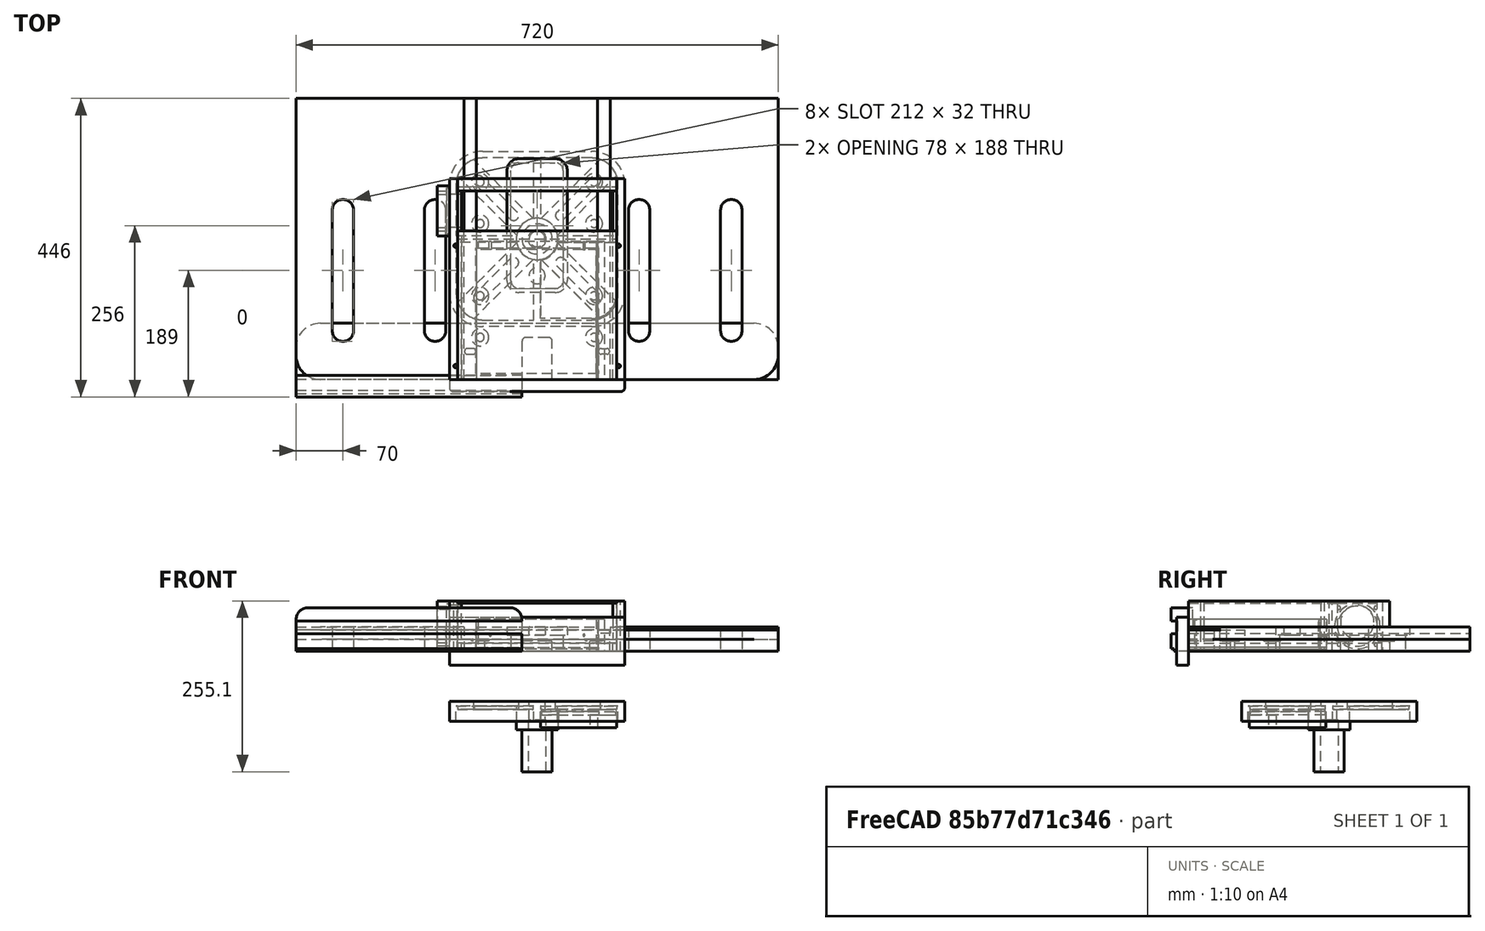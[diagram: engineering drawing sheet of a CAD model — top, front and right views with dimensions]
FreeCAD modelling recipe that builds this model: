
FCSTD DOCUMENT  (FreeCAD 0.22R36874 (Git))
Label: drill_press_table
License: All rights reserved
LicenseURL: http://en.wikipedia.org/wiki/All_rights_reserved
objects: TechDraw::DrawViewDimension×76, Sketcher::SketchObject×58, PartDesign::Pocket×35, PartDesign::Pad×21, PartDesign::Body×21, TechDraw::DrawProjGroupItem×16, TechDraw::DrawSVGTemplate×7, TechDraw::DrawProjGroup×7, TechDraw::DrawPage×7, PartDesign::Mirrored×4, App::Part×4, PartDesign::FeatureBase×3, PartDesign::PolarPattern×3, TechDraw::DrawViewImage×3, TechDraw::DrawComplexSection×2, Spreadsheet::Sheet×1, PartDesign::Fillet×1, TechDraw::DrawViewAnnotation×1, App::DocumentObjectGroup×1
note: 314 computed .brp shape members not serialized (recipe doc carries the construction recipe); baked Part::Feature solids carry a one-line shape summary decoded from their .brp

FEATURE [Spreadsheet::Sheet] Spreadsheet
  cells = A1='table_length; B1(table_length)==720 mm; D1='plywood_18; E1(ply_18)==18 mm; F1='iron_cast_table; G1(iron_cast_table)==262 mm; I1='tee nuts DIN1624; L1='via holes diameters; A2='table_depth; B2(table_depth)==420 mm; D2='plywood_12; E2(ply_12)==12 mm; F2='mounting_screws_distance; G2(mounting_screws_distance)==170 mm; I2='M8_D; J2(DIN1624_M8_D)==22.2 mm; L2='M8_D; M2(otw_przel_M8)==8.4 mm; D3='plywood_3; E3(ply_3)==3 mm; I3='M8_d1; J3(DIN1624_M8_d1)==9.1 mm; A4='table_radius; B4(table_radius)==6 mm; I4='M8_a; J4(DIN1624_M8_a)==1.2 mm; I5='M8_L1; J5(DIN1624_M8_L1)==11 mm; A6='t_track_slim_width; B6(t_track_width)==19 mm; C6='https://allegro.pl/oferta/t-track-slim-1220mm-profil-aluminiowy-t-zielony-10608302634?fromVariant=12640372726; A7='t_track_slim_depth; B7(t_track_depth)==9.5 mm; D7='fence_base_d; E7(fence_base_d)==32 mm; I7='M10_D; J7(DIN1624_M10_D)==25.5 mm; D8='fence_face_d; E8(fence_face_d)==32 mm; I8='M10_d1; J8(DIN1624_M10_d1)==12 mm; A9='clamp_slot_width; B9(clamp_slot_width)==32 mm; I9='M10_a; J9(DIN1624_M10_a)==1.2 mm; I10='M10_L1; J10(DIN1624_M10_L1)==13 mm; A11='insert_width; B11(insert_width)==90 mm; D11='base_width; E11(base_width)==G1; A12='insert_depth; B12(insert_depth)==200 mm; D12='base_depth; E12(base_depth)==E1 + 60 mm + E2 + E15 + 10 mm; I12='M12_D; J12(DIN1624_M12_D)==27 mm; D13='base_height; E13(base_height)==75 mm; I13='M12_d1; J13(DIN1624_M12_d1)==13.7 mm; I14='M12_a; J14(DIN1624_M12_a)==1.6 mm; D15='drawer_depth; E15(drawer_depth)==200 mm; I15='M12_L1; J15(DIN1624_M12_L1)==14.5 mm; D16='drawer_slide_width; E16==12.7 mm; D17='drawer_total_depth; E17(drawer_total_depth)==E15 + 6 mm; D18='drawer_total_width; E18(drawer_total_width)==E11 - 2 * E1 - 2 * E16; D19='drawer_total_height; E19(drawer_total_height)==E13 - E1 - 9 mm
FEATURE [Sketcher::SketchObject] Sketch
  FullyConstrained = true
  MapMode = 5
  expr: .Constraints.table_radius_big = 6 * Spreadsheet.table_radius
  expr: Constraints[11] = .Constraints.table_radius_big
  expr: Constraints[12] = Spreadsheet.table_depth
  expr: Constraints[13] = Spreadsheet.table_length
  sketch-geometry (6):
    g0: LineSegment StartX=-360 StartY=420 StartZ=0 EndX=360 EndY=420 EndZ=0
    g1: LineSegment StartX=360 StartY=420 StartZ=0 EndX=360 EndY=36 EndZ=0
    g2: LineSegment StartX=324 StartY=3.695e-13 StartZ=0 EndX=-324 EndY=3.695e-13 EndZ=0
    g3: LineSegment StartX=-360 StartY=36 StartZ=0 EndX=-360 EndY=420 EndZ=0
    g4: ArcOfCircle CenterX=-324 CenterY=36 CenterZ=0 NormalX=0 NormalY=0 NormalZ=1 AngleXU=0 Radius=36 StartAngle=3.14159 EndAngle=4.71239
    g5: ArcOfCircle CenterX=324 CenterY=36 CenterZ=0 NormalX=0 NormalY=0 NormalZ=1 AngleXU=0 Radius=36 StartAngle=4.71239 EndAngle=6.28319
  constraints (15):
    c: Coincident(g0,g1)
    c: Coincident(g3,g0)
    c: Horizontal(g0)
    c: Horizontal(g2)
    c: Vertical(g1)
    c: Vertical(g3)
    c: Tangent(g3,g4) = 1.5708
    c: Tangent(g2,g4) = 1.5708
    c: Tangent(g2,g5) = 1.5708
    c: Tangent(g1,g5) = 1.5708
    c: Radius(g4) = 36  'table_radius_big'
    c: Radius(g5) = 36
    c: DistanceY(g2,g0) = 420
    c: DistanceX(g3,g1) = 720
    c: Symmetric(g2,g2,g-1)
FEATURE [PartDesign::Pad] Pad
  Direction = (0,0,1)
  Length = 18
  Length2 = 10
  Profile = -> Sketch
  ReferenceAxis = -> Sketch [N_Axis]
  Suppressed = false
  Type = 0
FEATURE [Sketcher::SketchObject] Sketch001
  FullyConstrained = true
  MapMode = 5
  Placement = pos=(0,0,18) rot=(0,0,1;0rad)
  expr: Constraints[12] = Spreadsheet.clamp_slot_width
  expr: Constraints[13] = Spreadsheet.clamp_slot_width
  expr: Constraints[14] = Spreadsheet.table_length / 2 - 70 mm
  expr: Constraints[15] = Spreadsheet.iron_cast_table / 2 + 2 / 3 * Spreadsheet.clamp_slot_width
  expr: Constraints[32] = Spreadsheet.clamp_slot_width
  expr: Constraints[33] = Spreadsheet.clamp_slot_width
  expr: Constraints[34] = Spreadsheet.iron_cast_table / 2 + 2 / 3 * Spreadsheet.clamp_slot_width
  expr: Constraints[35] = Spreadsheet.table_length / 2 - 70 mm
  expr: Constraints[52] = 2 * Spreadsheet.table_radius
  expr: Constraints[53] = 2 * Spreadsheet.table_radius
  expr: Constraints[54] = 2 * Spreadsheet.table_radius
  expr: Constraints[55] = 2 * Spreadsheet.table_radius
  expr: Constraints[56] = Spreadsheet.insert_depth - 2 * Spreadsheet.table_radius
  expr: Constraints[57] = Spreadsheet.insert_width - 2 * Spreadsheet.table_radius
  expr: Constraints[58] = (Spreadsheet.insert_width - 2 * Spreadsheet.table_radius) / 2
  expr: Constraints[59] = 130 mm + Spreadsheet.table_radius
  expr: Constraints[60] = Spreadsheet.DIN1624_M10_d1
  expr: Constraints[61] = Spreadsheet.mounting_screws_distance
  expr: Constraints[62] = Spreadsheet.mounting_screws_distance
  expr: Constraints[63] = Spreadsheet.mounting_screws_distance
  expr: Constraints[64] = Spreadsheet.mounting_screws_distance
  expr: Constraints[67] = Spreadsheet.mounting_screws_distance / 2
  expr: Constraints[68] = Spreadsheet.mounting_screws_distance / 2
  sketch-geometry (28):
    g0: ArcOfCircle CenterX=-290 CenterY=253 CenterZ=0 NormalX=0 NormalY=0 NormalZ=1 AngleXU=0 Radius=16 StartAngle=4e-16 EndAngle=3.14159
    g1: ArcOfCircle CenterX=-290 CenterY=73 CenterZ=0 NormalX=0 NormalY=0 NormalZ=1 AngleXU=0 Radius=16 StartAngle=3.14159 EndAngle=6.28319
    g2: LineSegment StartX=-306 StartY=253 StartZ=0 EndX=-306 EndY=73 EndZ=0
    g3: LineSegment StartX=-274 StartY=73 StartZ=0 EndX=-274 EndY=253 EndZ=0
    g4: ArcOfCircle CenterX=-152.333 CenterY=253 CenterZ=0 NormalX=0 NormalY=0 NormalZ=1 AngleXU=0 Radius=16 StartAngle=1e-16 EndAngle=3.14159
    g5: ArcOfCircle CenterX=-152.333 CenterY=73 CenterZ=0 NormalX=0 NormalY=0 NormalZ=1 AngleXU=0 Radius=16 StartAngle=3.14159 EndAngle=6.28319
    g6: LineSegment StartX=-168.333 StartY=253 StartZ=0 EndX=-168.333 EndY=73 EndZ=0
    g7: LineSegment StartX=-136.333 StartY=73 StartZ=0 EndX=-136.333 EndY=253 EndZ=0
    g8: ArcOfCircle CenterX=290 CenterY=253 CenterZ=0 NormalX=0 NormalY=0 NormalZ=1 AngleXU=0 Radius=16 StartAngle=5e-16 EndAngle=3.14159
    g9: ArcOfCircle CenterX=290 CenterY=73 CenterZ=0 NormalX=0 NormalY=0 NormalZ=1 AngleXU=0 Radius=16 StartAngle=3.14159 EndAngle=6.28319
    g10: LineSegment StartX=306 StartY=253 StartZ=0 EndX=306 EndY=73 EndZ=0
    g11: LineSegment StartX=274 StartY=73 StartZ=0 EndX=274 EndY=253 EndZ=0
    g12: ArcOfCircle CenterX=152.333 CenterY=253 CenterZ=0 NormalX=0 NormalY=0 NormalZ=1 AngleXU=0 Radius=16 StartAngle=5e-16 EndAngle=3.14159
    g13: ArcOfCircle CenterX=152.333 CenterY=73 CenterZ=0 NormalX=0 NormalY=0 NormalZ=1 AngleXU=0 Radius=16 StartAngle=3.14159 EndAngle=6.28319
    g14: LineSegment StartX=168.333 StartY=253 StartZ=0 EndX=168.333 EndY=73 EndZ=0
    g15: LineSegment StartX=136.333 StartY=73 StartZ=0 EndX=136.333 EndY=253 EndZ=0
    g16: LineSegment StartX=-27 StartY=324 StartZ=0 EndX=27 EndY=324 EndZ=0
    g17: LineSegment StartX=39 StartY=312 StartZ=0 EndX=39 EndY=148 EndZ=0
    g18: LineSegment StartX=27 StartY=136 StartZ=0 EndX=-27 EndY=136 EndZ=0
    g19: LineSegment StartX=-39 StartY=148 StartZ=0 EndX=-39 EndY=312 EndZ=0
    g20: ArcOfCircle CenterX=-27 CenterY=312 CenterZ=0 NormalX=0 NormalY=0 NormalZ=1 AngleXU=0 Radius=12 StartAngle=1.5708 EndAngle=3.14159
    g21: ArcOfCircle CenterX=27 CenterY=312 CenterZ=0 NormalX=0 NormalY=0 NormalZ=1 AngleXU=0 Radius=12 StartAngle=3.37e-14 EndAngle=1.5708
    g22: ArcOfCircle CenterX=-27 CenterY=148 CenterZ=0 NormalX=0 NormalY=0 NormalZ=1 AngleXU=0 Radius=12 StartAngle=3.14159 EndAngle=4.71239
    g23: ArcOfCircle CenterX=27 CenterY=148 CenterZ=0 NormalX=0 NormalY=0 NormalZ=1 AngleXU=0 Radius=12 StartAngle=4.71239 EndAngle=6.28319
    g24: Circle CenterX=-85 CenterY=125 CenterZ=0 NormalX=0 NormalY=0 NormalZ=1 AngleXU=0 Radius=6
    g25: Circle CenterX=-85 CenterY=295 CenterZ=0 NormalX=0 NormalY=0 NormalZ=1 AngleXU=0 Radius=6
    g26: Circle CenterX=85 CenterY=295 CenterZ=0 NormalX=0 NormalY=0 NormalZ=1 AngleXU=0 Radius=6
    g27: Circle CenterX=85 CenterY=125 CenterZ=0 NormalX=0 NormalY=0 NormalZ=1 AngleXU=0 Radius=6
  constraints (72):
    c: Tangent(g0,g2) = -1.5708
    c: Tangent(g2,g1) = -1.5708
    c: Tangent(g1,g3) = -1.5708
    c: Tangent(g3,g0) = -1.5708
    c: Equal(g0,g1)
    c: Vertical(g2)
    c: Tangent(g4,g6) = -1.5708
    c: Tangent(g6,g5) = -1.5708
    c: Tangent(g5,g7) = -1.5708
    c: Tangent(g7,g4) = -1.5708
    c: Equal(g4,g5)
    c: Vertical(g6)
    c: Diameter(g0) = 32
    c: Diameter(g4) = 32
    c: DistanceX(g1,g-1) = 290
    c: DistanceX(g5,g-1) = 152.333
    c: DistanceY(g-1,g1) = 73
    c: DistanceY(g-1,g5) = 73
    c: DistanceY(g1,g0) = 180
    c: DistanceY(g5,g4) = 180
    c: Tangent(g8,g10) = 1.5708
    c: Tangent(g10,g9) = 1.5708
    c: Tangent(g9,g11) = 1.5708
    c: Tangent(g11,g8) = 1.5708
    c: Equal(g8,g9)
    c: Vertical(g10)
    c: Tangent(g12,g14) = 1.5708
    c: Tangent(g14,g13) = 1.5708
    c: Tangent(g13,g15) = 1.5708
    c: Tangent(g15,g12) = 1.5708
    c: Equal(g12,g13)
    c: Vertical(g14)
    c: Diameter(g8) = 32
    c: Diameter(g12) = 32
    c: DistanceX(g-1,g13) = 152.333
    c: DistanceX(g-1,g9) = 290
    c: DistanceY(g-1,g13) = 73
    c: DistanceY(g-1,g9) = 73
    c: DistanceY(g13,g12) = 180
    c: DistanceY(g9,g8) = 180
    c: Horizontal(g16)
    c: Horizontal(g18)
    c: Vertical(g17)
    c: Vertical(g19)
    c: Tangent(g19,g20) = 1.5708
    c: Tangent(g16,g20) = 1.5708
    c: Tangent(g16,g21) = 1.5708
    c: Tangent(g17,g21) = 1.5708
    c: Tangent(g19,g22) = 1.5708
    c: Tangent(g18,g22) = 1.5708
    c: Tangent(g18,g23) = 1.5708
    c: Tangent(g17,g23) = 1.5708
    c: Radius(g20) = 12
    c: Radius(g21) = 12
    c: Radius(g23) = 12
    c: Radius(g22) = 12
    c: DistanceY(g18,g16) = 188
    c: DistanceX(g19,g17) = 78
    c: DistanceX(g19,g-1) = 39
    c: DistanceY(g-1,g18) = 136
    c: Diameter(g25) = 12
    c: DistanceX(g24,g27) = 170
    c: DistanceX(g25,g26) = 170
    c: DistanceY(g24,g25) = 170
    c: DistanceY(g27,g26) = 170
    c: DistanceY(g-1,g27) = 125
    c: DistanceY(g-1,g24) = 125
    c: DistanceX(g24,g-1) = 85
    c: DistanceX(g25,g-1) = 85
    c: Equal(g25,g26)
    c: Equal(g26,g27)
    c: Equal(g27,g24)
FEATURE [PartDesign::Pocket] Pocket
  BaseFeature = -> Pad
  Direction = (0,0,-1)
  Length = 18
  Length2 = 5
  Profile = -> Sketch001
  ReferenceAxis = -> Sketch001 [N_Axis]
  Suppressed = false
  Type = 0
FEATURE [Sketcher::SketchObject] Sketch002
  FullyConstrained = true
  MapMode = 5
  expr: Constraints[10] = 6 * Spreadsheet.table_radius
  expr: Constraints[11] = 6 * Spreadsheet.table_radius
  expr: Constraints[12] = Spreadsheet.table_length
  expr: Constraints[13] = Spreadsheet.table_depth
  sketch-geometry (6):
    g0: LineSegment StartX=-360 StartY=420 StartZ=0 EndX=360 EndY=420 EndZ=0
    g1: LineSegment StartX=360 StartY=420 StartZ=0 EndX=360 EndY=36 EndZ=0
    g2: LineSegment StartX=324 StartY=3.695e-13 StartZ=0 EndX=-324 EndY=3.695e-13 EndZ=0
    g3: LineSegment StartX=-360 StartY=36 StartZ=0 EndX=-360 EndY=420 EndZ=0
    g4: ArcOfCircle CenterX=-324 CenterY=36 CenterZ=0 NormalX=0 NormalY=0 NormalZ=1 AngleXU=0 Radius=36 StartAngle=3.14159 EndAngle=4.71239
    g5: ArcOfCircle CenterX=324 CenterY=36 CenterZ=0 NormalX=0 NormalY=0 NormalZ=1 AngleXU=0 Radius=36 StartAngle=4.71239 EndAngle=6.28319
  constraints (15):
    c: Coincident(g0,g1)
    c: Coincident(g3,g0)
    c: Horizontal(g0)
    c: Horizontal(g2)
    c: Vertical(g1)
    c: Vertical(g3)
    c: Tangent(g3,g4) = 1.5708
    c: Tangent(g2,g4) = 1.5708
    c: Tangent(g2,g5) = 1.5708
    c: Tangent(g1,g5) = 1.5708
    c: Radius(g4) = 36
    c: Radius(g5) = 36
    c: DistanceX(g3,g1) = 720
    c: DistanceY(g2,g0) = 420
    c: Symmetric(g2,g2,g-1)
FEATURE [PartDesign::Pad] Pad001
  Direction = (0,0,1)
  Length = 18
  Length2 = 10
  Profile = -> Sketch002
  ReferenceAxis = -> Sketch002 [N_Axis]
  Suppressed = false
  Type = 0
  expr: Length = Spreadsheet.ply_18
FEATURE [Sketcher::SketchObject] Sketch003  label="slots"
  FullyConstrained = true
  MapMode = 5
  Placement = pos=(0,0,18) rot=(0,0,1;0rad)
  sketch-geometry (24):
    g0: ArcOfCircle CenterX=-290 CenterY=253 CenterZ=0 NormalX=0 NormalY=0 NormalZ=1 AngleXU=0 Radius=16 StartAngle=2e-16 EndAngle=3.14159
    g1: ArcOfCircle CenterX=-290 CenterY=73 CenterZ=0 NormalX=0 NormalY=0 NormalZ=1 AngleXU=0 Radius=16 StartAngle=3.14159 EndAngle=6.28319
    g2: LineSegment StartX=-306 StartY=253 StartZ=0 EndX=-306 EndY=73 EndZ=0
    g3: LineSegment StartX=-274 StartY=73 StartZ=0 EndX=-274 EndY=253 EndZ=0
    g4: ArcOfCircle CenterX=-152.333 CenterY=253 CenterZ=0 NormalX=0 NormalY=0 NormalZ=1 AngleXU=0 Radius=16 StartAngle=1.1e-15 EndAngle=3.14159
    g5: ArcOfCircle CenterX=-152.333 CenterY=73 CenterZ=0 NormalX=0 NormalY=0 NormalZ=1 AngleXU=0 Radius=16 StartAngle=3.14159 EndAngle=6.28319
    g6: LineSegment StartX=-168.333 StartY=253 StartZ=0 EndX=-168.333 EndY=73 EndZ=0
    g7: LineSegment StartX=-136.333 StartY=73 StartZ=0 EndX=-136.333 EndY=253 EndZ=0
    g8: ArcOfCircle CenterX=290 CenterY=253 CenterZ=0 NormalX=0 NormalY=0 NormalZ=1 AngleXU=0 Radius=16 StartAngle=-9e-16 EndAngle=3.14159
    g9: ArcOfCircle CenterX=290 CenterY=73 CenterZ=0 NormalX=0 NormalY=0 NormalZ=1 AngleXU=0 Radius=16 StartAngle=3.14159 EndAngle=6.28319
    g10: LineSegment StartX=306 StartY=253 StartZ=0 EndX=306 EndY=73 EndZ=0
    g11: LineSegment StartX=274 StartY=73 StartZ=0 EndX=274 EndY=253 EndZ=0
    g12: ArcOfCircle CenterX=152.333 CenterY=253 CenterZ=0 NormalX=0 NormalY=0 NormalZ=1 AngleXU=0 Radius=16 StartAngle=5e-16 EndAngle=3.14159
    g13: ArcOfCircle CenterX=152.333 CenterY=73 CenterZ=0 NormalX=0 NormalY=0 NormalZ=1 AngleXU=0 Radius=16 StartAngle=3.14159 EndAngle=6.28319
    g14: LineSegment StartX=168.333 StartY=253 StartZ=0 EndX=168.333 EndY=73 EndZ=0
    g15: LineSegment StartX=136.333 StartY=73 StartZ=0 EndX=136.333 EndY=253 EndZ=0
    g16: LineSegment StartX=-27 StartY=324 StartZ=0 EndX=27 EndY=324 EndZ=0
    g17: LineSegment StartX=39 StartY=312 StartZ=0 EndX=39 EndY=148 EndZ=0
    g18: LineSegment StartX=27 StartY=136 StartZ=0 EndX=-27 EndY=136 EndZ=0
    g19: LineSegment StartX=-39 StartY=148 StartZ=0 EndX=-39 EndY=312 EndZ=0
    g20: ArcOfCircle CenterX=-27 CenterY=312 CenterZ=0 NormalX=0 NormalY=0 NormalZ=1 AngleXU=0 Radius=12 StartAngle=1.5708 EndAngle=3.14159
    g21: ArcOfCircle CenterX=27 CenterY=312 CenterZ=0 NormalX=0 NormalY=0 NormalZ=1 AngleXU=0 Radius=12 StartAngle=3.58e-14 EndAngle=1.5708
    g22: ArcOfCircle CenterX=27 CenterY=148 CenterZ=0 NormalX=0 NormalY=0 NormalZ=1 AngleXU=0 Radius=12 StartAngle=4.71239 EndAngle=6.28319
    g23: ArcOfCircle CenterX=-27 CenterY=148 CenterZ=0 NormalX=0 NormalY=0 NormalZ=1 AngleXU=0 Radius=12 StartAngle=3.14159 EndAngle=4.71239
  constraints (60):
    c: Tangent(g0,g2) = -1.5708
    c: Tangent(g2,g1) = -1.5708
    c: Tangent(g1,g3) = -1.5708
    c: Tangent(g3,g0) = -1.5708
    c: Equal(g0,g1)
    c: Vertical(g2)
    c: Tangent(g4,g6) = -1.5708
    c: Tangent(g6,g5) = -1.5708
    c: Tangent(g5,g7) = -1.5708
    c: Tangent(g7,g4) = -1.5708
    c: Equal(g4,g5)
    c: Vertical(g6)
    c: Diameter(g0) = 32
    c: Diameter(g4) = 32
    c: DistanceX(g1,g-1) = 290  '1st_slot'
    c: DistanceX(g5,g-1) = 152.333  '2nd_slot'
    c: DistanceY(g-1,g1) = 73
    c: DistanceY(g-1,g5) = 73
    c: DistanceY(g1,g0) = 180
    c: DistanceY(g5,g4) = 180
    c: Tangent(g8,g10) = 1.5708
    c: Tangent(g10,g9) = 1.5708
    c: Tangent(g9,g11) = 1.5708
    c: Tangent(g11,g8) = 1.5708
    c: Equal(g8,g9)
    c: Vertical(g10)
    c: Tangent(g12,g14) = 1.5708
    c: Tangent(g14,g13) = 1.5708
    c: Tangent(g13,g15) = 1.5708
    c: Tangent(g15,g12) = 1.5708
    c: Equal(g12,g13)
    c: Vertical(g14)
    c: Diameter(g8) = 32
    c: Diameter(g12) = 32
    c: DistanceX(g-1,g13) = 152.333
    c: DistanceX(g-1,g9) = 290
    c: DistanceY(g-1,g13) = 73
    c: DistanceY(g-1,g9) = 73
    c: DistanceY(g13,g12) = 180
    c: DistanceY(g9,g8) = 180
    c: Horizontal(g16)
    c: Horizontal(g18)
    c: Vertical(g17)
    c: Vertical(g19)
    c: Tangent(g16,g20) = 1.5708
    c: Tangent(g19,g20) = 1.5708
    c: Tangent(g16,g21) = 1.5708
    c: Tangent(g17,g21) = 1.5708
    c: Tangent(g17,g22) = 1.5708
    c: Tangent(g18,g22) = 1.5708
    c: Tangent(g18,g23) = 1.5708
    c: Tangent(g19,g23) = 1.5708
    c: Radius(g20) = 12
    c: Radius(g21) = 12
    c: Radius(g22) = 12
    c: Radius(g23) = 12
    c: DistanceX(g19,g17) = 78
    c: DistanceY(g-1,g18) = 136
    c: DistanceY(g18,g16) = 188
    c: DistanceX(g19,g-1) = 39
FEATURE [PartDesign::Pocket] Pocket001
  BaseFeature = -> Pad001
  Direction = (0,0,-1)
  Length = 18
  Length2 = 5
  Profile = -> Sketch003
  ReferenceAxis = -> Sketch003 [N_Axis]
  Suppressed = false
  Type = 0
  expr: Length = Spreadsheet.ply_18
FEATURE [Sketcher::SketchObject] Sketch004  label="t_tracks_sk"
  FullyConstrained = true
  MapMode = 5
  Placement = pos=(0,0,18) rot=(0,0,1;0rad)
  expr: .Constraints.t_track_distance = 100 mm - Spreadsheet.t_track_width / 2
  expr: Constraints[17] = Spreadsheet.t_track_width
  expr: Constraints[19] = Spreadsheet.table_depth
  sketch-geometry (8):
    g0: LineSegment StartX=-109.5 StartY=420 StartZ=0 EndX=-90.5 EndY=420 EndZ=0
    g1: LineSegment StartX=-90.5 StartY=420 StartZ=0 EndX=-90.5 EndY=0 EndZ=0
    g2: LineSegment StartX=-90.5 StartY=0 StartZ=0 EndX=-109.5 EndY=0 EndZ=0
    g3: LineSegment StartX=-109.5 StartY=0 StartZ=0 EndX=-109.5 EndY=420 EndZ=0
    g4: LineSegment StartX=109.5 StartY=420 StartZ=0 EndX=90.5 EndY=420 EndZ=0
    g5: LineSegment StartX=90.5 StartY=420 StartZ=0 EndX=90.5 EndY=0 EndZ=0
    g6: LineSegment StartX=90.5 StartY=0 StartZ=0 EndX=109.5 EndY=0 EndZ=0
    g7: LineSegment StartX=109.5 StartY=0 StartZ=0 EndX=109.5 EndY=420 EndZ=0
  constraints (23):
    c: Coincident(g0,g1)
    c: Coincident(g1,g2)
    c: Coincident(g2,g3)
    c: Coincident(g3,g0)
    c: Horizontal(g0)
    c: Horizontal(g2)
    c: Vertical(g1)
    c: Vertical(g3)
    c: Coincident(g4,g5)
    c: Coincident(g5,g6)
    c: Coincident(g6,g7)
    c: Coincident(g7,g4)
    c: Horizontal(g4)
    c: Horizontal(g6)
    c: Vertical(g5)
    c: Vertical(g7)
    c: Equal(g1,g7)
    c: DistanceX(g0,g0) = 19
    c: Equal(g0,g4)
    c: DistanceY(g3,g3) = 420
    c: DistanceX(g1,g-1) = 90.5  't_track_distance'
    c: DistanceY(g1,g-1) = 0
    c: Symmetric(g1,g5,g-1)
FEATURE [PartDesign::Pocket] Pocket002
  BaseFeature = -> Pocket001
  Direction = (0,0,-1)
  Length = 9.5
  Length2 = 5
  Profile = -> Sketch004
  ReferenceAxis = -> Sketch004 [N_Axis]
  Suppressed = false
  Type = 0
  expr: Length = Spreadsheet.t_track_depth
FEATURE [Sketcher::SketchObject] Sketch005
  FullyConstrained = true
  MapMode = 5
  expr: Constraints[26] = Spreadsheet.iron_cast_table
  expr: Constraints[5] = Spreadsheet.iron_cast_table
  sketch-geometry (12):
    g0: LineSegment StartX=-81 StartY=131 StartZ=0 EndX=81 EndY=131 EndZ=0
    g1: LineSegment StartX=131 StartY=81 StartZ=0 EndX=131 EndY=-81 EndZ=0
    g2: LineSegment StartX=81 StartY=-131 StartZ=0 EndX=-81 EndY=-131 EndZ=0
    g3: LineSegment StartX=-131 StartY=-81 StartZ=0 EndX=-131 EndY=81 EndZ=0
    g4: ArcOfCircle CenterX=-81 CenterY=81 CenterZ=0 NormalX=0 NormalY=0 NormalZ=1 AngleXU=0 Radius=50 StartAngle=1.5708 EndAngle=3.14159
    g5: GeomPoint X=-131 Y=131 Z=0
    g6: ArcOfCircle CenterX=81 CenterY=81 CenterZ=0 NormalX=0 NormalY=0 NormalZ=1 AngleXU=0 Radius=50 StartAngle=0 EndAngle=1.5708
    g7: GeomPoint X=131 Y=131 Z=0
    g8: ArcOfCircle CenterX=81 CenterY=-81 CenterZ=0 NormalX=0 NormalY=0 NormalZ=1 AngleXU=0 Radius=50 StartAngle=4.71239 EndAngle=6.28319
    g9: GeomPoint X=131 Y=-131 Z=0
    g10: ArcOfCircle CenterX=-81 CenterY=-81 CenterZ=0 NormalX=0 NormalY=0 NormalZ=1 AngleXU=0 Radius=50 StartAngle=3.14159 EndAngle=4.71239
    g11: GeomPoint X=-131 Y=-131 Z=0
  constraints (27):
    c: Horizontal(g0)
    c: Horizontal(g2)
    c: Vertical(g1)
    c: Vertical(g3)
    c: Symmetric(g5,g9,g-1)
    c: DistanceX(g11,g9) = 262
    c: PointOnObject(g5,g3)
    c: PointOnObject(g5,g0)
    c: Tangent(g3,g4) = 1.5708
    c: Tangent(g0,g4) = 1.5708
    c: PointOnObject(g7,g0)
    c: PointOnObject(g7,g1)
    c: Tangent(g0,g6) = 1.5708
    c: Tangent(g1,g6) = 1.5708
    c: PointOnObject(g9,g1)
    c: PointOnObject(g9,g2)
    c: Tangent(g1,g8) = 1.5708
    c: Tangent(g2,g8) = 1.5708
    c: PointOnObject(g11,g2)
    c: PointOnObject(g11,g3)
    c: Tangent(g2,g10) = 1.5708
    c: Tangent(g3,g10) = 1.5708
    c: Radius(g4) = 50
    c: Equal(g4,g6)
    c: Equal(g6,g8)
    c: Equal(g8,g10)
    c: DistanceY(g2,g0) = 262
FEATURE [PartDesign::Pad] Pad002
  Direction = (0,0,1)
  Length = 30
  Length2 = 10
  Profile = -> Sketch005
  ReferenceAxis = -> Sketch005 [N_Axis]
  Suppressed = false
  Type = 0
FEATURE [Sketcher::SketchObject] Sketch006
  ExternalGeometry = -> [Pocket]
  FullyConstrained = true
  MapMode = 5
  Placement = pos=(0,0,18) rot=(0,0,1;0rad)
  expr: Constraints[5] = Spreadsheet.DIN1624_M10_D
  sketch-geometry (4):
    g0: Circle CenterX=-85 CenterY=295 CenterZ=0 NormalX=0 NormalY=0 NormalZ=1 AngleXU=0 Radius=12.75
    g1: Circle CenterX=85 CenterY=295 CenterZ=0 NormalX=0 NormalY=0 NormalZ=1 AngleXU=0 Radius=12.75
    g2: Circle CenterX=-85 CenterY=125 CenterZ=0 NormalX=0 NormalY=0 NormalZ=1 AngleXU=0 Radius=12.75
    g3: Circle CenterX=85 CenterY=125 CenterZ=0 NormalX=0 NormalY=0 NormalZ=1 AngleXU=0 Radius=12.75
  constraints (8):
    c: Coincident(g0,g-4)
    c: Coincident(g1,g-5)
    c: Equal(g2,g0)
    c: Equal(g0,g1)
    c: Equal(g1,g3)
    c: Diameter(g2) = 25.5
    c: Coincident(g2,g-6)
    c: Coincident(g3,g-3)
FEATURE [PartDesign::Pocket] Pocket003
  BaseFeature = -> Pocket
  Direction = (0,0,-1)
  Length = 2.4
  Length2 = 5
  Profile = -> Sketch006
  ReferenceAxis = -> Sketch006 [N_Axis]
  Suppressed = false
  Type = 0
  expr: Length = 2 * Spreadsheet.DIN1624_M10_a
FEATURE [Sketcher::SketchObject] Sketch007
  ExternalGeometry = -> [Pocket002]
  FullyConstrained = true
  MapMode = 5
  Placement = pos=(0,0,18) rot=(0,0,1;0rad)
  expr: Constraints[12] = Spreadsheet.insert_width
  sketch-geometry (8):
    g0: LineSegment StartX=-27 StartY=330 StartZ=0 EndX=27 EndY=330 EndZ=0
    g1: LineSegment StartX=45 StartY=312 StartZ=0 EndX=45 EndY=148 EndZ=0
    g2: LineSegment StartX=27 StartY=130 StartZ=0 EndX=-27 EndY=130 EndZ=0
    g3: LineSegment StartX=-45 StartY=148 StartZ=0 EndX=-45 EndY=312 EndZ=0
    g4: ArcOfCircle CenterX=-27 CenterY=312 CenterZ=0 NormalX=0 NormalY=0 NormalZ=1 AngleXU=0 Radius=18 StartAngle=1.5708 EndAngle=3.14159
    g5: ArcOfCircle CenterX=27 CenterY=312 CenterZ=0 NormalX=0 NormalY=0 NormalZ=1 AngleXU=0 Radius=18 StartAngle=9e-16 EndAngle=1.5708
    g6: ArcOfCircle CenterX=27 CenterY=148 CenterZ=0 NormalX=0 NormalY=0 NormalZ=1 AngleXU=0 Radius=18 StartAngle=4.71239 EndAngle=6.28319
    g7: ArcOfCircle CenterX=-27 CenterY=148 CenterZ=0 NormalX=0 NormalY=0 NormalZ=1 AngleXU=0 Radius=18 StartAngle=3.14159 EndAngle=4.71239
  constraints (18):
    c: Horizontal(g0)
    c: Horizontal(g2)
    c: Vertical(g1)
    c: Vertical(g3)
    c: Tangent(g0,g4) = 1.5708
    c: Tangent(g3,g4) = 1.5708
    c: Tangent(g0,g5) = 1.5708
    c: Tangent(g1,g5) = 1.5708
    c: Tangent(g1,g6) = 1.5708
    c: Tangent(g2,g6) = 1.5708
    c: Tangent(g2,g7) = 1.5708
    c: Tangent(g3,g7) = 1.5708
    c: DistanceX(g3,g1) = 90
    c: Equal(g7,g6)
    c: Equal(g6,g4)
    c: Equal(g4,g5)
    c: Coincident(g7,g-5)
    c: Coincident(g5,g-3)
FEATURE [PartDesign::Pocket] Pocket004
  BaseFeature = -> Pocket002
  Direction = (0,0,-1)
  Length = 12
  Length2 = 5
  Profile = -> Sketch007
  ReferenceAxis = -> Sketch007 [N_Axis]
  Suppressed = false
  Type = 0
  expr: Length = Spreadsheet.ply_12
FEATURE [Sketcher::SketchObject] Sketch008
  FullyConstrained = true
  MapMode = 5
  expr: Constraints[12] = 3 * Spreadsheet.table_radius
  expr: Constraints[16] = Spreadsheet.insert_depth
  expr: Constraints[17] = Spreadsheet.insert_width
  sketch-geometry (8):
    g0: LineSegment StartX=-27 StartY=100 StartZ=0 EndX=27 EndY=100 EndZ=0
    g1: LineSegment StartX=45 StartY=82 StartZ=0 EndX=45 EndY=-82 EndZ=0
    g2: LineSegment StartX=27 StartY=-100 StartZ=0 EndX=-27 EndY=-100 EndZ=0
    g3: LineSegment StartX=-45 StartY=-82 StartZ=0 EndX=-45 EndY=82 EndZ=0
    g4: ArcOfCircle CenterX=-27 CenterY=-82 CenterZ=0 NormalX=0 NormalY=0 NormalZ=1 AngleXU=0 Radius=18 StartAngle=3.14159 EndAngle=4.71239
    g5: ArcOfCircle CenterX=27 CenterY=-82 CenterZ=0 NormalX=0 NormalY=0 NormalZ=1 AngleXU=0 Radius=18 StartAngle=4.71239 EndAngle=6.28319
    g6: ArcOfCircle CenterX=27 CenterY=82 CenterZ=0 NormalX=0 NormalY=0 NormalZ=1 AngleXU=0 Radius=18 StartAngle=0 EndAngle=1.5708
    g7: ArcOfCircle CenterX=-27 CenterY=82 CenterZ=0 NormalX=0 NormalY=0 NormalZ=1 AngleXU=0 Radius=18 StartAngle=1.5708 EndAngle=3.14159
  constraints (19):
    c: Horizontal(g0)
    c: Horizontal(g2)
    c: Vertical(g1)
    c: Vertical(g3)
    c: Tangent(g3,g4) = 1.5708
    c: Tangent(g2,g4) = 1.5708
    c: Tangent(g2,g5) = 1.5708
    c: Tangent(g1,g5) = 1.5708
    c: Tangent(g1,g6) = 1.5708
    c: Tangent(g0,g6) = 1.5708
    c: Tangent(g0,g7) = 1.5708
    c: Tangent(g3,g7) = 1.5708
    c: Radius(g7) = 18
    c: Equal(g7,g6)
    c: Equal(g6,g5)
    c: Equal(g5,g4)
    c: DistanceY(g2,g0) = 200
    c: DistanceX(g3,g1) = 90
    c: Symmetric(g3,g1,g-1)
FEATURE [PartDesign::Pad] Pad003
  Direction = (0,0,1)
  Length = 12
  Length2 = 10
  Profile = -> Sketch008
  ReferenceAxis = -> Sketch008 [N_Axis]
  Suppressed = false
  Type = 0
  expr: Length = Spreadsheet.ply_12
FEATURE [Sketcher::SketchObject] Sketch009  label="base_pad"
  FullyConstrained = true
  MapMode = 5
  expr: .Constraints.fence_base_depth = 14 * Spreadsheet.table_radius
  expr: Constraints[10] = 6 * Spreadsheet.table_radius
  expr: Constraints[12] = Spreadsheet.table_length
  sketch-geometry (6):
    g0: LineSegment StartX=-324 StartY=84 StartZ=0 EndX=324 EndY=84 EndZ=0
    g1: LineSegment StartX=360 StartY=48 StartZ=0 EndX=360 EndY=0 EndZ=0
    g2: LineSegment StartX=360 StartY=0 StartZ=0 EndX=-360 EndY=0 EndZ=0
    g3: LineSegment StartX=-360 StartY=0 StartZ=0 EndX=-360 EndY=48 EndZ=0
    g4: ArcOfCircle CenterX=-324 CenterY=48 CenterZ=0 NormalX=0 NormalY=0 NormalZ=1 AngleXU=0 Radius=36 StartAngle=1.5708 EndAngle=3.14159
    g5: ArcOfCircle CenterX=324 CenterY=48 CenterZ=0 NormalX=0 NormalY=0 NormalZ=1 AngleXU=0 Radius=36 StartAngle=0 EndAngle=1.5708
  constraints (15):
    c: Coincident(g1,g2)
    c: Coincident(g2,g3)
    c: Horizontal(g0)
    c: Horizontal(g2)
    c: Vertical(g1)
    c: Vertical(g3)
    c: Tangent(g3,g4) = 1.5708
    c: Tangent(g0,g4) = 1.5708
    c: Tangent(g0,g5) = 1.5708
    c: Tangent(g1,g5) = 1.5708
    c: Radius(g4) = 36
    c: Equal(g4,g5)
    c: DistanceX(g2,g1) = 720
    c: DistanceY(g2,g0) = 84  'fence_base_depth'
    c: Symmetric(g2,g1,g-1)
FEATURE [PartDesign::Pad] Pad004
  Direction = (0,0,1)
  Length = 32
  Length2 = 10
  Profile = -> Sketch009
  ReferenceAxis = -> Sketch009 [N_Axis]
  Suppressed = false
  Type = 0
  expr: Length = Spreadsheet.fence_base_d
FEATURE [Sketcher::SketchObject] Sketch010
  FullyConstrained = true
  MapMode = 5
  Placement = pos=(0,0,32) rot=(0,0,1;0rad)
  expr: .Constraints.slot_length = Spreadsheet.otw_przel_M8
  expr: Constraints[6] = Spreadsheet.otw_przel_M8
  expr: Constraints[7] = 1 / 2 * <<base_pad>>.Constraints.fence_base_depth
  expr: Constraints[9] = Sketch004.Constraints.t_track_distance - .Constraints.slot_length / 2 + 9.5 mm
  sketch-geometry (4):
    g0: ArcOfCircle CenterX=-104.2 CenterY=42 CenterZ=0 NormalX=0 NormalY=0 NormalZ=1 AngleXU=0 Radius=4.2 StartAngle=1.5708 EndAngle=4.71239
    g1: ArcOfCircle CenterX=-95.8 CenterY=42 CenterZ=0 NormalX=0 NormalY=0 NormalZ=1 AngleXU=0 Radius=4.2 StartAngle=4.71239 EndAngle=7.85398
    g2: LineSegment StartX=-104.2 StartY=37.8 StartZ=0 EndX=-95.8 EndY=37.8 EndZ=0
    g3: LineSegment StartX=-95.8 StartY=46.2 StartZ=0 EndX=-104.2 EndY=46.2 EndZ=0
  constraints (10):
    c: Tangent(g0,g2) = -1.5708
    c: Tangent(g2,g1) = -1.5708
    c: Tangent(g1,g3) = -1.5708
    c: Tangent(g3,g0) = -1.5708
    c: Equal(g0,g1)
    c: Horizontal(g2)
    c: Diameter(g1) = 8.4
    c: DistanceY(g-1,g1) = 42
    c: DistanceX(g0,g1) = 8.4  'slot_length'
    c: DistanceX(g1,g-1) = 95.8
FEATURE [PartDesign::Pocket] Pocket005
  BaseFeature = -> Pad004
  Direction = (0,0,-1)
  Length = 32
  Length2 = 5
  Profile = -> Sketch010
  ReferenceAxis = -> Sketch010 [N_Axis]
  Suppressed = false
  Type = 0
  expr: Length = Spreadsheet.fence_base_d
FEATURE [PartDesign::Mirrored] Mirrored
  BaseFeature = -> Pocket005
  MirrorPlane = -> Sketch010 [V_Axis]
  Originals = -> [Pocket005]
  Suppressed = false
FEATURE [Sketcher::SketchObject] Sketch011
  FullyConstrained = true
  MapMode = 5
  Placement = pos=(0,0,0) rot=(1,0,0;3.14159rad)
  expr: Constraints[12] = Spreadsheet.table_radius
  expr: Constraints[13] = Spreadsheet.table_radius
  expr: Constraints[14] = 3 / 4 * <<base_pad>>.Constraints.fence_base_depth
  sketch-geometry (6):
    g0: LineSegment StartX=-22.5 StartY=0 StartZ=0 EndX=22.5 EndY=0 EndZ=0
    g1: LineSegment StartX=22.5 StartY=0 StartZ=0 EndX=22.5 EndY=-57 EndZ=0
    g2: LineSegment StartX=16.5 StartY=-63 StartZ=0 EndX=-16.5 EndY=-63 EndZ=0
    g3: LineSegment StartX=-22.5 StartY=-57 StartZ=0 EndX=-22.5 EndY=0 EndZ=0
    g4: ArcOfCircle CenterX=16.5 CenterY=-57 CenterZ=0 NormalX=0 NormalY=0 NormalZ=1 AngleXU=0 Radius=6 StartAngle=4.71239 EndAngle=6.28319
    g5: ArcOfCircle CenterX=-16.5 CenterY=-57 CenterZ=0 NormalX=0 NormalY=0 NormalZ=1 AngleXU=0 Radius=6 StartAngle=3.14159 EndAngle=4.71239
  constraints (15):
    c: Coincident(g0,g1)
    c: Coincident(g3,g0)
    c: Horizontal(g0)
    c: Horizontal(g2)
    c: Vertical(g1)
    c: Vertical(g3)
    c: DistanceX(g0,g0) = 45  'fence_opening'
    c: Symmetric(g0,g0,g-1)
    c: Tangent(g2,g4) = 1.5708
    c: Tangent(g1,g4) = 1.5708
    c: Tangent(g2,g5) = 1.5708
    c: Tangent(g3,g5) = 1.5708
    c: Radius(g5) = 6
    c: Radius(g4) = 6
    c: DistanceY(g2,g0) = 63
FEATURE [PartDesign::Pocket] Pocket006
  BaseFeature = -> Mirrored
  Direction = (0,0,1)
  Length = 16
  Length2 = 5
  Profile = -> Sketch011
  ReferenceAxis = -> Sketch011 [N_Axis]
  Suppressed = false
  Type = 0
  expr: Length = Spreadsheet.fence_base_d / 2
FEATURE [PartDesign::Body] Body005  label="fence_base"
  Group = -> [Sketch009,Pad004,Sketch010,Pocket005,Mirrored,Sketch011,Pocket006]
  Origin = -> Origin007
  Tip = -> Pocket006
FEATURE [Sketcher::SketchObject] Sketch012  label="fence_face"
  FullyConstrained = true
  MapMode = 5
  expr: .Constraints.fence_length = Spreadsheet.table_length / 2 - 45 mm / 2
  expr: Constraints[11] = 3 * Spreadsheet.table_radius
  sketch-geometry (6):
    g0: LineSegment StartX=18 StartY=65 StartZ=0 EndX=319.5 EndY=65 EndZ=0
    g1: LineSegment StartX=337.5 StartY=47 StartZ=0 EndX=337.5 EndY=0 EndZ=0
    g2: LineSegment StartX=337.5 StartY=0 StartZ=0 EndX=0 EndY=0 EndZ=0
    g3: LineSegment StartX=0 StartY=0 StartZ=0 EndX=0 EndY=47 EndZ=0
    g4: ArcOfCircle CenterX=18 CenterY=47 CenterZ=0 NormalX=0 NormalY=0 NormalZ=1 AngleXU=0 Radius=18 StartAngle=1.5708 EndAngle=3.14159
    g5: ArcOfCircle CenterX=319.5 CenterY=47 CenterZ=0 NormalX=0 NormalY=0 NormalZ=1 AngleXU=0 Radius=18 StartAngle=0 EndAngle=1.5708
  constraints (15):
    c: Coincident(g1,g2)
    c: Coincident(g2,g3)
    c: Horizontal(g0)
    c: Horizontal(g2)
    c: Vertical(g1)
    c: Vertical(g3)
    c: Tangent(g3,g4) = 1.5708
    c: Tangent(g0,g4) = 1.5708
    c: Tangent(g0,g5) = 1.5708
    c: Tangent(g1,g5) = 1.5708
    c: Equal(g4,g5)
    c: Radius(g4) = 18
    c: DistanceX(g2,g2) = 337.5  'fence_length'
    c: Coincident(g2,g-1)
    c: DistanceY(g1,g0) = 65  'fence_height'
FEATURE [PartDesign::Pad] Pad005
  Direction = (0,0,1)
  Length = 32
  Length2 = 10
  Profile = -> Sketch012
  ReferenceAxis = -> Sketch012 [N_Axis]
  Suppressed = false
  Type = 0
  expr: Length = Spreadsheet.fence_face_d
FEATURE [Sketcher::SketchObject] Sketch013
  FullyConstrained = true
  MapMode = 5
  Placement = pos=(0,0,32) rot=(0,0,1;0rad)
  expr: Constraints[11] = Sketch012.Constraints.fence_height / 2 - 9.5 mm + 3 mm
  expr: Constraints[8] = Spreadsheet.t_track_width
  expr: Constraints[9] = Sketch012.Constraints.fence_length
  sketch-geometry (4):
    g0: LineSegment StartX=0 StartY=45 StartZ=0 EndX=337.5 EndY=45 EndZ=0
    g1: LineSegment StartX=337.5 StartY=45 StartZ=0 EndX=337.5 EndY=26 EndZ=0
    g2: LineSegment StartX=337.5 StartY=26 StartZ=0 EndX=0 EndY=26 EndZ=0
    g3: LineSegment StartX=0 StartY=26 StartZ=0 EndX=0 EndY=45 EndZ=0
  constraints (12):
    c: Coincident(g0,g1)
    c: Coincident(g1,g2)
    c: Coincident(g2,g3)
    c: Coincident(g3,g0)
    c: Horizontal(g0)
    c: Horizontal(g2)
    c: Vertical(g1)
    c: Vertical(g3)
    c: DistanceY(g3,g3) = 19
    c: DistanceX(g2,g2) = 337.5
    c: DistanceX(g2,g-1) = 0
    c: DistanceY(g-1,g2) = 26
FEATURE [PartDesign::Pocket] Pocket007
  BaseFeature = -> Pad005
  Direction = (0,0,-1)
  Length = 9.5
  Length2 = 5
  Profile = -> Sketch013
  ReferenceAxis = -> Sketch013 [N_Axis]
  Suppressed = false
  Type = 0
  expr: Length = Spreadsheet.t_track_depth
FEATURE [Sketcher::SketchObject] Sketch014
  FullyConstrained = true
  MapMode = 5
  Placement = pos=(0,0,32) rot=(0,0,1;0rad)
  expr: Constraints[10] = Sketch012.Constraints.fence_length
  sketch-geometry (4):
    g0: LineSegment StartX=0 StartY=4 StartZ=0 EndX=337.5 EndY=4 EndZ=0
    g1: LineSegment StartX=337.5 StartY=4 StartZ=0 EndX=337.5 EndY=0 EndZ=0
    g2: LineSegment StartX=337.5 StartY=0 StartZ=0 EndX=0 EndY=0 EndZ=0
    g3: LineSegment StartX=0 StartY=0 StartZ=0 EndX=0 EndY=4 EndZ=0
  constraints (11):
    c: Coincident(g0,g1)
    c: Coincident(g1,g2)
    c: Coincident(g2,g3)
    c: Coincident(g3,g0)
    c: Horizontal(g0)
    c: Horizontal(g2)
    c: Vertical(g1)
    c: Vertical(g3)
    c: DistanceY(g1,g1) = 4
    c: Coincident(g2,g-1)
    c: DistanceX(g2,g2) = 337.5
FEATURE [PartDesign::Pocket] Pocket008
  BaseFeature = -> Pocket007
  Direction = (0,0,-1)
  Length = 4
  Length2 = 5
  Profile = -> Sketch014
  ReferenceAxis = -> Sketch014 [N_Axis]
  Suppressed = false
  Type = 0
FEATURE [Sketcher::SketchObject] Sketch015
  FullyConstrained = true
  MapMode = 5
  Placement = pos=(0,0,0) rot=(1,0,0;3.14159rad)
  expr: Constraints[8] = Spreadsheet.fence_base_d
  expr: Constraints[9] = Sketch012.Constraints.fence_length
  sketch-geometry (4):
    g0: LineSegment StartX=0 StartY=0 StartZ=0 EndX=337.5 EndY=0 EndZ=0
    g1: LineSegment StartX=337.5 StartY=0 StartZ=0 EndX=337.5 EndY=-32 EndZ=0
    g2: LineSegment StartX=337.5 StartY=-32 StartZ=0 EndX=0 EndY=-32 EndZ=0
    g3: LineSegment StartX=0 StartY=-32 StartZ=0 EndX=0 EndY=0 EndZ=0
  constraints (11):
    c: Coincident(g0,g1)
    c: Coincident(g1,g2)
    c: Coincident(g2,g3)
    c: Coincident(g3,g0)
    c: Horizontal(g0)
    c: Horizontal(g2)
    c: Vertical(g1)
    c: Vertical(g3)
    c: DistanceY(g1,g1) = 32
    c: DistanceX(g0,g0) = 337.5
    c: Coincident(g-1,g0)
FEATURE [PartDesign::Pocket] Pocket009
  BaseFeature = -> Pocket008
  Direction = (0,0,1)
  Length = 6
  Length2 = 5
  Profile = -> Sketch015
  ReferenceAxis = -> Sketch015 [N_Axis]
  Suppressed = false
  Type = 0
FEATURE [PartDesign::Body] Body004  label="fence_face_r"
  Group = -> [Sketch012,Pad005,Sketch013,Pocket007,Sketch014,Pocket008,Sketch015,Pocket009]
  Origin = -> Origin004
  Placement = pos=(22.5,6,0) rot=(1,0,0;1.5708rad)
  Tip = -> Pocket009
FEATURE [PartDesign::FeatureBase] Clone
  BaseFeature = -> Body004
  Placement = pos=(22.5,6,0) rot=(1,0,0;1.5708rad)
  Suppressed = false
FEATURE [PartDesign::Body] Body006  label="fence_face_l"
  Group = -> [Clone]
  Origin = -> Origin008
  Placement = pos=(-382.5,0,0) rot=(0,0,1;0rad)
  Tip = -> Clone
  expr: .Placement.Base.x = -Spreadsheet.table_length / 2 - 45 mm / 2
FEATURE [App::Part] Part001  label="fence"
  Group = -> [Body004,Body005,Body006]
  Origin = -> Origin006
  Placement = pos=(0,300,36) rot=(0,0,1;0rad)
FEATURE [Sketcher::SketchObject] Sketch016  label="base_main_sk"
  FullyConstrained = true
  MapMode = 5
  expr: .Constraints.base_depth = Spreadsheet.base_depth - Spreadsheet.ply_18 + Spreadsheet.table_radius
  expr: .Constraints.base_width = Spreadsheet.iron_cast_table - 2 * Spreadsheet.ply_18 + 2 * Spreadsheet.table_radius
  sketch-geometry (4):
    g0: LineSegment StartX=-119 StartY=288 StartZ=0 EndX=119 EndY=288 EndZ=0
    g1: LineSegment StartX=119 StartY=288 StartZ=0 EndX=119 EndY=0 EndZ=0
    g2: LineSegment StartX=119 StartY=0 StartZ=0 EndX=-119 EndY=0 EndZ=0
    g3: LineSegment StartX=-119 StartY=0 StartZ=0 EndX=-119 EndY=288 EndZ=0
  constraints (11):
    c: Coincident(g0,g1)
    c: Coincident(g1,g2)
    c: Coincident(g2,g3)
    c: Coincident(g3,g0)
    c: Horizontal(g0)
    c: Horizontal(g2)
    c: Vertical(g1)
    c: Vertical(g3)
    c: Symmetric(g2,g1,g-1)
    c: DistanceX(g2,g2) = 238  'base_width'
    c: DistanceY(g3,g3) = 288  'base_depth'
FEATURE [PartDesign::Pad] Pad006
  Direction = (0,0,1)
  Length = 18
  Length2 = 10
  Profile = -> Sketch016
  ReferenceAxis = -> Sketch016 [N_Axis]
  Suppressed = false
  Type = 0
  expr: Length = Spreadsheet.ply_18
FEATURE [Sketcher::SketchObject] Sketch018
  FullyConstrained = true
  MapMode = 5
  Placement = pos=(-119,0,0) rot=(0.57735,-0.57735,-0.57735;2.0944rad)
  expr: Constraints[11] = <<base_main_sk>>.Constraints.base_depth
  expr: Constraints[8] = Spreadsheet.table_radius
  expr: Constraints[9] = Spreadsheet.ply_18 - Spreadsheet.table_radius
  sketch-geometry (4):
    g0: LineSegment StartX=-288 StartY=12 StartZ=0 EndX=-282 EndY=12 EndZ=0
    g1: LineSegment StartX=-282 StartY=12 StartZ=0 EndX=-282 EndY=0 EndZ=0
    g2: LineSegment StartX=-282 StartY=0 StartZ=0 EndX=-288 EndY=0 EndZ=0
    g3: LineSegment StartX=-288 StartY=0 StartZ=0 EndX=-288 EndY=12 EndZ=0
  constraints (12):
    c: Coincident(g0,g1)
    c: Coincident(g1,g2)
    c: Coincident(g2,g3)
    c: Coincident(g3,g0)
    c: Horizontal(g0)
    c: Horizontal(g2)
    c: Vertical(g1)
    c: Vertical(g3)
    c: DistanceX(g0,g0) = 6
    c: DistanceY(g3,g3) = 12
    c: DistanceY(g1,g-1) = 0
    c: DistanceX(g2,g-1) = 288
FEATURE [PartDesign::Pocket] Pocket010
  BaseFeature = -> Pad006
  Direction = (1,0,0)
  Length = 238
  Length2 = 5
  Profile = -> Sketch018
  ReferenceAxis = -> Sketch018 [N_Axis]
  Suppressed = false
  Type = 0
  expr: Length = <<base_main_sk>>.Constraints.base_width
FEATURE [Sketcher::SketchObject] Sketch017
  FullyConstrained = true
  MapMode = 5
  Placement = pos=(0,0,0) rot=(1,0,0;1.5708rad)
  expr: Constraints[10] = Spreadsheet.ply_18 - Spreadsheet.table_radius
  expr: Constraints[11] = <<base_main_sk>>.Constraints.base_width / 2
  expr: Constraints[8] = Spreadsheet.table_radius
  sketch-geometry (4):
    g0: LineSegment StartX=-119 StartY=12 StartZ=0 EndX=-113 EndY=12 EndZ=0
    g1: LineSegment StartX=-113 StartY=12 StartZ=0 EndX=-113 EndY=0 EndZ=0
    g2: LineSegment StartX=-113 StartY=0 StartZ=0 EndX=-119 EndY=0 EndZ=0
    g3: LineSegment StartX=-119 StartY=0 StartZ=0 EndX=-119 EndY=12 EndZ=0
  constraints (12):
    c: Coincident(g0,g1)
    c: Coincident(g1,g2)
    c: Coincident(g2,g3)
    c: Coincident(g3,g0)
    c: Horizontal(g0)
    c: Horizontal(g2)
    c: Vertical(g1)
    c: Vertical(g3)
    c: DistanceX(g0,g0) = 6
    c: DistanceY(g-1,g1) = 0
    c: DistanceY(g3,g3) = 12
    c: DistanceX(g2,g-1) = 119
FEATURE [PartDesign::Pocket] Pocket011
  BaseFeature = -> Pocket010
  Direction = (0,1,-2e-16)
  Length = 288
  Length2 = 5
  Profile = -> Sketch017
  ReferenceAxis = -> Sketch017 [N_Axis]
  Suppressed = false
  Type = 0
  expr: Length = <<base_main_sk>>.Constraints.base_depth
FEATURE [PartDesign::Mirrored] Mirrored001
  BaseFeature = -> Pocket011
  MirrorPlane = -> Sketch017 [V_Axis]
  Originals = -> [Pocket011]
  Suppressed = false
FEATURE [Sketcher::SketchObject] Sketch019
  FullyConstrained = true
  MapMode = 5
  Placement = pos=(0,0,18) rot=(0,0,1;0rad)
  expr: Constraints[0] = Spreadsheet.mounting_screws_distance / 2
  expr: Constraints[10] = Spreadsheet.mounting_screws_distance
  expr: Constraints[11] = Spreadsheet.mounting_screws_distance
  expr: Constraints[1] = Spreadsheet.DIN1624_M10_d1
  expr: Constraints[5] = Spreadsheet.mounting_screws_distance
  expr: Constraints[6] = Spreadsheet.mounting_screws_distance
  expr: Constraints[7] = (Spreadsheet.table_depth - Spreadsheet.mounting_screws_distance) / 2 - 62 mm
  sketch-geometry (4):
    g0: Circle CenterX=-85 CenterY=63 CenterZ=0 NormalX=0 NormalY=0 NormalZ=1 AngleXU=0 Radius=6
    g1: Circle CenterX=-85 CenterY=233 CenterZ=0 NormalX=0 NormalY=0 NormalZ=1 AngleXU=0 Radius=6
    g2: Circle CenterX=85 CenterY=233 CenterZ=0 NormalX=0 NormalY=0 NormalZ=1 AngleXU=0 Radius=6
    g3: Circle CenterX=85 CenterY=63 CenterZ=0 NormalX=0 NormalY=0 NormalZ=1 AngleXU=0 Radius=6
  constraints (12):
    c: DistanceX(g0,g-1) = 85
    c: Diameter(g0) = 12
    c: Equal(g0,g1)
    c: Equal(g1,g2)
    c: Equal(g2,g3)
    c: DistanceY(g0,g1) = 170
    c: DistanceX(g0,g3) = 170
    c: DistanceY(g-1,g0) = 63
    c: DistanceY(g3,g0) = 0
    c: DistanceX(g0,g1) = 0
    c: DistanceX(g0,g2) = 170
    c: DistanceY(g0,g2) = 170
FEATURE [PartDesign::Pocket] Pocket012
  BaseFeature = -> Mirrored001
  Direction = (0,0,-1)
  Length = 18
  Length2 = 5
  Profile = -> Sketch019
  ReferenceAxis = -> Sketch019 [N_Axis]
  Suppressed = false
  Type = 0
  expr: Length = Spreadsheet.ply_18
FEATURE [Sketcher::SketchObject] Sketch020
  ExternalGeometry = -> [Pocket012]
  FullyConstrained = true
  MapMode = 5
  Placement = pos=(0,0,18) rot=(0,0,1;0rad)
  expr: Constraints[3] = Spreadsheet.DIN1624_M10_D
  sketch-geometry (4):
    g0: Circle CenterX=-85 CenterY=63 CenterZ=0 NormalX=0 NormalY=0 NormalZ=1 AngleXU=0 Radius=12.75
    g1: Circle CenterX=85 CenterY=63 CenterZ=0 NormalX=0 NormalY=0 NormalZ=1 AngleXU=0 Radius=12.75
    g2: Circle CenterX=85 CenterY=233 CenterZ=0 NormalX=0 NormalY=0 NormalZ=1 AngleXU=0 Radius=12.75
    g3: Circle CenterX=-85 CenterY=233 CenterZ=0 NormalX=0 NormalY=0 NormalZ=1 AngleXU=0 Radius=12.75
  constraints (8):
    c: Equal(g0,g3)
    c: Equal(g3,g2)
    c: Equal(g2,g1)
    c: Diameter(g0) = 25.5
    c: Coincident(g3,g-5)
    c: Coincident(g2,g-6)
    c: Coincident(g0,g-3)
    c: Coincident(g1,g-4)
FEATURE [PartDesign::Pocket] Pocket013
  BaseFeature = -> Pocket012
  Direction = (0,0,-1)
  Length = 2.4
  Length2 = 5
  Profile = -> Sketch020
  ReferenceAxis = -> Sketch020 [N_Axis]
  Suppressed = false
  Type = 0
  expr: Length = 2 * Spreadsheet.DIN1624_M10_a
FEATURE [PartDesign::Body] Body007  label="base_bottom"
  Group = -> [Sketch016,Pad006,Sketch017,Sketch018,Pocket010,Pocket011,Mirrored001,Sketch019,Pocket012,Sketch020,Pocket013]
  Origin = -> Origin010
  Tip = -> Pocket013
FEATURE [Sketcher::SketchObject] Sketch021  label="side_left_main_sk"
  FullyConstrained = true
  MapMode = 5
  expr: .Constraints.side_height = Spreadsheet.base_height
  expr: .Constraints.side_length = Spreadsheet.base_depth
  sketch-geometry (4):
    g0: LineSegment StartX=-75 StartY=300 StartZ=0 EndX=0 EndY=300 EndZ=0
    g1: LineSegment StartX=0 StartY=300 StartZ=0 EndX=0 EndY=0 EndZ=0
    g2: LineSegment StartX=0 StartY=0 StartZ=0 EndX=-75 EndY=0 EndZ=0
    g3: LineSegment StartX=-75 StartY=0 StartZ=0 EndX=-75 EndY=300 EndZ=0
  constraints (11):
    c: Coincident(g0,g1)
    c: Coincident(g1,g2)
    c: Coincident(g2,g3)
    c: Coincident(g3,g0)
    c: Horizontal(g0)
    c: Horizontal(g2)
    c: Vertical(g1)
    c: Vertical(g3)
    c: DistanceX(g2,g2) = 75  'side_height'
    c: Coincident(g1,g-1)
    c: DistanceY(g1,g1) = 300  'side_length'
FEATURE [PartDesign::Pad] Pad007
  Direction = (0,0,1)
  Length = 18
  Length2 = 10
  Profile = -> Sketch021
  ReferenceAxis = -> Sketch021 [N_Axis]
  Suppressed = false
  Type = 0
  expr: Length = Spreadsheet.ply_18
FEATURE [Sketcher::SketchObject] Sketch022
  FullyConstrained = true
  MapMode = 5
  Placement = pos=(0,0,0) rot=(1,0,0;1.5708rad)
  expr: Constraints[10] = Spreadsheet.ply_18
  expr: Constraints[11] = Spreadsheet.ply_18
  expr: Constraints[20] = Spreadsheet.table_radius
  expr: Constraints[21] = Spreadsheet.ply_3
  expr: Constraints[22] = Spreadsheet.ply_18
  expr: Constraints[23] = Spreadsheet.base_height
  expr: Constraints[8] = Spreadsheet.table_radius
  expr: Constraints[9] = Spreadsheet.table_radius
  sketch-geometry (8):
    g0: LineSegment StartX=-18 StartY=18 StartZ=0 EndX=-12 EndY=18 EndZ=0
    g1: LineSegment StartX=-12 StartY=18 StartZ=0 EndX=-12 EndY=12 EndZ=0
    g2: LineSegment StartX=-12 StartY=12 StartZ=0 EndX=-18 EndY=12 EndZ=0
    g3: LineSegment StartX=-18 StartY=12 StartZ=0 EndX=-18 EndY=18 EndZ=0
    g4: LineSegment StartX=-75 StartY=18 StartZ=0 EndX=-72 EndY=18 EndZ=0
    g5: LineSegment StartX=-72 StartY=18 StartZ=0 EndX=-72 EndY=12 EndZ=0
    g6: LineSegment StartX=-72 StartY=12 StartZ=0 EndX=-75 EndY=12 EndZ=0
    g7: LineSegment StartX=-75 StartY=12 StartZ=0 EndX=-75 EndY=18 EndZ=0
  constraints (24):
    c: Coincident(g0,g1)
    c: Coincident(g1,g2)
    c: Coincident(g2,g3)
    c: Coincident(g3,g0)
    c: Horizontal(g0)
    c: Horizontal(g2)
    c: Vertical(g1)
    c: Vertical(g3)
    c: DistanceX(g0,g0) = 6
    c: DistanceY(g1,g1) = 6
    c: DistanceX(g0,g-1) = 18
    c: DistanceY(g-1,g0) = 18
    c: Coincident(g4,g5)
    c: Coincident(g5,g6)
    c: Coincident(g6,g7)
    c: Coincident(g7,g4)
    c: Horizontal(g4)
    c: Horizontal(g6)
    c: Vertical(g5)
    c: Vertical(g7)
    c: DistanceY(g7,g7) = 6
    c: DistanceX(g4,g4) = 3
    c: DistanceY(g-1,g4) = 18
    c: DistanceX(g4,g-1) = 75
FEATURE [Sketcher::SketchObject] Sketch023
  FullyConstrained = true
  MapMode = 5
  Placement = pos=(0,0,18) rot=(0,0,1;0rad)
  expr: Constraints[10] = Spreadsheet.ply_18
  expr: Constraints[11] = <<side_left_main_sk>>.Constraints.side_length
  expr: Constraints[20] = Spreadsheet.drawer_depth + 10 mm
  expr: Constraints[21] = Spreadsheet.ply_12
  expr: Constraints[22] = Spreadsheet.ply_18
  expr: Constraints[23] = Spreadsheet.base_height
  expr: Constraints[8] = <<side_left_main_sk>>.Constraints.side_height
  sketch-geometry (8):
    g0: LineSegment StartX=-75 StartY=300 StartZ=0 EndX=0 EndY=300 EndZ=0
    g1: LineSegment StartX=0 StartY=300 StartZ=0 EndX=0 EndY=282 EndZ=0
    g2: LineSegment StartX=0 StartY=282 StartZ=0 EndX=-75 EndY=282 EndZ=0
    g3: LineSegment StartX=-75 StartY=282 StartZ=0 EndX=-75 EndY=300 EndZ=0
    g4: LineSegment StartX=-75 StartY=222 StartZ=0 EndX=-18 EndY=222 EndZ=0
    g5: LineSegment StartX=-18 StartY=222 StartZ=0 EndX=-18 EndY=210 EndZ=0
    g6: LineSegment StartX=-18 StartY=210 StartZ=0 EndX=-75 EndY=210 EndZ=0
    g7: LineSegment StartX=-75 StartY=210 StartZ=0 EndX=-75 EndY=222 EndZ=0
  constraints (24):
    c: Coincident(g0,g1)
    c: Coincident(g1,g2)
    c: Coincident(g2,g3)
    c: Coincident(g3,g0)
    c: Horizontal(g0)
    c: Horizontal(g2)
    c: Vertical(g1)
    c: Vertical(g3)
    c: DistanceX(g0,g0) = 75
    c: DistanceX(g-1,g1) = 0
    c: DistanceY(g3,g3) = 18
    c: DistanceY(g-1,g0) = 300
    c: Coincident(g4,g5)
    c: Coincident(g5,g6)
    c: Coincident(g6,g7)
    c: Coincident(g7,g4)
    c: Horizontal(g4)
    c: Horizontal(g6)
    c: Vertical(g5)
    c: Vertical(g7)
    c: DistanceY(g-1,g5) = 210
    c: Distance(g5) = 12
    c: DistanceX(g5,g-1) = 18
    c: DistanceX(g6,g-1) = 75
FEATURE [PartDesign::Pocket] Pocket014
  BaseFeature = -> Pad007
  Direction = (0,0,-1)
  Length = 6
  Length2 = 5
  Profile = -> Sketch023
  ReferenceAxis = -> Sketch023 [N_Axis]
  Suppressed = false
  Type = 0
  expr: Length = Spreadsheet.table_radius
FEATURE [PartDesign::Pocket] Pocket015
  BaseFeature = -> Pocket014
  Direction = (0,1,-2e-16)
  Length = 300
  Length2 = 5
  Profile = -> Sketch022
  ReferenceAxis = -> Sketch022 [N_Axis]
  Suppressed = false
  Type = 0
  expr: Length = <<side_left_main_sk>>.Constraints.side_length
FEATURE [Sketcher::SketchObject] Sketch024
  FullyConstrained = true
  MapMode = 5
  Placement = pos=(0,0,0) rot=(1,0,0;3.14159rad)
  expr: Constraints[1] = (Spreadsheet.base_height - Spreadsheet.table_radius - Spreadsheet.ply_18) / 2 + Spreadsheet.ply_18
  expr: Constraints[2] = Spreadsheet.base_depth - Spreadsheet.ply_18 - 30 mm
  sketch-geometry (1):
    g0: Circle CenterX=-43.5 CenterY=-252 CenterZ=0 NormalX=0 NormalY=0 NormalZ=1 AngleXU=0 Radius=25
  constraints (3):
    c: Diameter(g0) = 50
    c: DistanceX(g0,g-1) = 43.5
    c: DistanceY(g0,g-1) = 252
FEATURE [PartDesign::Pocket] Pocket016
  BaseFeature = -> Pocket015
  Direction = (0,0,1)
  Length = 18
  Length2 = 5
  Profile = -> Sketch024
  ReferenceAxis = -> Sketch024 [N_Axis]
  Suppressed = false
  Type = 0
  expr: Length = Spreadsheet.ply_18
FEATURE [Sketcher::SketchObject] Sketch025
  FullyConstrained = true
  MapMode = 5
  expr: Constraints[10] = Spreadsheet.base_depth
  expr: Constraints[8] = Spreadsheet.base_height
  sketch-geometry (4):
    g0: LineSegment StartX=0 StartY=300 StartZ=0 EndX=75 EndY=300 EndZ=0
    g1: LineSegment StartX=75 StartY=300 StartZ=0 EndX=75 EndY=0 EndZ=0
    g2: LineSegment StartX=75 StartY=0 StartZ=0 EndX=0 EndY=0 EndZ=0
    g3: LineSegment StartX=0 StartY=0 StartZ=0 EndX=0 EndY=300 EndZ=0
  constraints (11):
    c: Coincident(g0,g1)
    c: Coincident(g1,g2)
    c: Coincident(g2,g3)
    c: Coincident(g3,g0)
    c: Horizontal(g0)
    c: Horizontal(g2)
    c: Vertical(g1)
    c: Vertical(g3)
    c: DistanceX(g2,g2) = 75
    c: Coincident(g2,g-1)
    c: DistanceY(g1,g1) = 300
FEATURE [PartDesign::Pad] Pad008
  Direction = (0,0,1)
  Length = 18
  Length2 = 10
  Profile = -> Sketch025
  ReferenceAxis = -> Sketch025 [N_Axis]
  Suppressed = false
  Type = 0
  expr: Length = Spreadsheet.ply_18
FEATURE [Sketcher::SketchObject] Sketch026
  FullyConstrained = true
  MapMode = 5
  Placement = pos=(0,0,18) rot=(0,0,1;0rad)
  expr: Constraints[16] = Spreadsheet.base_depth
  expr: Constraints[17] = Spreadsheet.ply_18
  expr: Constraints[19] = Spreadsheet.base_height
  expr: Constraints[20] = Spreadsheet.drawer_depth + 10 mm
  expr: Constraints[21] = Spreadsheet.ply_12
  expr: Constraints[22] = Spreadsheet.ply_18
  expr: Constraints[23] = Spreadsheet.base_height
  sketch-geometry (8):
    g0: LineSegment StartX=0 StartY=300 StartZ=0 EndX=75 EndY=300 EndZ=0
    g1: LineSegment StartX=75 StartY=300 StartZ=0 EndX=75 EndY=282 EndZ=0
    g2: LineSegment StartX=75 StartY=282 StartZ=0 EndX=0 EndY=282 EndZ=0
    g3: LineSegment StartX=0 StartY=282 StartZ=0 EndX=0 EndY=300 EndZ=0
    g4: LineSegment StartX=18 StartY=222 StartZ=0 EndX=75 EndY=222 EndZ=0
    g5: LineSegment StartX=75 StartY=222 StartZ=0 EndX=75 EndY=210 EndZ=0
    g6: LineSegment StartX=75 StartY=210 StartZ=0 EndX=18 EndY=210 EndZ=0
    g7: LineSegment StartX=18 StartY=210 StartZ=0 EndX=18 EndY=222 EndZ=0
  constraints (24):
    c: Coincident(g0,g1)
    c: Coincident(g1,g2)
    c: Coincident(g2,g3)
    c: Coincident(g3,g0)
    c: Horizontal(g0)
    c: Horizontal(g2)
    c: Vertical(g1)
    c: Vertical(g3)
    c: Coincident(g4,g5)
    c: Coincident(g5,g6)
    c: Coincident(g6,g7)
    c: Coincident(g7,g4)
    c: Horizontal(g4)
    c: Horizontal(g6)
    c: Vertical(g5)
    c: Vertical(g7)
    c: DistanceY(g-1,g0) = 300
    c: DistanceY(g1,g1) = 18
    c: DistanceX(g2,g-1) = 0
    c: DistanceX(g0,g0) = 75
    c: DistanceY(g-1,g6) = 210
    c: DistanceY(g5,g5) = 12
    c: DistanceX(g-1,g6) = 18
    c: DistanceX(g-1,g5) = 75
FEATURE [PartDesign::Pocket] Pocket017
  BaseFeature = -> Pad008
  Direction = (0,0,-1)
  Length = 6
  Length2 = 5
  Profile = -> Sketch026
  ReferenceAxis = -> Sketch026 [N_Axis]
  Suppressed = false
  Type = 0
  expr: Length = Spreadsheet.table_radius
FEATURE [Sketcher::SketchObject] Sketch027
  FullyConstrained = true
  MapMode = 5
  Placement = pos=(0,0,0) rot=(1,0,0;1.5708rad)
  expr: Constraints[17] = Spreadsheet.table_radius
  expr: Constraints[18] = Spreadsheet.table_radius
  expr: Constraints[19] = Spreadsheet.ply_3
  expr: Constraints[20] = Spreadsheet.ply_18
  expr: Constraints[21] = Spreadsheet.base_height
  expr: Constraints[22] = Spreadsheet.ply_18
  expr: Constraints[23] = Spreadsheet.ply_18
  sketch-geometry (8):
    g0: LineSegment StartX=12 StartY=18 StartZ=0 EndX=18 EndY=18 EndZ=0
    g1: LineSegment StartX=18 StartY=18 StartZ=0 EndX=18 EndY=12 EndZ=0
    g2: LineSegment StartX=18 StartY=12 StartZ=0 EndX=12 EndY=12 EndZ=0
    g3: LineSegment StartX=12 StartY=12 StartZ=0 EndX=12 EndY=18 EndZ=0
    g4: LineSegment StartX=72 StartY=18 StartZ=0 EndX=75 EndY=18 EndZ=0
    g5: LineSegment StartX=75 StartY=18 StartZ=0 EndX=75 EndY=12 EndZ=0
    g6: LineSegment StartX=75 StartY=12 StartZ=0 EndX=72 EndY=12 EndZ=0
    g7: LineSegment StartX=72 StartY=12 StartZ=0 EndX=72 EndY=18 EndZ=0
  constraints (24):
    c: Coincident(g0,g1)
    c: Coincident(g1,g2)
    c: Coincident(g2,g3)
    c: Coincident(g3,g0)
    c: Horizontal(g0)
    c: Horizontal(g2)
    c: Vertical(g1)
    c: Vertical(g3)
    c: Coincident(g4,g5)
    c: Coincident(g5,g6)
    c: Coincident(g6,g7)
    c: Coincident(g7,g4)
    c: Horizontal(g4)
    c: Horizontal(g6)
    c: Vertical(g5)
    c: Vertical(g7)
    c: Equal(g1,g7)
    c: DistanceY(g3,g3) = 6
    c: DistanceX(g0,g0) = 6
    c: DistanceX(g4,g4) = 3
    c: DistanceX(g-1,g0) = 18
    c: DistanceX(g-1,g4) = 75
    c: DistanceY(g-1,g0) = 18
    c: DistanceY(g-1,g4) = 18
FEATURE [PartDesign::Pocket] Pocket018
  BaseFeature = -> Pocket017
  Direction = (0,1,-2e-16)
  Length = 300
  Length2 = 5
  Profile = -> Sketch027
  ReferenceAxis = -> Sketch027 [N_Axis]
  Suppressed = false
  Type = 0
  expr: Length = Spreadsheet.base_depth
FEATURE [Sketcher::SketchObject] Sketch028
  FullyConstrained = true
  MapMode = 5
  expr: Constraints[10] = Spreadsheet.base_width - 2 * (Spreadsheet.ply_18 - Spreadsheet.table_radius)
  expr: Constraints[9] = Spreadsheet.base_height - Spreadsheet.ply_18 - 3 mm
  sketch-geometry (4):
    g0: LineSegment StartX=-119 StartY=54 StartZ=0 EndX=119 EndY=54 EndZ=0
    g1: LineSegment StartX=119 StartY=54 StartZ=0 EndX=119 EndY=0 EndZ=0
    g2: LineSegment StartX=119 StartY=0 StartZ=0 EndX=-119 EndY=0 EndZ=0
    g3: LineSegment StartX=-119 StartY=0 StartZ=0 EndX=-119 EndY=54 EndZ=0
  constraints (11):
    c: Coincident(g0,g1)
    c: Coincident(g1,g2)
    c: Coincident(g2,g3)
    c: Coincident(g3,g0)
    c: Horizontal(g0)
    c: Horizontal(g2)
    c: Vertical(g1)
    c: Vertical(g3)
    c: Symmetric(g2,g1,g-1)
    c: DistanceY(g3,g3) = 54
    c: DistanceX(g2,g2) = 238
FEATURE [PartDesign::Pad] Pad009
  Direction = (0,0,1)
  Length = 12
  Length2 = 10
  Profile = -> Sketch028
  ReferenceAxis = -> Sketch028 [N_Axis]
  Suppressed = false
  Type = 0
  expr: Length = Spreadsheet.ply_12
FEATURE [PartDesign::Body] Body010  label="base_divider"
  Group = -> [Sketch028,Pad009]
  Origin = -> Origin014
  Placement = pos=(0,222,18) rot=(1,0,0;1.5708rad)
  Tip = -> Pad009
  expr: .Placement.Base.y = Spreadsheet.drawer_depth + 10 mm + Spreadsheet.ply_12
  expr: .Placement.Base.z = Spreadsheet.ply_18
FEATURE [Sketcher::SketchObject] Sketch029
  FullyConstrained = true
  MapMode = 5
  expr: Constraints[10] = Spreadsheet.base_width - 2 * (Spreadsheet.ply_18 - Spreadsheet.table_radius)
  expr: Constraints[9] = Spreadsheet.base_height
  sketch-geometry (4):
    g0: LineSegment StartX=-119 StartY=75 StartZ=0 EndX=119 EndY=75 EndZ=0
    g1: LineSegment StartX=119 StartY=75 StartZ=0 EndX=119 EndY=0 EndZ=0
    g2: LineSegment StartX=119 StartY=0 StartZ=0 EndX=-119 EndY=0 EndZ=0
    g3: LineSegment StartX=-119 StartY=0 StartZ=0 EndX=-119 EndY=75 EndZ=0
  constraints (11):
    c: Coincident(g0,g1)
    c: Coincident(g1,g2)
    c: Coincident(g2,g3)
    c: Coincident(g3,g0)
    c: Horizontal(g0)
    c: Horizontal(g2)
    c: Vertical(g1)
    c: Vertical(g3)
    c: Symmetric(g2,g1,g-1)
    c: DistanceY(g3,g3) = 75
    c: DistanceX(g0,g0) = 238
FEATURE [PartDesign::Pad] Pad010
  Direction = (0,0,1)
  Length = 18
  Length2 = 10
  Profile = -> Sketch029
  ReferenceAxis = -> Sketch029 [N_Axis]
  Suppressed = false
  Type = 0
  expr: Length = Spreadsheet.ply_18
FEATURE [Sketcher::SketchObject] Sketch030
  FullyConstrained = true
  MapMode = 5
  Placement = pos=(0,0,18) rot=(0,0,1;0rad)
  expr: Constraints[10] = Spreadsheet.base_width - 2 * (Spreadsheet.ply_18 - Spreadsheet.table_radius)
  expr: Constraints[11] = (Spreadsheet.base_width - 2 * (Spreadsheet.ply_18 - Spreadsheet.table_radius)) / 2
  expr: Constraints[8] = Spreadsheet.table_radius
  expr: Constraints[9] = Spreadsheet.ply_18
  sketch-geometry (4):
    g0: LineSegment StartX=-119 StartY=18 StartZ=0 EndX=119 EndY=18 EndZ=0
    g1: LineSegment StartX=119 StartY=18 StartZ=0 EndX=119 EndY=12 EndZ=0
    g2: LineSegment StartX=119 StartY=12 StartZ=0 EndX=-119 EndY=12 EndZ=0
    g3: LineSegment StartX=-119 StartY=12 StartZ=0 EndX=-119 EndY=18 EndZ=0
  constraints (12):
    c: Coincident(g0,g1)
    c: Coincident(g1,g2)
    c: Coincident(g2,g3)
    c: Coincident(g3,g0)
    c: Horizontal(g0)
    c: Horizontal(g2)
    c: Vertical(g1)
    c: Vertical(g3)
    c: DistanceY(g1,g1) = 6
    c: DistanceY(g-1,g0) = 18
    c: DistanceX(g2,g2) = 238
    c: DistanceX(g2,g-1) = 119
FEATURE [PartDesign::Pocket] Pocket019
  BaseFeature = -> Pad010
  Direction = (0,0,-1)
  Length = 6
  Length2 = 5
  Profile = -> Sketch030
  ReferenceAxis = -> Sketch030 [N_Axis]
  Suppressed = false
  Type = 0
  expr: Length = Spreadsheet.table_radius
FEATURE [PartDesign::Body] Body011  label="base_back"
  Group = -> [Sketch029,Pad010,Sketch030,Pocket019]
  Origin = -> Origin015
  Placement = pos=(0,300,0) rot=(1,0,0;1.5708rad)
  Tip = -> Pocket019
  expr: .Placement.Base.x = 0
  expr: .Placement.Base.y = Spreadsheet.base_depth
FEATURE [Sketcher::SketchObject] Sketch031
  FullyConstrained = true
  MapMode = 5
  Placement = pos=(-75,0,0) rot=(0.57735,-0.57735,-0.57735;2.0944rad)
  expr: Constraints[2] = Spreadsheet.ply_18 / 2
  expr: Constraints[3] = Spreadsheet.ply_18 / 2
  sketch-geometry (2):
    g0: Circle CenterX=-20 CenterY=9 CenterZ=0 NormalX=0 NormalY=0 NormalZ=1 AngleXU=0 Radius=2.5
    g1: Circle CenterX=-200 CenterY=9 CenterZ=0 NormalX=0 NormalY=0 NormalZ=1 AngleXU=0 Radius=2.5
  constraints (6):
    c: Equal(g1,g0)
    c: Diameter(g0) = 5
    c: DistanceY(g-1,g0) = 9
    c: DistanceY(g-1,g1) = 9
    c: DistanceX(g0,g-1) = 20
    c: DistanceX(g1,g-1) = 200
FEATURE [PartDesign::Pocket] Pocket020
  BaseFeature = -> Pocket016
  Direction = (1,0,0)
  Length = 75
  Length2 = 5
  Profile = -> Sketch031
  ReferenceAxis = -> Sketch031 [N_Axis]
  Suppressed = false
  Type = 0
  expr: Length = Spreadsheet.base_height
FEATURE [PartDesign::Body] Body008  label="base_side_left"
  Group = -> [Sketch021,Pad007,Sketch022,Sketch023,Pocket014,Pocket015,Sketch024,Pocket016,Sketch031,Pocket020]
  Origin = -> Origin011
  Placement = pos=(-131,0,0) rot=(0,1,0;1.5708rad)
  Tip = -> Pocket020
  expr: .Placement.Base.x = -(<<base_main_sk>>.Constraints.base_width / 2 + 2 / 3 * Spreadsheet.ply_18)
FEATURE [Sketcher::SketchObject] Sketch032
  FullyConstrained = true
  MapMode = 5
  Placement = pos=(75,0,0) rot=(0.57735,0.57735,0.57735;2.0944rad)
  expr: Constraints[4] = Spreadsheet.ply_18 / 2
  expr: Constraints[5] = Spreadsheet.ply_18 / 2
  sketch-geometry (2):
    g0: Circle CenterX=20 CenterY=9 CenterZ=0 NormalX=0 NormalY=0 NormalZ=1 AngleXU=0 Radius=2.5
    g1: Circle CenterX=200 CenterY=9 CenterZ=0 NormalX=0 NormalY=0 NormalZ=1 AngleXU=0 Radius=2.5
  constraints (6):
    c: Equal(g0,g1)
    c: Diameter(g0) = 5
    c: DistanceX(g-1,g0) = 20
    c: DistanceX(g-1,g1) = 200
    c: DistanceY(g-1,g0) = 9
    c: DistanceY(g-1,g1) = 9
FEATURE [PartDesign::Pocket] Pocket021
  BaseFeature = -> Pocket018
  Direction = (-1,0,0)
  Length = 75
  Length2 = 5
  Profile = -> Sketch032
  ReferenceAxis = -> Sketch032 [N_Axis]
  Suppressed = false
  Type = 0
  expr: Length = Spreadsheet.base_height
FEATURE [PartDesign::Body] Body009  label="base_side_right"
  Group = -> [Sketch025,Pad008,Sketch026,Pocket017,Sketch027,Pocket018,Sketch032,Pocket021]
  Origin = -> Origin013
  Placement = pos=(131,0,0) rot=(0,-1,0;1.5708rad)
  Tip = -> Pocket021
  expr: .Placement.Base.x = Spreadsheet.base_width / 2
FEATURE [Sketcher::SketchObject] Sketch033
  FullyConstrained = true
  MapMode = 5
  expr: Constraints[10] = Spreadsheet.base_height
  sketch-geometry (4):
    g0: LineSegment StartX=-37.5 StartY=37.5 StartZ=0 EndX=37.5 EndY=37.5 EndZ=0
    g1: LineSegment StartX=37.5 StartY=37.5 StartZ=0 EndX=37.5 EndY=-37.5 EndZ=0
    g2: LineSegment StartX=37.5 StartY=-37.5 StartZ=0 EndX=-37.5 EndY=-37.5 EndZ=0
    g3: LineSegment StartX=-37.5 StartY=-37.5 StartZ=0 EndX=-37.5 EndY=37.5 EndZ=0
  constraints (11):
    c: Coincident(g0,g1)
    c: Coincident(g1,g2)
    c: Coincident(g2,g3)
    c: Coincident(g3,g0)
    c: Horizontal(g0)
    c: Horizontal(g2)
    c: Vertical(g1)
    c: Vertical(g3)
    c: Symmetric(g0,g1,g-1)
    c: Equal(g3,g2)
    c: DistanceX(g2,g2) = 75
FEATURE [PartDesign::Pad] Pad011
  Direction = (0,0,1)
  Length = 18
  Length2 = 10
  Profile = -> Sketch033
  ReferenceAxis = -> Sketch033 [N_Axis]
  Suppressed = false
  Type = 0
  expr: Length = Spreadsheet.ply_18
FEATURE [Sketcher::SketchObject] Sketch034
  FullyConstrained = true
  MapMode = 5
  Placement = pos=(0,0,18) rot=(0,0,1;0rad)
  expr: Constraints[10] = Spreadsheet.base_height / 2 - 10 mm
  expr: Constraints[6] = Spreadsheet.base_height / 2 - 10 mm
  expr: Constraints[7] = Spreadsheet.base_height / 2 - 10 mm
  expr: Constraints[9] = Spreadsheet.base_height / 2 - 10 mm
  sketch-geometry (5):
    g0: Circle CenterX=0 CenterY=0 CenterZ=0 NormalX=0 NormalY=0 NormalZ=1 AngleXU=0 Radius=30
    g1: Circle CenterX=-27.5 CenterY=27.5 CenterZ=0 NormalX=0 NormalY=0 NormalZ=1 AngleXU=0 Radius=2.5
    g2: Circle CenterX=27.5 CenterY=27.5 CenterZ=0 NormalX=0 NormalY=0 NormalZ=1 AngleXU=0 Radius=2.5
    g3: Circle CenterX=27.5 CenterY=-27.5 CenterZ=0 NormalX=0 NormalY=0 NormalZ=1 AngleXU=0 Radius=2.5
    g4: Circle CenterX=-27.5 CenterY=-27.5 CenterZ=0 NormalX=0 NormalY=0 NormalZ=1 AngleXU=0 Radius=2.5
  constraints (12):
    c: Diameter(g0) = 60
    c: Coincident(g0,g-1)
    c: Equal(g1,g2)
    c: Equal(g2,g3)
    c: Equal(g3,g4)
    c: Diameter(g1) = 5
    c: DistanceY(g0,g1) = 27.5
    c: DistanceX(g1,g0) = 27.5
    c: Symmetric(g1,g3,g0)
    c: DistanceX(g4,g0) = 27.5
    c: DistanceY(g4,g0) = 27.5
    c: Symmetric(g4,g2,g0)
FEATURE [PartDesign::Pocket] Pocket022
  BaseFeature = -> Pad011
  Direction = (0,0,-1)
  Length = 18
  Length2 = 5
  Profile = -> Sketch034
  ReferenceAxis = -> Sketch034 [N_Axis]
  Suppressed = false
  Type = 0
  expr: Length = Spreadsheet.ply_18
FEATURE [Sketcher::SketchObject] Sketch035
  ExternalGeometry = -> [Pocket022]
  FullyConstrained = true
  MapMode = 5
  Placement = pos=(0,0,18) rot=(0,0,1;0rad)
  sketch-geometry (1):
    g0: Circle CenterX=0 CenterY=0 CenterZ=0 NormalX=0 NormalY=0 NormalZ=1 AngleXU=0 Radius=34
  constraints (2):
    c: Coincident(g0,g-3)
    c: Diameter(g0) = 68
FEATURE [PartDesign::Pocket] Pocket023
  BaseFeature = -> Pocket022
  Direction = (0,0,-1)
  Length = 4
  Length2 = 5
  Profile = -> Sketch035
  ReferenceAxis = -> Sketch035 [N_Axis]
  Suppressed = false
  Type = 0
FEATURE [PartDesign::Body] Body012  label="vacuum_port"
  Group = -> [Sketch033,Pad011,Sketch034,Pocket022,Sketch035,Pocket023]
  Origin = -> Origin016
  Placement = pos=(-149,252,37.5) rot=(0,1,0;1.5708rad)
  Tip = -> Pocket023
  expr: .Placement.Base.x = -(Spreadsheet.base_width / 2 + Spreadsheet.ply_18)
  expr: .Placement.Base.y = Spreadsheet.base_depth - Spreadsheet.ply_18 - 30 mm
  expr: .Placement.Base.z = Spreadsheet.base_height / 2
FEATURE [Sketcher::SketchObject] Sketch036
  FullyConstrained = true
  MapMode = 5
  expr: Constraints[10] = Spreadsheet.drawer_depth + 10 mm + Spreadsheet.ply_12
  expr: Constraints[9] = Spreadsheet.base_width - 2 * (Spreadsheet.ply_18 - Spreadsheet.table_radius)
  sketch-geometry (4):
    g0: LineSegment StartX=-119 StartY=0 StartZ=0 EndX=119 EndY=0 EndZ=0
    g1: LineSegment StartX=119 StartY=0 StartZ=0 EndX=119 EndY=222 EndZ=0
    g2: LineSegment StartX=119 StartY=222 StartZ=0 EndX=-119 EndY=222 EndZ=0
    g3: LineSegment StartX=-119 StartY=222 StartZ=0 EndX=-119 EndY=0 EndZ=0
  constraints (11):
    c: Coincident(g0,g1)
    c: Coincident(g1,g2)
    c: Coincident(g2,g3)
    c: Coincident(g3,g0)
    c: Horizontal(g0)
    c: Horizontal(g2)
    c: Vertical(g1)
    c: Vertical(g3)
    c: Symmetric(g0,g0,g-1)
    c: DistanceX(g0,g0) = 238
    c: DistanceY(g3,g3) = 222
FEATURE [PartDesign::Pad] Pad012
  Direction = (0,0,1)
  Length = 3
  Length2 = 10
  Profile = -> Sketch036
  ReferenceAxis = -> Sketch036 [N_Axis]
  Suppressed = false
  Type = 0
  expr: Length = Spreadsheet.ply_3
FEATURE [PartDesign::Body] Body013  label="base_top"
  Group = -> [Sketch036,Pad012]
  Origin = -> Origin017
  Placement = pos=(0,0,72) rot=(0,0,1;0rad)
  Tip = -> Pad012
  expr: .Placement.Base.z = Spreadsheet.base_height - Spreadsheet.ply_3
FEATURE [App::Part] Part002  label="base"
  Group = -> [Body007,Body008,Body009,Body010,Body011,Body012,Body013]
  Origin = -> Origin009
  Placement = pos=(0,62,-75) rot=(0,0,1;0rad)
  expr: .Placement.Base.y = Spreadsheet.ply_12 + 50 mm
  expr: .Placement.Base.z = -Spreadsheet.base_height
FEATURE [Sketcher::SketchObject] Sketch037  label="iron_table_bottom"
  FullyConstrained = true
  MapMode = 5
  Placement = pos=(0,0,0) rot=(1,0,0;3.14159rad)
  expr: .Constraints.iron_table_inner_length = (Spreadsheet.iron_cast_table - 30 mm) / 2
  expr: .Constraints.iron_table_inner_radius = 50 - 10
  expr: Constraints[7] = (Spreadsheet.iron_cast_table - 30 mm) / 2
  sketch-geometry (6):
    g0: LineSegment StartX=-81 StartY=121 StartZ=0 EndX=-5 EndY=121 EndZ=0
    g1: LineSegment StartX=-5 StartY=121 StartZ=0 EndX=-5 EndY=5 EndZ=0
    g2: LineSegment StartX=-5 StartY=5 StartZ=0 EndX=-121 EndY=5 EndZ=0
    g3: LineSegment StartX=-121 StartY=5 StartZ=0 EndX=-121 EndY=81 EndZ=0
    g4: ArcOfCircle CenterX=-81 CenterY=81 CenterZ=0 NormalX=0 NormalY=0 NormalZ=1 AngleXU=0 Radius=40 StartAngle=1.5708 EndAngle=3.14159
    g5: GeomPoint X=-121 Y=121 Z=0
  constraints (16):
    c: Coincident(g0,g1)
    c: Coincident(g1,g2)
    c: Coincident(g2,g3)
    c: Horizontal(g0)
    c: Horizontal(g2)
    c: Vertical(g1)
    c: Vertical(g3)
    c: DistanceX(g2,g2) = 116
    c: DistanceY(g1,g1) = 116  'iron_table_inner_length'
    c: PointOnObject(g5,g0)
    c: PointOnObject(g5,g3)
    c: Tangent(g0,g4) = 1.5708
    c: Tangent(g3,g4) = 1.5708
    c: Radius(g4) = 40  'iron_table_inner_radius'
    c: DistanceX(g1,g-1) = 5
    c: DistanceY(g-1,g1) = 5
FEATURE [PartDesign::Pocket] Pocket024
  BaseFeature = -> Pad002
  Direction = (0,0,1)
  Length = 23
  Length2 = 5
  Profile = -> Sketch037
  ReferenceAxis = -> Sketch037 [N_Axis]
  Suppressed = false
  Type = 0
  expr: Length = 30 - 7
FEATURE [PartDesign::PolarPattern] PolarPattern
  Angle = 360
  Axis = -> Sketch037 [N_Axis]
  BaseFeature = -> Pocket024
  Mode = 0
  Occurrences = 4
  Offset = 120
  Originals = -> [Pocket024]
  Suppressed = false
FEATURE [Sketcher::SketchObject] Sketch038
  AttachmentOffset = pos=(0,0,-0.1) rot=(0,0,1;0rad)
  FullyConstrained = false
  MapMode = 5
  Placement = pos=(0,0,29.9) rot=(0,0,1;0rad)
  sketch-geometry (7):
    g0: LineSegment StartX=-12.3919 StartY=12.3919 StartZ=0 EndX=99.5363 EndY=124.333 EndZ=0
    g1: LineSegment StartX=12.3373 StartY=-12.3374 StartZ=0 EndX=124.952 EndY=101.341 EndZ=0
    g2: LineSegment StartX=-12.3919 StartY=12.3919 StartZ=0 EndX=12.3373 EndY=-12.3374 EndZ=0
    g3: LineSegment StartX=99.5363 StartY=124.333 StartZ=0 EndX=105.391 EndY=122.551 EndZ=0
    g4: LineSegment StartX=110 StartY=120 StartZ=0 EndX=120 EndY=110 EndZ=0
    g5: LineSegment StartX=120 StartY=110 StartZ=0 EndX=124.952 EndY=101.341 EndZ=0
    g6: LineSegment StartX=105.391 StartY=122.551 StartZ=0 EndX=110 EndY=120 EndZ=0
  constraints (7):
    c: Coincident(g2,g0)
    c: Coincident(g2,g1)
    c: Coincident(g5,g4)
    c: Coincident(g6,g3)
    c: Coincident(g6,g4)
    c: Coincident(g3,g0)
    c: Coincident(g5,g1)
FEATURE [PartDesign::Pad] Pad013
  BaseFeature = -> PolarPattern
  Direction = (0,0,1)
  Length = 12
  Length2 = 10
  Profile = -> Sketch038
  ReferenceAxis = -> Sketch038 [N_Axis]
  Reversed = true
  Suppressed = false
  Type = 0
FEATURE [PartDesign::PolarPattern] PolarPattern001
  Angle = 360
  Axis = -> Sketch038 [N_Axis]
  BaseFeature = -> Pad013
  Mode = 0
  Occurrences = 4
  Offset = 120
  Originals = -> [Pad013]
  Suppressed = false
FEATURE [Sketcher::SketchObject] Sketch039
  AttachmentOffset = pos=(0,0,-0.1) rot=(0,0,1;0rad)
  FullyConstrained = true
  MapMode = 5
  Placement = pos=(0,0,29.9) rot=(0,0,1;0rad)
  sketch-geometry (1):
    g0: Circle CenterX=0 CenterY=0 CenterZ=0 NormalX=0 NormalY=0 NormalZ=1 AngleXU=0 Radius=31
  constraints (2):
    c: Coincident(g0,g-1)
    c: Diameter(g0) = 62
FEATURE [PartDesign::Pad] Pad014
  BaseFeature = -> PolarPattern001
  Direction = (0,0,1)
  Length = 42
  Length2 = 10
  Profile = -> Sketch039
  ReferenceAxis = -> Sketch039 [N_Axis]
  Reversed = true
  Suppressed = false
  Type = 0
FEATURE [Sketcher::SketchObject] Sketch040
  AttachmentOffset = pos=(0,0,-0.1) rot=(0,0,1;0rad)
  FullyConstrained = true
  MapMode = 5
  Placement = pos=(0,0,29.9) rot=(0,0,1;0rad)
  sketch-geometry (1):
    g0: Circle CenterX=0 CenterY=0 CenterZ=0 NormalX=0 NormalY=0 NormalZ=1 AngleXU=0 Radius=22.5
  constraints (2):
    c: Coincident(g0,g-1)
    c: Diameter(g0) = 45
FEATURE [PartDesign::Pad] Pad015
  BaseFeature = -> Pad014
  Direction = (0,0,1)
  Length = 105
  Length2 = 10
  Profile = -> Sketch040
  ReferenceAxis = -> Sketch040 [N_Axis]
  Reversed = true
  Suppressed = false
  Type = 0
FEATURE [Sketcher::SketchObject] Sketch041
  FullyConstrained = true
  MapMode = 5
  Placement = pos=(0,0,-75.1) rot=(1,0,0;3.14159rad)
  sketch-geometry (1):
    g0: Circle CenterX=0 CenterY=0 CenterZ=0 NormalX=0 NormalY=0 NormalZ=1 AngleXU=0 Radius=13.5
  constraints (2):
    c: Coincident(g0,g-1)
    c: Diameter(g0) = 27
FEATURE [PartDesign::Pocket] Pocket025
  BaseFeature = -> Pad015
  Direction = (0,0,1)
  Length = 77
  Length2 = 5
  Profile = -> Sketch041
  ReferenceAxis = -> Sketch041 [N_Axis]
  Suppressed = false
  Type = 0
FEATURE [Sketcher::SketchObject] Sketch042
  FullyConstrained = true
  MapMode = 5
  Placement = pos=(0,0,30) rot=(0,0,1;0rad)
  sketch-geometry (1):
    g0: Circle CenterX=0 CenterY=0 CenterZ=0 NormalX=0 NormalY=0 NormalZ=1 AngleXU=0 Radius=11.75
  constraints (2):
    c: Coincident(g0,g-1)
    c: Diameter(g0) = 23.5
FEATURE [PartDesign::Pocket] Pocket026
  BaseFeature = -> Pocket025
  Direction = (0,0,-1)
  Length = 50
  Length2 = 5
  Profile = -> Sketch042
  ReferenceAxis = -> Sketch042 [N_Axis]
  Suppressed = false
  Type = 0
FEATURE [Sketcher::SketchObject] Sketch043
  FullyConstrained = false
  MapMode = 5
  Placement = pos=(0,0,30) rot=(0,0,1;0rad)
  sketch-geometry (4):
    g0: ArcOfCircle CenterX=35 CenterY=35 CenterZ=0 NormalX=0 NormalY=0 NormalZ=1 AngleXU=0 Radius=7.5 StartAngle=2.35619 EndAngle=5.49779
    g1: ArcOfCircle CenterX=87.3259 CenterY=87.3259 CenterZ=0 NormalX=0 NormalY=0 NormalZ=1 AngleXU=0 Radius=7.5 StartAngle=5.49779 EndAngle=8.63938
    g2: LineSegment StartX=40.3033 StartY=29.6967 StartZ=0 EndX=92.6292 EndY=82.0226 EndZ=0
    g3: LineSegment StartX=82.0226 StartY=92.6292 StartZ=0 EndX=29.6967 EndY=40.3033 EndZ=0
  constraints (9):
    c: Tangent(g0,g2) = -1.5708
    c: Tangent(g2,g1) = -1.5708
    c: Tangent(g1,g3) = -1.5708
    c: Tangent(g3,g0) = -1.5708
    c: Equal(g0,g1)
    c: Diameter(g0) = 15
    c: Distance(g0,g1) = 74
    c: DistanceX(g-1,g0) = 35
    c: DistanceY(g-1,g0) = 35
FEATURE [PartDesign::Pocket] Pocket027
  BaseFeature = -> Pocket026
  Direction = (0,0,-1)
  Length = 15
  Length2 = 5
  Profile = -> Sketch043
  ReferenceAxis = -> Sketch043 [N_Axis]
  Suppressed = false
  Type = 0
FEATURE [PartDesign::PolarPattern] PolarPattern002
  Angle = 360
  Axis = -> Sketch043 [N_Axis]
  BaseFeature = -> Pocket027
  Mode = 0
  Occurrences = 4
  Offset = 120
  Originals = -> [Pocket027]
  Suppressed = false
FEATURE [PartDesign::Body] Body002  label="iron_table"
  Group = -> [Sketch005,Pad002,Sketch037,Pocket024,PolarPattern,Sketch038,Pad013,PolarPattern001,Sketch039,Pad014,Sketch040,Pad015,Sketch041,Pocket025,Sketch042,Pocket026,Sketch043,Pocket027,PolarPattern002]
  Origin = -> Origin002
  Placement = pos=(0,210,-105) rot=(0,0,1;0rad)
  Tip = -> PolarPattern002
  expr: .Placement.Base.z = -(Spreadsheet.base_height + 30 mm)
FEATURE [Sketcher::SketchObject] Sketch044
  FullyConstrained = true
  MapMode = 5
  expr: Constraints[16] = Spreadsheet.iron_cast_table / 2
  expr: Constraints[17] = Spreadsheet.iron_cast_table / 2
  expr: Constraints[7] = Spreadsheet.iron_cast_table / 2 - 15 mm - 2 mm
  expr: Constraints[8] = Spreadsheet.iron_cast_table / 2 - 15 mm - 2 mm
  sketch-geometry (7):
    g0: GeomPoint X=131 Y=131 Z=0
    g1: LineSegment StartX=5 StartY=5 StartZ=0 EndX=119 EndY=5 EndZ=0
    g2: LineSegment StartX=119 StartY=5 StartZ=0 EndX=119 EndY=81 EndZ=0
    g3: LineSegment StartX=81 StartY=119 StartZ=0 EndX=5 EndY=119 EndZ=0
    g4: LineSegment StartX=5 StartY=119 StartZ=0 EndX=5 EndY=5 EndZ=0
    g5: ArcOfCircle CenterX=81 CenterY=81 CenterZ=0 NormalX=0 NormalY=0 NormalZ=1 AngleXU=0 Radius=38 StartAngle=8e-16 EndAngle=1.5708
    g6: GeomPoint X=119 Y=119 Z=0
  constraints (18):
    c: Coincident(g1,g2)
    c: Coincident(g3,g4)
    c: Coincident(g4,g1)
    c: Horizontal(g1)
    c: Horizontal(g3)
    c: Vertical(g2)
    c: Vertical(g4)
    c: DistanceY(g4,g4) = 114
    c: DistanceX(g1,g1) = 114
    c: PointOnObject(g6,g3)
    c: PointOnObject(g6,g2)
    c: Tangent(g3,g5) = -1.5708
    c: Tangent(g2,g5) = -1.5708
    c: Radius(g5) = 38
    c: DistanceX(g-1,g1) = 5
    c: DistanceY(g-1,g1) = 5
    c: DistanceY(g0) = 131
    c: DistanceX(g0) = 131
FEATURE [PartDesign::Pad] Pad016
  Direction = (0,0,1)
  Length = 24
  Length2 = 10
  Profile = -> Sketch044
  ReferenceAxis = -> Sketch044 [N_Axis]
  Suppressed = false
  Type = 0
  expr: Length = 2 * Spreadsheet.ply_12
FEATURE [Sketcher::SketchObject] Sketch045
  FullyConstrained = false
  MapMode = 5
  Placement = pos=(0,0,0) rot=(1,0,0;3.14159rad)
  sketch-geometry (5):
    g0: LineSegment StartX=12.3744 StartY=12.3744 StartZ=0 EndX=123.206 EndY=-98.4574 EndZ=0
    g1: LineSegment StartX=-12.3744 StartY=-12.3744 StartZ=0 EndX=98.4574 EndY=-123.206 EndZ=0
    g2: LineSegment StartX=0 StartY=0 StartZ=0 EndX=12.3744 EndY=12.3744 EndZ=0
    g3: LineSegment StartX=0 StartY=0 StartZ=0 EndX=-12.3744 EndY=-12.3744 EndZ=0
    g4: LineSegment StartX=98.4574 StartY=-123.206 StartZ=0 EndX=123.206 EndY=-98.4574 EndZ=0
  constraints (6):
    c: Perpendicular(g2,g0) = 4.71239
    c: Perpendicular(g3,g1) = 1.5708
    c: Coincident(g0,g4)
    c: Coincident(g4,g1)
    c: Distance(g-1,g0) = 17.5
    c: Distance(g1,g-1) = 17.5
FEATURE [PartDesign::Pocket] Pocket028
  BaseFeature = -> Pad016
  Direction = (0,0,1)
  Length = 5
  Length2 = 5
  Profile = -> Sketch045
  ReferenceAxis = -> Sketch045 [N_Axis]
  Suppressed = false
  Type = 0
FEATURE [Sketcher::SketchObject] Sketch046
  FullyConstrained = true
  MapMode = 5
  Placement = pos=(0,0,24) rot=(0,0,1;0rad)
  expr: Constraints[2] = 12 mm
  expr: Constraints[3] = Spreadsheet.mounting_screws_distance / 2
  expr: Constraints[4] = Spreadsheet.mounting_screws_distance / 2
  sketch-geometry (2):
    g0: Circle CenterX=0 CenterY=0 CenterZ=0 NormalX=0 NormalY=0 NormalZ=1 AngleXU=0 Radius=32
    g1: Circle CenterX=85 CenterY=85 CenterZ=0 NormalX=0 NormalY=0 NormalZ=1 AngleXU=0 Radius=6
  constraints (5):
    c: Coincident(g0,g-1)
    c: Diameter(g0) = 64
    c: Diameter(g1) = 12
    c: DistanceX(g0,g1) = 85
    c: DistanceY(g0,g1) = 85
FEATURE [PartDesign::Pocket] Pocket029
  BaseFeature = -> Pocket028
  Direction = (0,0,-1)
  Length = 24
  Length2 = 5
  Profile = -> Sketch046
  ReferenceAxis = -> Sketch046 [N_Axis]
  Suppressed = false
  Type = 0
FEATURE [PartDesign::Body] Body014  label="iron_table_insert"
  Group = -> [Sketch044,Pad016,Sketch045,Pocket028,Sketch046,Pocket029]
  Origin = -> Origin018
  Placement = pos=(0,210,-90) rot=(1,0,0;3.14159rad)
  Tip = -> Pocket029
FEATURE [Sketcher::SketchObject] Sketch047
  FullyConstrained = true
  MapMode = 5
  expr: Constraints[10] = Spreadsheet.drawer_total_height
  expr: Constraints[9] = Spreadsheet.drawer_total_width - 2 * (Spreadsheet.ply_12 - Spreadsheet.ply_3)
  sketch-geometry (4):
    g0: LineSegment StartX=-91.3 StartY=48 StartZ=0 EndX=91.3 EndY=48 EndZ=0
    g1: LineSegment StartX=91.3 StartY=48 StartZ=0 EndX=91.3 EndY=0 EndZ=0
    g2: LineSegment StartX=91.3 StartY=0 StartZ=0 EndX=-91.3 EndY=0 EndZ=0
    g3: LineSegment StartX=-91.3 StartY=0 StartZ=0 EndX=-91.3 EndY=48 EndZ=0
  constraints (11):
    c: Coincident(g0,g1)
    c: Coincident(g1,g2)
    c: Coincident(g2,g3)
    c: Coincident(g3,g0)
    c: Horizontal(g0)
    c: Horizontal(g2)
    c: Vertical(g1)
    c: Vertical(g3)
    c: Symmetric(g2,g1,g-1)
    c: DistanceX(g0,g0) = 182.6
    c: DistanceY(g3,g3) = 48
FEATURE [PartDesign::Pad] Pad017
  Direction = (0,0,1)
  Length = 12
  Length2 = 10
  Profile = -> Sketch047
  ReferenceAxis = -> Sketch047 [N_Axis]
  Suppressed = false
  Type = 0
  expr: Length = Spreadsheet.ply_12
FEATURE [Sketcher::SketchObject] Sketch048
  FullyConstrained = true
  MapMode = 5
  Placement = pos=(0,0,12) rot=(0,0,1;0rad)
  expr: Constraints[10] = (Spreadsheet.drawer_total_width - 2 * (Spreadsheet.ply_12 - Spreadsheet.ply_3)) / 2
  expr: Constraints[11] = Spreadsheet.ply_3
  expr: Constraints[9] = Spreadsheet.drawer_total_height
  sketch-geometry (4):
    g0: LineSegment StartX=-91.3 StartY=48 StartZ=0 EndX=-88.3 EndY=48 EndZ=0
    g1: LineSegment StartX=-88.3 StartY=48 StartZ=0 EndX=-88.3 EndY=0 EndZ=0
    g2: LineSegment StartX=-88.3 StartY=0 StartZ=0 EndX=-91.3 EndY=0 EndZ=0
    g3: LineSegment StartX=-91.3 StartY=0 StartZ=0 EndX=-91.3 EndY=48 EndZ=0
  constraints (12):
    c: Coincident(g0,g1)
    c: Coincident(g1,g2)
    c: Coincident(g2,g3)
    c: Coincident(g3,g0)
    c: Horizontal(g0)
    c: Horizontal(g2)
    c: Vertical(g1)
    c: Vertical(g3)
    c: PointOnObject(g1,g-1)
    c: DistanceY(g3,g3) = 48
    c: DistanceX(g2,g-1) = 91.3
    c: DistanceX(g0,g0) = 3
FEATURE [PartDesign::Pocket] Pocket030
  BaseFeature = -> Pad017
  Direction = (0,0,-1)
  Length = 9
  Length2 = 5
  Profile = -> Sketch048
  ReferenceAxis = -> Sketch048 [N_Axis]
  Suppressed = false
  Type = 0
  expr: Length = Spreadsheet.ply_12 - Spreadsheet.ply_3
FEATURE [PartDesign::Mirrored] Mirrored002
  BaseFeature = -> Pocket030
  MirrorPlane = -> Sketch048 [V_Axis]
  Originals = -> [Pocket030]
  Suppressed = false
FEATURE [Sketcher::SketchObject] Sketch049
  FullyConstrained = true
  MapMode = 5
  Placement = pos=(0,0,0) rot=(1,0,0;3.14159rad)
  expr: Constraints[10] = <<Spreadsheet>>.ply_3
  expr: Constraints[11] = (Spreadsheet.drawer_total_width - 2 * (Spreadsheet.ply_12 - Spreadsheet.ply_3)) / 2
  expr: Constraints[8] = Spreadsheet.ply_3
  expr: Constraints[9] = (Spreadsheet.drawer_total_width - 2 * (Spreadsheet.ply_12 - Spreadsheet.ply_3)) / 2
  sketch-geometry (4):
    g0: LineSegment StartX=-91.3 StartY=-3 StartZ=0 EndX=91.3 EndY=-3 EndZ=0
    g1: LineSegment StartX=91.3 StartY=-3 StartZ=0 EndX=91.3 EndY=-6 EndZ=0
    g2: LineSegment StartX=91.3 StartY=-6 StartZ=0 EndX=-91.3 EndY=-6 EndZ=0
    g3: LineSegment StartX=-91.3 StartY=-6 StartZ=0 EndX=-91.3 EndY=-3 EndZ=0
  constraints (12):
    c: Coincident(g0,g1)
    c: Coincident(g1,g2)
    c: Coincident(g2,g3)
    c: Coincident(g3,g0)
    c: Horizontal(g0)
    c: Horizontal(g2)
    c: Vertical(g1)
    c: Vertical(g3)
    c: DistanceY(g3,g3) = 3
    c: DistanceX(g0,g-1) = 91.3
    c: DistanceY(g0,g-1) = 3
    c: DistanceX(g-1,g0) = 91.3
FEATURE [PartDesign::Pocket] Pocket031
  BaseFeature = -> Mirrored002
  Direction = (0,0,1)
  Length = 3
  Length2 = 5
  Profile = -> Sketch049
  ReferenceAxis = -> Sketch049 [N_Axis]
  Suppressed = false
  Type = 0
  expr: Length = Spreadsheet.ply_3
FEATURE [Sketcher::SketchObject] Sketch050
  FullyConstrained = true
  MapMode = 5
  expr: Constraints[10] = Spreadsheet.drawer_total_height
  expr: Constraints[9] = Spreadsheet.drawer_total_depth
  sketch-geometry (4):
    g0: LineSegment StartX=-103 StartY=48 StartZ=0 EndX=103 EndY=48 EndZ=0
    g1: LineSegment StartX=103 StartY=48 StartZ=0 EndX=103 EndY=0 EndZ=0
    g2: LineSegment StartX=103 StartY=0 StartZ=0 EndX=-103 EndY=0 EndZ=0
    g3: LineSegment StartX=-103 StartY=0 StartZ=0 EndX=-103 EndY=48 EndZ=0
  constraints (11):
    c: Coincident(g0,g1)
    c: Coincident(g1,g2)
    c: Coincident(g2,g3)
    c: Coincident(g3,g0)
    c: Horizontal(g0)
    c: Horizontal(g2)
    c: Vertical(g1)
    c: Vertical(g3)
    c: Symmetric(g2,g1,g-1)
    c: DistanceX(g2,g2) = 206
    c: DistanceY(g3,g3) = 48
FEATURE [PartDesign::Pad] Pad018
  Direction = (0,0,1)
  Length = 12
  Length2 = 10
  Profile = -> Sketch050
  ReferenceAxis = -> Sketch050 [N_Axis]
  Suppressed = false
  Type = 0
  expr: Length = Spreadsheet.ply_12
FEATURE [Sketcher::SketchObject] Sketch051
  FullyConstrained = true
  MapMode = 5
  Placement = pos=(0,0,12) rot=(0,0,1;0rad)
  expr: Constraints[24] = Spreadsheet.ply_3
  expr: Constraints[27] = Spreadsheet.drawer_total_height
  expr: Constraints[30] = Spreadsheet.drawer_total_depth / 2 - Spreadsheet.ply_12
  expr: Constraints[31] = Spreadsheet.ply_3
  expr: Constraints[32] = Spreadsheet.ply_3
  expr: Constraints[33] = Spreadsheet.drawer_total_depth
  expr: Constraints[34] = Spreadsheet.drawer_total_depth / 2
  sketch-geometry (12):
    g0: LineSegment StartX=-103 StartY=6 StartZ=0 EndX=103 EndY=6 EndZ=0
    g1: LineSegment StartX=103 StartY=6 StartZ=0 EndX=103 EndY=3 EndZ=0
    g2: LineSegment StartX=103 StartY=3 StartZ=0 EndX=-103 EndY=3 EndZ=0
    g3: LineSegment StartX=-103 StartY=3 StartZ=0 EndX=-103 EndY=6 EndZ=0
    g4: LineSegment StartX=-94 StartY=48 StartZ=0 EndX=-91 EndY=48 EndZ=0
    g5: LineSegment StartX=-91 StartY=48 StartZ=0 EndX=-91 EndY=0 EndZ=0
    g6: LineSegment StartX=-91 StartY=0 StartZ=0 EndX=-94 EndY=0 EndZ=0
    g7: LineSegment StartX=-94 StartY=0 StartZ=0 EndX=-94 EndY=48 EndZ=0
    g8: LineSegment StartX=91 StartY=48 StartZ=0 EndX=94 EndY=48 EndZ=0
    g9: LineSegment StartX=94 StartY=48 StartZ=0 EndX=94 EndY=0 EndZ=0
    g10: LineSegment StartX=94 StartY=0 StartZ=0 EndX=91 EndY=0 EndZ=0
    g11: LineSegment StartX=91 StartY=0 StartZ=0 EndX=91 EndY=48 EndZ=0
  constraints (35):
    c: Coincident(g0,g1)
    c: Coincident(g1,g2)
    c: Coincident(g2,g3)
    c: Coincident(g3,g0)
    c: Horizontal(g0)
    c: Horizontal(g2)
    c: Vertical(g1)
    c: Vertical(g3)
    c: Coincident(g4,g5)
    c: Coincident(g5,g6)
    c: Coincident(g6,g7)
    c: Coincident(g7,g4)
    c: Horizontal(g4)
    c: Horizontal(g6)
    c: Vertical(g5)
    c: Vertical(g7)
    c: Coincident(g8,g9)
    c: Coincident(g9,g10)
    c: Coincident(g10,g11)
    c: Coincident(g11,g8)
    c: Horizontal(g8)
    c: Horizontal(g10)
    c: Vertical(g9)
    c: Vertical(g11)
    c: DistanceX(g4,g4) = 3
    c: Equal(g4,g8)
    c: DistanceY(g5,g-1) = 0
    c: DistanceY(g7,g7) = 48
    c: Equal(g5,g11)
    c: Symmetric(g10,g5,g-1)
    c: DistanceX(g5,g-1) = 91
    c: DistanceY(g3,g3) = 3
    c: DistanceY(g-1,g2) = 3
    c: DistanceX(g0,g0) = 206
    c: DistanceX(g2,g-1) = 103
FEATURE [PartDesign::Pocket] Pocket032
  BaseFeature = -> Pad018
  Direction = (0,0,-1)
  Length = 3
  Length2 = 5
  Profile = -> Sketch051
  ReferenceAxis = -> Sketch051 [N_Axis]
  Suppressed = false
  Type = 0
  expr: Length = Spreadsheet.ply_3
FEATURE [PartDesign::Body] Body016  label="drawer_left_side"
  Group = -> [Sketch050,Pad018,Sketch051,Pocket032]
  Origin = -> Origin020
  Placement = pos=(-100.3,103,0) rot=(0.57735,0.57735,0.57735;2.0944rad)
  Tip = -> Pocket032
  expr: .Placement.Base.x = -Spreadsheet.drawer_total_width / 2
  expr: .Placement.Base.y = Spreadsheet.drawer_total_depth / 2
FEATURE [PartDesign::FeatureBase] Clone001
  BaseFeature = -> Body016
  Placement = pos=(-100.3,103,0) rot=(0.57735,0.57735,0.57735;2.0944rad)
  Suppressed = false
FEATURE [PartDesign::Body] Body017  label="drawer_right_side"
  Group = -> [Clone001]
  Origin = -> Origin021
  Placement = pos=(0,206,0) rot=(0,0,1;3.14159rad)
  Tip = -> Clone001
  expr: .Placement.Base.y = Spreadsheet.drawer_total_depth
FEATURE [Sketcher::SketchObject] Sketch052
  FullyConstrained = true
  MapMode = 5
  expr: Constraints[10] = Spreadsheet.drawer_total_depth - 2 * (Spreadsheet.ply_12 - Spreadsheet.ply_3)
  expr: Constraints[9] = Spreadsheet.drawer_total_width - 2 * (Spreadsheet.ply_12 - Spreadsheet.ply_3)
  sketch-geometry (4):
    g0: LineSegment StartX=-91.3 StartY=188 StartZ=0 EndX=91.3 EndY=188 EndZ=0
    g1: LineSegment StartX=91.3 StartY=188 StartZ=0 EndX=91.3 EndY=0 EndZ=0
    g2: LineSegment StartX=91.3 StartY=0 StartZ=0 EndX=-91.3 EndY=0 EndZ=0
    g3: LineSegment StartX=-91.3 StartY=0 StartZ=0 EndX=-91.3 EndY=188 EndZ=0
  constraints (11):
    c: Coincident(g0,g1)
    c: Coincident(g1,g2)
    c: Coincident(g2,g3)
    c: Coincident(g3,g0)
    c: Horizontal(g0)
    c: Horizontal(g2)
    c: Vertical(g1)
    c: Vertical(g3)
    c: Symmetric(g2,g1,g-1)
    c: DistanceX(g0,g0) = 182.6
    c: DistanceY(g1,g1) = 188
FEATURE [PartDesign::Pad] Pad019
  Direction = (0,0,1)
  Length = 3
  Length2 = 10
  Profile = -> Sketch052
  ReferenceAxis = -> Sketch052 [N_Axis]
  Suppressed = false
  Type = 0
  expr: Length = Spreadsheet.ply_3
FEATURE [PartDesign::Body] Body019  label="drawer_bottom"
  Group = -> [Sketch052,Pad019]
  Origin = -> Origin023
  Placement = pos=(0,9,3) rot=(0,0,1;0rad)
  Tip = -> Pad019
  expr: .Placement.Base.y = Spreadsheet.ply_12 - Spreadsheet.ply_3
  expr: .Placement.Base.z = Spreadsheet.ply_3
FEATURE [Sketcher::SketchObject] Sketch053
  FullyConstrained = true
  MapMode = 5
  expr: Constraints[10] = Spreadsheet.base_width
  expr: Constraints[9] = Spreadsheet.base_height - Spreadsheet.ply_3
  sketch-geometry (4):
    g0: LineSegment StartX=-131 StartY=72 StartZ=0 EndX=131 EndY=72 EndZ=0
    g1: LineSegment StartX=131 StartY=72 StartZ=0 EndX=131 EndY=0 EndZ=0
    g2: LineSegment StartX=131 StartY=0 StartZ=0 EndX=-131 EndY=0 EndZ=0
    g3: LineSegment StartX=-131 StartY=0 StartZ=0 EndX=-131 EndY=72 EndZ=0
  constraints (11):
    c: Coincident(g0,g1)
    c: Coincident(g1,g2)
    c: Coincident(g2,g3)
    c: Coincident(g3,g0)
    c: Horizontal(g0)
    c: Horizontal(g2)
    c: Vertical(g1)
    c: Vertical(g3)
    c: Symmetric(g2,g1,g-1)
    c: DistanceY(g3,g3) = 72
    c: DistanceX(g0,g0) = 262
FEATURE [PartDesign::Pad] Pad020
  Direction = (0,0,1)
  Length = 18
  Length2 = 10
  Profile = -> Sketch053
  ReferenceAxis = -> Sketch053 [N_Axis]
  Suppressed = false
  Type = 0
  expr: Length = Spreadsheet.ply_18
FEATURE [PartDesign::Fillet] Fillet
  Base = -> Pad020 [Edge7,Edge12]
  BaseFeature = -> Pad020
  Radius = 6
  SupportTransform = false
  Suppressed = false
  UseAllEdges = false
  expr: Radius = Spreadsheet.table_radius
FEATURE [PartDesign::Body] Body020  label="drawer_false_front"
  Group = -> [Sketch053,Pad020,Fillet]
  Origin = -> Origin024
  Placement = pos=(0,0,-21) rot=(1,0,0;1.5708rad)
  Tip = -> Fillet
  expr: .Placement.Base.z = -(Spreadsheet.ply_18 + Spreadsheet.ply_3)
FEATURE [Sketcher::SketchObject] Sketch054
  FullyConstrained = true
  MapMode = 5
  Placement = pos=(0,0,12) rot=(0,0,1;0rad)
  expr: Constraints[1] = Spreadsheet.drawer_total_height / 2
  sketch-geometry (1):
    g0: Circle CenterX=-70 CenterY=24 CenterZ=0 NormalX=0 NormalY=0 NormalZ=1 AngleXU=0 Radius=1.5
  constraints (3):
    c: DistanceX(g0,g-1) = 70
    c: DistanceY(g-1,g0) = 24
    c: Diameter(g0) = 3
FEATURE [PartDesign::Pocket] Pocket033
  BaseFeature = -> Pocket031
  Direction = (0,0,-1)
  Length = 12
  Length2 = 5
  Profile = -> Sketch054
  ReferenceAxis = -> Sketch054 [N_Axis]
  Suppressed = false
  Type = 0
  expr: Length = Spreadsheet.ply_12
FEATURE [PartDesign::Mirrored] Mirrored003
  BaseFeature = -> Pocket033
  MirrorPlane = -> Sketch054 [V_Axis]
  Originals = -> [Pocket033]
  Suppressed = false
FEATURE [PartDesign::Body] Body015  label="drawer_front"
  Group = -> [Sketch047,Pad017,Sketch048,Pocket030,Mirrored002,Sketch049,Pocket031,Sketch054,Pocket033,Mirrored003]
  Origin = -> Origin019
  Placement = pos=(0,12,0) rot=(1,0,0;1.5708rad)
  Tip = -> Mirrored003
  expr: .Placement.Base.y = Spreadsheet.ply_12
FEATURE [PartDesign::FeatureBase] Clone002
  BaseFeature = -> Body015
  Placement = pos=(0,12,0) rot=(1,0,0;1.5708rad)
  Suppressed = false
FEATURE [PartDesign::Body] Body018  label="drawer_back"
  Group = -> [Clone002]
  Origin = -> Origin022
  Placement = pos=(0,206,0) rot=(0,0,1;3.14159rad)
  Tip = -> Clone002
  expr: .Placement.Base.y = Spreadsheet.drawer_total_depth
FEATURE [App::Part] Part003  label="drawer"
  Group = -> [Body015,Body016,Body017,Body018,Body019,Body020]
  Origin = -> Origin012
  Placement = pos=(0,62,-54) rot=(0,0,1;0rad)
  expr: .Placement.Base.y = Spreadsheet.ply_12 + 50 mm
  expr: .Placement.Base.z = -Spreadsheet.drawer_total_height - 2 * Spreadsheet.ply_3
FEATURE [Sketcher::SketchObject] Sketch055
  FullyConstrained = true
  MapMode = 5
  Placement = pos=(0,0,12) rot=(0,0,1;0rad)
  expr: Constraints[2] = 3 / 4 * Spreadsheet.insert_depth / 2
  sketch-geometry (1):
    g0: Circle CenterX=0 CenterY=-75 CenterZ=0 NormalX=0 NormalY=0 NormalZ=1 AngleXU=0 Radius=12
  constraints (3):
    c: PointOnObject(g0,g-2)
    c: Diameter(g0) = 24
    c: DistanceY(g0,g-1) = 75
FEATURE [PartDesign::Pocket] Pocket034
  BaseFeature = -> Pad003
  Direction = (0,0,-1)
  Length = 12
  Length2 = 5
  Profile = -> Sketch055
  ReferenceAxis = -> Sketch055 [N_Axis]
  Suppressed = false
  Type = 0
  expr: Length = Spreadsheet.ply_12
FEATURE [PartDesign::Body] Body003  label="insert"
  Group = -> [Sketch008,Pad003,Sketch055,Pocket034]
  Origin = -> Origin003
  Placement = pos=(0,230,24) rot=(0,0,1;0rad)
  Tip = -> Pocket034
  expr: .Placement.Base.y = 130 mm + Spreadsheet.insert_depth / 2
  expr: .Placement.Base.z = 2 * Spreadsheet.ply_18 - Spreadsheet.ply_12
FEATURE [TechDraw::DrawSVGTemplate] Template
  EditableTexts = AUTHOR_NAME=Grzegorz Sapijaszko; DN=DN; DRAWING_TITLE=Table: upper part; FC-DATE=DD/MM/YYYY; FC-REV=REV A; FC-SC=SCALE; FC-SH=X / Y; FC-SI=A3; FreeCAD_DRAWING=Licence: CERN-OHL-P; PN=PN
  Height = 297
  Orientation = 1
  Template = <userpath>/.local/share/FreeCAD/Mod/TechDraw/Templates/gs_A3_Landscape_ISO7200_OSH.svg
  Width = 420
FEATURE [Sketcher::SketchObject] Sketch056
  FullyConstrained = false
  MapMode = 5
  Placement = pos=(0,0,18) rot=(0,0,1;0rad)
  sketch-geometry (1):
    g0: LineSegment StartX=-69.7516 StartY=178.869 StartZ=0 EndX=66.5593 EndY=178.869 EndZ=0
  constraints (1):
    c: Horizontal(g0)
FEATURE [PartDesign::Body] Body001  label="upper_part"
  Group = -> [Sketch002,Pad001,Sketch003,Pocket001,Sketch004,Pocket002,Sketch007,Pocket004,Sketch056]
  Origin = -> Origin001
  Placement = pos=(0,0,18) rot=(0,0,1;0rad)
  Tip = -> Pocket004
  expr: .Placement.Base.z = Spreadsheet.ply_18
FEATURE [TechDraw::DrawProjGroupItem] ProjItem  label="Front"
  CoarseView = false
  Direction = (0,0,1)
  Focus = 100
  HardHidden = false
  IsoCount = 0
  IsoHidden = false
  IsoVisible = false
  LockPosition = true
  Perspective = false
  Rotation = 0
  RotationVector = (1,0,0)
  Scale = 0.25
  ScaleType = 2
  ScrubCount = 0
  SeamHidden = false
  SeamVisible = false
  SmoothHidden = false
  SmoothVisible = true
  Source = -> [Body001]
  Type = 0
  X = 0
  XDirection = (1,0,0)
  Y = 0
FEATURE [TechDraw::DrawProjGroup] ProjGroup
  Anchor = -> ProjItem
  AutoDistribute = true
  LockPosition = false
  ProjectionType = 0
  Rotation = 0
  Scale = 0.25
  ScaleType = 2
  Source = -> [Body001]
  Views = -> [ProjItem]
  X = 250
  Y = 200
  spacingX = 15
  spacingY = 30
FEATURE [TechDraw::DrawViewDimension] Dimension003
  AngleOverride = false
  Arbitrary = false
  ArbitraryTolerances = false
  BoxCorners = (2) [(-90,-52.5,0),(90,52.5,0)]
  EqualTolerance = true
  ExtensionAngle = 0
  FormatSpec = %.2w
  FormatSpecOverTolerance = %+.2w
  FormatSpecUnderTolerance = %+.2w
  Inverted = false
  LineAngle = 0
  LockPosition = false
  MeasureType = 1
  OverTolerance = 0
  References2D = -> [ProjItem]
  Rotation = 0
  ScaleType = 0
  TheoreticalExact = false
  Type = 1
  UnderTolerance = 0
  X = -0.198453
  Y = 68.9909
FEATURE [TechDraw::DrawViewDimension] Dimension004
  AngleOverride = false
  Arbitrary = false
  ArbitraryTolerances = false
  BoxCorners = (2) [(-90,-52.5,0),(90,52.5,0)]
  EqualTolerance = true
  ExtensionAngle = 0
  FormatSpec = %.2w
  FormatSpecOverTolerance = %+.2w
  FormatSpecUnderTolerance = %+.2w
  Inverted = false
  LineAngle = 0
  LockPosition = false
  MeasureType = 1
  OverTolerance = 0
  References2D = -> [ProjItem]
  Rotation = 0
  ScaleType = 0
  TheoreticalExact = false
  Type = 2
  UnderTolerance = 0
  X = 100.615
  Y = 3.80145
FEATURE [TechDraw::DrawViewDimension] Dimension005
  AngleOverride = false
  Arbitrary = false
  ArbitraryTolerances = false
  EqualTolerance = true
  ExtensionAngle = 0
  FormatSpec = R%.2w
  FormatSpecOverTolerance = %+.2w
  FormatSpecUnderTolerance = %+.2w
  Inverted = false
  LineAngle = 0
  LockPosition = false
  MeasureType = 1
  OverTolerance = 0
  References2D = -> [ProjItem]
  Rotation = 0
  ScaleType = 0
  TheoreticalExact = false
  Type = 4
  UnderTolerance = 0
  X = 82.1515
  Y = -38.7352
FEATURE [TechDraw::DrawViewDimension] Dimension009
  AngleOverride = false
  Arbitrary = false
  ArbitraryTolerances = false
  BoxCorners = (2) [(-90,-52.5,0),(90,52.5,0)]
  EqualTolerance = true
  ExtensionAngle = 0
  FormatSpec = %.2w
  FormatSpecOverTolerance = %+.2w
  FormatSpecUnderTolerance = %+.2w
  Inverted = false
  LineAngle = 0
  LockPosition = false
  MeasureType = 1
  OverTolerance = 0
  References2D = -> [ProjItem]
  Rotation = 0
  ScaleType = 0
  TheoreticalExact = false
  Type = 2
  UnderTolerance = 0
  X = -98.6478
  Y = 36.6596
FEATURE [TechDraw::DrawViewDimension] Dimension010
  AngleOverride = false
  Arbitrary = false
  ArbitraryTolerances = false
  EqualTolerance = true
  ExtensionAngle = 0
  FormatSpec = R%.2w
  FormatSpecOverTolerance = %+.2w
  FormatSpecUnderTolerance = %+.2w
  Inverted = false
  LineAngle = 0
  LockPosition = false
  MeasureType = 1
  OverTolerance = 0
  References2D = -> [ProjItem]
  Rotation = 0
  ScaleType = 0
  TheoreticalExact = false
  Type = 4
  UnderTolerance = 0
  X = -61.9273
  Y = 27.1144
FEATURE [TechDraw::DrawViewDimension] Dimension012
  AngleOverride = false
  Arbitrary = false
  ArbitraryTolerances = false
  BoxCorners = (2) [(-90,-52.5,0),(90,52.5,0)]
  EqualTolerance = true
  ExtensionAngle = 0
  FormatSpec = %.2w
  FormatSpecOverTolerance = %+.2w
  FormatSpecUnderTolerance = %+.2w
  Inverted = false
  LineAngle = 0
  LockPosition = false
  MeasureType = 1
  OverTolerance = 0
  References2D = -> [ProjItem]
  Rotation = 0
  ScaleType = 0
  TheoreticalExact = false
  Type = 1
  UnderTolerance = 0
  X = 14.0326
  Y = 24.0761
FEATURE [TechDraw::DrawViewDimension] Dimension013
  AngleOverride = false
  Arbitrary = false
  ArbitraryTolerances = false
  BoxCorners = (2) [(-90,-52.5,0),(90,52.5,0)]
  EqualTolerance = true
  ExtensionAngle = 0
  FormatSpec = %.2w
  FormatSpecOverTolerance = %+.2w
  FormatSpecUnderTolerance = %+.2w
  Inverted = false
  LineAngle = 0
  LockPosition = false
  MeasureType = 1
  OverTolerance = 0
  References2D = -> [ProjItem]
  Rotation = 0
  ScaleType = 0
  TheoreticalExact = false
  Type = 2
  UnderTolerance = 0
  X = -19.3241
  Y = 7.5
FEATURE [TechDraw::DrawViewDimension] Dimension014
  AngleOverride = false
  Arbitrary = false
  ArbitraryTolerances = false
  BoxCorners = (2) [(-90,-52.5,0),(90,52.5,0)]
  EqualTolerance = true
  ExtensionAngle = 0
  FormatSpec = %.2w
  FormatSpecOverTolerance = %+.2w
  FormatSpecUnderTolerance = %+.2w
  Inverted = false
  LineAngle = 0
  LockPosition = false
  MeasureType = 1
  OverTolerance = 0
  References2D = -> [ProjItem]
  Rotation = 0
  ScaleType = 0
  TheoreticalExact = false
  Type = 2
  UnderTolerance = 0
  X = -19.3241
  Y = 43.75
FEATURE [TechDraw::DrawViewDimension] Dimension015
  AngleOverride = false
  Arbitrary = false
  ArbitraryTolerances = false
  BoxCorners = (2) [(-90,-52.5,0),(90,52.5,0)]
  EqualTolerance = true
  ExtensionAngle = 0
  FormatSpec = %.2w
  FormatSpecOverTolerance = %+.2w
  FormatSpecUnderTolerance = %+.2w
  Inverted = false
  LineAngle = 0
  LockPosition = false
  MeasureType = 1
  OverTolerance = 0
  References2D = -> [ProjItem]
  Rotation = 0
  ScaleType = 0
  TheoreticalExact = false
  Type = 1
  UnderTolerance = 0
  X = -0.500054
  Y = -20.0678
FEATURE [TechDraw::DrawViewDimension] Dimension016
  AngleOverride = false
  Arbitrary = false
  ArbitraryTolerances = false
  EqualTolerance = true
  ExtensionAngle = 0
  FormatSpec = R%.2w
  FormatSpecOverTolerance = %+.2w
  FormatSpecUnderTolerance = %+.2w
  Inverted = false
  LineAngle = 0
  LockPosition = false
  MeasureType = 1
  OverTolerance = 0
  References2D = -> [ProjItem]
  Rotation = 0
  ScaleType = 0
  TheoreticalExact = false
  Type = 4
  UnderTolerance = 0
  X = -2.20579
  Y = -2.97949
FEATURE [TechDraw::DrawComplexSection] ComplexSection  label="Section A - A"
  BaseView = -> ProjItem
  CoarseView = false
  CutSurfaceDisplay = 2
  CuttingToolWireObject = -> Sketch056
  Direction = (1e-16,-1,0)
  FileGeomPattern = <path>
  FileHatchPattern = <path>
  Focus = 100
  FuseBeforeCut = false
  HardHidden = false
  HatchOffset = (0,0,0)
  HatchRotation = 0
  HatchScale = 1
  IsoCount = 0
  IsoHidden = false
  IsoVisible = false
  LockPosition = false
  NameGeomPattern = Diamond
  Perspective = false
  ProjectionStrategy = 0
  Rotation = 0
  Scale = 0.25
  ScaleType = 2
  ScrubCount = 0
  SeamHidden = false
  SeamVisible = false
  SectionDirection = 4
  SectionLineStretch = 1
  SectionNormal = (1e-16,-1,0)
  SectionOrigin = (0,0,0)
  SectionSymbol = A
  SmoothHidden = false
  SmoothVisible = true
  Source = -> [Body001]
  TrimAfterCut = false
  UsePreviousCut = false
  X = 249.76
  XDirection = (1,1e-16,0)
  Y = 97.6047
FEATURE [TechDraw::DrawViewDimension] Dimension017
  AngleOverride = false
  Arbitrary = false
  ArbitraryTolerances = false
  BoxCorners = (2) [(-90,-2.25,-1e-07),(90,2.25,1e-07)]
  EqualTolerance = true
  ExtensionAngle = 0
  FormatSpec = %.2w
  FormatSpecOverTolerance = %+.2w
  FormatSpecUnderTolerance = %+.2w
  Inverted = false
  LineAngle = 0
  LockPosition = false
  MeasureType = 1
  OverTolerance = 0
  References2D = -> [ComplexSection]
  Rotation = 0
  ScaleType = 0
  TheoreticalExact = false
  Type = 2
  UnderTolerance = 0
  X = -8.74784
  Y = 12.3547
FEATURE [TechDraw::DrawViewDimension] Dimension018
  AngleOverride = false
  Arbitrary = false
  ArbitraryTolerances = false
  EqualTolerance = true
  ExtensionAngle = 0
  FormatSpec = %.2w
  FormatSpecOverTolerance = %+.2w
  FormatSpecUnderTolerance = %+.2w
  Inverted = false
  LineAngle = 0
  LockPosition = false
  MeasureType = 1
  OverTolerance = 0
  References2D = -> [ComplexSection]
  Rotation = 0
  ScaleType = 0
  TheoreticalExact = false
  Type = 1
  UnderTolerance = 0
  X = 19.485
  Y = 13.9363
FEATURE [TechDraw::DrawViewDimension] Dimension019
  AngleOverride = false
  Arbitrary = false
  ArbitraryTolerances = false
  EqualTolerance = true
  ExtensionAngle = 0
  FormatSpec = %.2w
  FormatSpecOverTolerance = %+.2w
  FormatSpecUnderTolerance = %+.2w
  Inverted = false
  LineAngle = 0
  LockPosition = false
  MeasureType = 1
  OverTolerance = 0
  References2D = -> [ComplexSection]
  Rotation = 0
  ScaleType = 0
  TheoreticalExact = false
  Type = 2
  UnderTolerance = 0
  X = 32.0009
  Y = 16.3351
FEATURE [TechDraw::DrawViewDimension] Dimension020
  AngleOverride = false
  Arbitrary = false
  ArbitraryTolerances = false
  EqualTolerance = true
  ExtensionAngle = 0
  FormatSpec = %.2w
  FormatSpecOverTolerance = %+.2w
  FormatSpecUnderTolerance = %+.2w
  Inverted = false
  LineAngle = 0
  LockPosition = false
  MeasureType = 1
  OverTolerance = 0
  References2D = -> [ComplexSection]
  Rotation = 0
  ScaleType = 0
  TheoreticalExact = false
  Type = 2
  UnderTolerance = 0
  X = 94.5222
  Y = 11.4009
FEATURE [TechDraw::DrawViewDimension] Dimension
  AngleOverride = false
  Arbitrary = false
  ArbitraryTolerances = false
  BoxCorners = (2) [(-90,-52.5,0),(90,52.5,0)]
  EqualTolerance = true
  ExtensionAngle = 0
  FormatSpec = %.2w
  FormatSpecOverTolerance = %+.2w
  FormatSpecUnderTolerance = %+.2w
  Inverted = false
  LineAngle = 0
  LockPosition = false
  MeasureType = 1
  OverTolerance = 0
  References2D = -> [ProjItem]
  Rotation = 0
  ScaleType = 0
  TheoreticalExact = false
  Type = 1
  UnderTolerance = 0
  X = -81.25
  Y = -56.5229
FEATURE [TechDraw::DrawViewDimension] Dimension021
  AngleOverride = false
  Arbitrary = false
  ArbitraryTolerances = false
  BoxCorners = (2) [(-90,-52.5,0),(90,52.5,0)]
  EqualTolerance = true
  ExtensionAngle = 0
  FormatSpec = %.0w
  FormatSpecOverTolerance = %+.2w
  FormatSpecUnderTolerance = %+.2w
  Inverted = false
  LineAngle = 0
  LockPosition = false
  MeasureType = 1
  OverTolerance = 0
  References2D = -> [ProjItem]
  Rotation = 0
  ScaleType = 0
  TheoreticalExact = false
  Type = 1
  UnderTolerance = 0
  X = -55.2917
  Y = -56.5229
FEATURE [TechDraw::DrawSVGTemplate] Template001
  EditableTexts = AUTHOR_NAME=Grzegorz Sapijaszko; DN=DN; DRAWING_TITLE=Table: bottom part; FC-DATE=DD/MM/YYYY; FC-REV=REV A; FC-SC=SCALE; FC-SH=X / Y; FC-SI=A3; FreeCAD_DRAWING=Licence: CERN-OHL-P; PN=PN
  Height = 297
  Orientation = 1
  Template = <userpath>/.local/share/FreeCAD/Mod/TechDraw/Templates/gs_A3_Landscape_ISO7200_OSH.svg
  Width = 420
FEATURE [TechDraw::DrawViewImage] ActiveView001
  Height = 100
  ImageFile = <userpath>/.cache/FreeCAD/Cache/FreeCAD_Doc_22664915-c8ef-4449-a133-44cb3a97b6c4_5768d8_6051/Page001ActiveView001okMPL8.png
  LockPosition = false
  Rotation = 0
  Scale = 3
  ScaleType = 2
  Width = 100
  X = 69.7264
  Y = 255.981
FEATURE [Sketcher::SketchObject] Sketch057
  FullyConstrained = false
  MapMode = 5
  Placement = pos=(0,0,18) rot=(0,0,1;0rad)
  sketch-geometry (5):
    g0: LineSegment StartX=-382.642 StartY=125 StartZ=0 EndX=-59.7649 EndY=125 EndZ=0
    g1: LineSegment StartX=-59.7649 StartY=204.647 StartZ=0 EndX=-59.7649 EndY=125 EndZ=0
    g2: LineSegment StartX=-59.7649 StartY=204.647 StartZ=0 EndX=60 EndY=204.647 EndZ=0
    g3: LineSegment StartX=60 StartY=204.647 StartZ=0 EndX=60 EndY=125 EndZ=0
    g4: LineSegment StartX=60 StartY=125 StartZ=0 EndX=401.368 EndY=125 EndZ=0
  constraints (6):
    c: Coincident(g1,g0)
    c: Coincident(g2,g1)
    c: Coincident(g3,g2)
    c: Vertical(g3)
    c: Coincident(g4,g3)
    c: Horizontal(g4)
FEATURE [PartDesign::Body] Body  label="bottom_part"
  Group = -> [Sketch,Pad,Sketch001,Pocket,Sketch006,Pocket003,Sketch057]
  Origin = -> Origin
  Tip = -> Pocket003
FEATURE [App::Part] Part  label="table"
  Group = -> [Body,Body001,Body003]
  Origin = -> Origin005
FEATURE [TechDraw::DrawProjGroupItem] ProjItem001  label="Front001"
  CoarseView = false
  Direction = (0,0,1)
  Focus = 100
  HardHidden = false
  IsoCount = 0
  IsoHidden = false
  IsoVisible = false
  LockPosition = true
  Perspective = false
  Rotation = 0
  RotationVector = (1,0,0)
  Scale = 0.25
  ScaleType = 2
  ScrubCount = 0
  SeamHidden = false
  SeamVisible = false
  SmoothHidden = false
  SmoothVisible = true
  Source = -> [Body]
  Type = 0
  X = 0
  XDirection = (1,0,0)
  Y = 0
FEATURE [TechDraw::DrawProjGroup] ProjGroup001
  Anchor = -> ProjItem001
  AutoDistribute = true
  LockPosition = false
  ProjectionType = 0
  Rotation = 0
  Scale = 0.25
  ScaleType = 2
  Source = -> [Body]
  Views = -> [ProjItem001]
  X = 250
  Y = 200
  spacingX = 15
  spacingY = 24
FEATURE [TechDraw::DrawViewDimension] Dimension022
  AngleOverride = false
  Arbitrary = false
  ArbitraryTolerances = false
  BoxCorners = (2) [(-90,-52.5,0),(90,52.5,0)]
  EqualTolerance = true
  ExtensionAngle = 0
  FormatSpec = %.2w
  FormatSpecOverTolerance = %+.2w
  FormatSpecUnderTolerance = %+.2w
  Inverted = false
  LineAngle = 0
  LockPosition = false
  MeasureType = 1
  OverTolerance = 0
  References2D = -> [ProjItem001]
  Rotation = 0
  ScaleType = 0
  TheoreticalExact = false
  Type = 2
  UnderTolerance = 0
  X = -101.61
  Y = 39.375
FEATURE [TechDraw::DrawViewDimension] Dimension023
  AngleOverride = false
  Arbitrary = false
  ArbitraryTolerances = false
  BoxCorners = (2) [(-90,-52.5,0),(90,52.5,0)]
  EqualTolerance = true
  ExtensionAngle = 0
  FormatSpec = %.2w
  FormatSpecOverTolerance = %+.2w
  FormatSpecUnderTolerance = %+.2w
  Inverted = false
  LineAngle = 0
  LockPosition = false
  MeasureType = 1
  OverTolerance = 0
  References2D = -> [ProjItem001]
  Rotation = 0
  ScaleType = 0
  TheoreticalExact = false
  Type = 2
  UnderTolerance = 0
  X = -101.61
  Y = 2.5
FEATURE [TechDraw::DrawViewDimension] Dimension024
  AngleOverride = false
  Arbitrary = false
  ArbitraryTolerances = false
  BoxCorners = (2) [(-90,-52.5,0),(90,52.5,0)]
  EqualTolerance = true
  ExtensionAngle = 0
  FormatSpec = %.2w
  FormatSpecOverTolerance = %+.2w
  FormatSpecUnderTolerance = %+.2w
  Inverted = false
  LineAngle = 0
  LockPosition = false
  MeasureType = 1
  OverTolerance = 0
  References2D = -> [ProjItem001]
  Rotation = 0
  ScaleType = 0
  TheoreticalExact = false
  Type = 1
  UnderTolerance = 0
  X = 0
  Y = 69.1313
FEATURE [TechDraw::DrawViewDimension] Dimension025
  AngleOverride = false
  Arbitrary = false
  ArbitraryTolerances = false
  BoxCorners = (2) [(-90,-52.5,0),(90,52.5,0)]
  EqualTolerance = true
  ExtensionAngle = 0
  FormatSpec = %.2w
  FormatSpecOverTolerance = %+.2w
  FormatSpecUnderTolerance = %+.2w
  Inverted = false
  LineAngle = 0
  LockPosition = false
  MeasureType = 1
  OverTolerance = 0
  References2D = -> [ProjItem001]
  Rotation = 0
  ScaleType = 0
  TheoreticalExact = false
  Type = 1
  UnderTolerance = 0
  X = -55.625
  Y = 69.1313
FEATURE [TechDraw::DrawComplexSection] ComplexSection001  label="Section001 A - A"
  BaseView = -> ProjItem001
  CoarseView = false
  CutSurfaceDisplay = 2
  CuttingToolWireObject = -> Sketch057
  Direction = (1e-16,-1,0)
  FileGeomPattern = <path>
  FileHatchPattern = <path>
  Focus = 100
  FuseBeforeCut = false
  HardHidden = false
  HatchOffset = (0,0,0)
  HatchRotation = 0
  HatchScale = 1
  IsoCount = 0
  IsoHidden = false
  IsoVisible = false
  LockPosition = false
  NameGeomPattern = Diamond
  Perspective = false
  ProjectionStrategy = 0
  Rotation = 0
  Scale = 0.25
  ScaleType = 2
  ScrubCount = 0
  SeamHidden = false
  SeamVisible = false
  SectionDirection = 4
  SectionLineStretch = 1
  SectionNormal = (1e-16,-1,0)
  SectionOrigin = (0,0,0)
  SectionSymbol = A
  SmoothHidden = false
  SmoothVisible = true
  Source = -> [Body]
  TrimAfterCut = false
  UsePreviousCut = false
  X = 250
  XDirection = (1,1e-16,0)
  Y = 100
FEATURE [TechDraw::DrawViewDimension] Dimension026
  AngleOverride = false
  Arbitrary = false
  ArbitraryTolerances = false
  EqualTolerance = true
  ExtensionAngle = 0
  FormatSpec = %.2w
  FormatSpecOverTolerance = %+.2w
  FormatSpecUnderTolerance = %+.2w
  Inverted = false
  LineAngle = 0
  LockPosition = false
  MeasureType = 1
  OverTolerance = 0
  References2D = -> [ComplexSection001]
  Rotation = 0
  ScaleType = 0
  TheoreticalExact = false
  Type = 2
  UnderTolerance = 0
  X = -15.2006
  Y = 15.1792
FEATURE [TechDraw::DrawViewDimension] Dimension027
  AngleOverride = false
  Arbitrary = false
  ArbitraryTolerances = false
  EqualTolerance = true
  ExtensionAngle = 0
  FormatSpec = ⌀%.2w
  FormatSpecOverTolerance = %+.2w
  FormatSpecUnderTolerance = %+.2w
  Inverted = false
  LineAngle = 0
  LockPosition = false
  MeasureType = 1
  OverTolerance = 0
  References2D = -> [ComplexSection001]
  Rotation = 0
  ScaleType = 0
  TheoreticalExact = false
  Type = 1
  UnderTolerance = 0
  X = -34.9399
  Y = 12.974
FEATURE [TechDraw::DrawViewDimension] Dimension028
  AngleOverride = false
  Arbitrary = false
  ArbitraryTolerances = false
  EqualTolerance = true
  ExtensionAngle = 0
  FormatSpec = ⌀%.2w
  FormatSpecOverTolerance = %+.2w
  FormatSpecUnderTolerance = %+.2w
  Inverted = false
  LineAngle = 0
  LockPosition = false
  MeasureType = 1
  OverTolerance = 0
  References2D = -> [ComplexSection001]
  Rotation = 0
  ScaleType = 0
  TheoreticalExact = false
  Type = 1
  UnderTolerance = 0
  X = -29.1594
  Y = -4.36749
FEATURE [TechDraw::DrawViewDimension] Dimension029
  AngleOverride = false
  Arbitrary = false
  ArbitraryTolerances = false
  EqualTolerance = true
  ExtensionAngle = 0
  FormatSpec = %.2w
  FormatSpecOverTolerance = %+.2w
  FormatSpecUnderTolerance = %+.2w
  Inverted = false
  LineAngle = 0
  LockPosition = false
  MeasureType = 1
  OverTolerance = 0
  References2D = -> [ComplexSection001]
  Rotation = 0
  ScaleType = 0
  TheoreticalExact = false
  Type = 2
  UnderTolerance = 0
  X = 93.4769
  Y = -9.09359
FEATURE [TechDraw::DrawViewAnnotation] Annotation
  Font = osifont
  LineSpace = 100
  LockPosition = false
  MaxWidth = -1
  Rotation = 0
  ScaleType = 0
  Text = A-A
  TextSize = 5
  TextStyle = 0
  X = 176.234
  Y = 89.3382
FEATURE [TechDraw::DrawViewDimension] Dimension030
  AngleOverride = false
  Arbitrary = false
  ArbitraryTolerances = false
  BoxCorners = (2) [(-90,-52.5,0),(90,52.5,0)]
  EqualTolerance = true
  ExtensionAngle = 0
  FormatSpec = %.2w
  FormatSpecOverTolerance = %+.2w
  FormatSpecUnderTolerance = %+.2w
  Inverted = false
  LineAngle = 0
  LockPosition = false
  MeasureType = 1
  OverTolerance = 0
  References2D = -> [ProjItem001]
  Rotation = 0
  ScaleType = 0
  TheoreticalExact = false
  Type = 1
  UnderTolerance = 0
  X = -0.147574
  Y = -24.2021
FEATURE [TechDraw::DrawViewDimension] Dimension031
  AngleOverride = false
  Arbitrary = false
  ArbitraryTolerances = false
  BoxCorners = (2) [(-90,-52.5,0),(90,52.5,0)]
  EqualTolerance = true
  ExtensionAngle = 0
  FormatSpec = %.2w
  FormatSpecOverTolerance = %+.2w
  FormatSpecUnderTolerance = %+.2w
  Inverted = false
  LineAngle = 0
  LockPosition = false
  MeasureType = 1
  OverTolerance = 0
  References2D = -> [ProjItem001]
  Rotation = 0
  ScaleType = 0
  TheoreticalExact = false
  Type = 2
  UnderTolerance = 0
  X = 13.0295
  Y = 7.5
FEATURE [TechDraw::DrawViewDimension] Dimension032
  AngleOverride = false
  Arbitrary = false
  ArbitraryTolerances = false
  EqualTolerance = true
  ExtensionAngle = 0
  FormatSpec = R%.2w
  FormatSpecOverTolerance = %+.2w
  FormatSpecUnderTolerance = %+.2w
  Inverted = false
  LineAngle = 0
  LockPosition = false
  MeasureType = 1
  OverTolerance = 0
  References2D = -> [ProjItem001]
  Rotation = 0
  ScaleType = 0
  TheoreticalExact = false
  Type = 4
  UnderTolerance = 0
  X = -14.0195
  Y = 38.2216
FEATURE [TechDraw::DrawViewDimension] Dimension033
  AngleOverride = false
  Arbitrary = false
  ArbitraryTolerances = false
  BoxCorners = (2) [(-90,-2.25,-1e-07),(90,2.25,1e-07)]
  EqualTolerance = true
  ExtensionAngle = 0
  FormatSpec = %.2w
  FormatSpecOverTolerance = %+.2w
  FormatSpecUnderTolerance = %+.2w
  Inverted = false
  LineAngle = 0
  LockPosition = false
  MeasureType = 1
  OverTolerance = 0
  References2D = -> [ComplexSection]
  Rotation = 0
  ScaleType = 0
  TheoreticalExact = false
  Type = 1
  UnderTolerance = 0
  X = -13.8327
  Y = 22.729
FEATURE [TechDraw::DrawViewDimension] Dimension034
  AngleOverride = false
  Arbitrary = false
  ArbitraryTolerances = false
  EqualTolerance = true
  ExtensionAngle = 0
  FormatSpec = R%.2w
  FormatSpecOverTolerance = %+.2w
  FormatSpecUnderTolerance = %+.2w
  Inverted = false
  LineAngle = 0
  LockPosition = false
  MeasureType = 1
  OverTolerance = 0
  References2D = -> [ProjItem]
  Rotation = 0
  ScaleType = 0
  TheoreticalExact = false
  Type = 4
  UnderTolerance = 0
  X = -0.162323
  Y = 26.2963
FEATURE [TechDraw::DrawViewDimension] Dimension035
  AngleOverride = false
  Arbitrary = false
  ArbitraryTolerances = false
  BoxCorners = (2) [(-90,-52.5,0),(90,52.5,0)]
  EqualTolerance = true
  ExtensionAngle = 0
  FormatSpec = %.2w
  FormatSpecOverTolerance = %+.2w
  FormatSpecUnderTolerance = %+.2w
  Inverted = false
  LineAngle = 0
  LockPosition = false
  MeasureType = 1
  OverTolerance = 0
  References2D = -> [ProjItem]
  Rotation = 0
  ScaleType = 0
  TheoreticalExact = false
  Type = 2
  UnderTolerance = 0
  X = -98.5979
  Y = -7.15838
FEATURE [TechDraw::DrawViewDimension] Dimension036
  AngleOverride = false
  Arbitrary = false
  ArbitraryTolerances = false
  BoxCorners = (2) [(-90,-2.25,-1e-07),(90,2.25,1e-07)]
  EqualTolerance = true
  ExtensionAngle = 0
  FormatSpec = %.2w
  FormatSpecOverTolerance = %+.2w
  FormatSpecUnderTolerance = %+.2w
  Inverted = false
  LineAngle = 0
  LockPosition = false
  MeasureType = 1
  OverTolerance = 0
  References2D = -> [ComplexSection001]
  Rotation = 0
  ScaleType = 0
  TheoreticalExact = false
  Type = 1
  UnderTolerance = 0
  X = 81.25
  Y = -3.21593
FEATURE [TechDraw::DrawViewDimension] Dimension037
  AngleOverride = false
  Arbitrary = false
  ArbitraryTolerances = false
  BoxCorners = (2) [(-90,-2.25,-1e-07),(90,2.25,1e-07)]
  EqualTolerance = true
  ExtensionAngle = 0
  FormatSpec = %.0w
  FormatSpecOverTolerance = %+.2w
  FormatSpecUnderTolerance = %+.2w
  Inverted = false
  LineAngle = 0
  LockPosition = false
  MeasureType = 1
  OverTolerance = 0
  References2D = -> [ComplexSection001]
  Rotation = 0
  ScaleType = 0
  TheoreticalExact = false
  Type = 1
  UnderTolerance = 0
  X = 55.2917
  Y = -3.21593
FEATURE [TechDraw::DrawViewDimension] Dimension038
  AngleOverride = false
  Arbitrary = false
  ArbitraryTolerances = false
  BoxCorners = (2) [(-90,-2.25,-1e-07),(90,2.25,1e-07)]
  EqualTolerance = true
  ExtensionAngle = 0
  FormatSpec = %.2w
  FormatSpecOverTolerance = %+.2w
  FormatSpecUnderTolerance = %+.2w
  Inverted = false
  LineAngle = 0
  LockPosition = false
  MeasureType = 1
  OverTolerance = 0
  References2D = -> [ComplexSection001]
  Rotation = 0
  ScaleType = 0
  TheoreticalExact = false
  Type = 1
  UnderTolerance = 0
  X = 72.5
  Y = 17.734
FEATURE [TechDraw::DrawViewDimension] Dimension039
  AngleOverride = false
  Arbitrary = false
  ArbitraryTolerances = false
  BoxCorners = (2) [(-90,-2.25,-1e-07),(90,2.25,1e-07)]
  EqualTolerance = true
  ExtensionAngle = 0
  FormatSpec = %.2w
  FormatSpecOverTolerance = %+.2w
  FormatSpecUnderTolerance = %+.2w
  Inverted = false
  LineAngle = 0
  LockPosition = false
  MeasureType = 1
  OverTolerance = 0
  References2D = -> [ComplexSection001]
  Rotation = 0
  ScaleType = 0
  TheoreticalExact = false
  Type = 1
  UnderTolerance = 0
  X = 38.0833
  Y = 17.734
FEATURE [TechDraw::DrawViewDimension] Dimension040
  AngleOverride = false
  Arbitrary = false
  ArbitraryTolerances = false
  BoxCorners = (2) [(-90,-52.5,0),(90,52.5,0)]
  EqualTolerance = true
  ExtensionAngle = 0
  FormatSpec = %.2w
  FormatSpecOverTolerance = %+.2w
  FormatSpecUnderTolerance = %+.2w
  Inverted = false
  LineAngle = 0
  LockPosition = false
  MeasureType = 1
  OverTolerance = 0
  References2D = -> [ProjItem001]
  Rotation = 0
  ScaleType = 0
  TheoreticalExact = false
  Type = 2
  UnderTolerance = 0
  X = 13.0295
  Y = 43
FEATURE [TechDraw::DrawViewDimension] Dimension041
  AngleOverride = false
  Arbitrary = false
  ArbitraryTolerances = false
  BoxCorners = (2) [(-90,-52.5,0),(90,52.5,0)]
  EqualTolerance = true
  ExtensionAngle = 0
  FormatSpec = %.2w
  FormatSpecOverTolerance = %+.2w
  FormatSpecUnderTolerance = %+.2w
  Inverted = false
  LineAngle = 0
  LockPosition = false
  MeasureType = 1
  OverTolerance = 0
  References2D = -> [ProjItem001]
  Rotation = 0
  ScaleType = 0
  TheoreticalExact = false
  Type = 2
  UnderTolerance = 0
  X = 94.2278
  Y = -9.25
FEATURE [TechDraw::DrawViewDimension] Dimension042
  AngleOverride = false
  Arbitrary = false
  ArbitraryTolerances = false
  BoxCorners = (2) [(-90,-52.5,0),(90,52.5,0)]
  EqualTolerance = true
  ExtensionAngle = 0
  FormatSpec = %.2w
  FormatSpecOverTolerance = %+.2w
  FormatSpecUnderTolerance = %+.2w
  Inverted = false
  LineAngle = 0
  LockPosition = false
  MeasureType = 1
  OverTolerance = 0
  References2D = -> [ProjItem001]
  Rotation = 0
  ScaleType = 0
  TheoreticalExact = false
  Type = 2
  UnderTolerance = 0
  X = 94.2278
  Y = 34.125
FEATURE [TechDraw::DrawPage] Page001  label="table: bottom part"
  KeepUpdated = true
  NextBalloonIndex = 1
  ProjectionType = 0
  Template = -> Template001
  Views = -> [ActiveView001,ProjGroup001,Dimension022,Dimension023,Dimension024,Dimension025,ComplexSection001,Dimension026,Dimension027,Dimension028,Dimension029,Annotation,Dimension030,Dimension031,Dimension032,Dimension036,Dimension037,Dimension038,Dimension039,Dimension040,Dimension041,Dimension042]
FEATURE [TechDraw::DrawViewImage] ActiveView
  Height = 100
  ImageFile = <userpath>/.cache/FreeCAD/Cache/FreeCAD_Doc_22664915-c8ef-4449-a133-44cb3a97b6c4_5768d8_4004/PageActiveViewEfLWVt.png
  LockPosition = false
  Rotation = 0
  Scale = 2
  ScaleType = 2
  Width = 100
  X = 60.0191
  Y = 256.627
FEATURE [TechDraw::DrawPage] Page  label="table: upper part"
  KeepUpdated = true
  NextBalloonIndex = 1
  ProjectionType = 0
  Template = -> Template
  Views = -> [ProjGroup,Dimension003,Dimension004,Dimension005,Dimension009,Dimension010,Dimension012,Dimension013,Dimension014,Dimension015,Dimension016,ComplexSection,Dimension017,Dimension018,Dimension019,Dimension020,Dimension,Dimension021,Dimension033,Dimension034,Dimension035,ActiveView]
FEATURE [TechDraw::DrawSVGTemplate] Template002
  EditableTexts = AUTHOR_NAME=Grzegorz Sapijaszko; DN=DN; DRAWING_TITLE=DRAWING TITLE; FC-DATE=DD/MM/YYYY; FC-REV=REV A; FC-SC=SCALE; FC-SH=X / Y; FC-SI=A3; FreeCAD_DRAWING=Licence: CERN-OHL-S; PN=PN
  Height = 297
  Orientation = 1
  Template = <userpath>/.local/share/FreeCAD/Mod/aaa/Templates/gs_A3_Landscape_ISO7200_OSH.svg
  Width = 420
FEATURE [TechDraw::DrawProjGroupItem] ProjItem002  label="Front002"
  CoarseView = false
  Direction = (0,-1,0)
  Focus = 100
  HardHidden = false
  IsoCount = 0
  IsoHidden = false
  IsoVisible = false
  LockPosition = true
  Perspective = false
  Rotation = 0
  RotationVector = (1,0,0)
  Scale = 0.5
  ScaleType = 2
  ScrubCount = 0
  SeamHidden = false
  SeamVisible = false
  SmoothHidden = false
  SmoothVisible = true
  Source = -> [Body004]
  Type = 0
  X = 0
  XDirection = (1,0,0)
  Y = 0
FEATURE [TechDraw::DrawProjGroupItem] ProjItem003  label="Right"
  CoarseView = false
  Direction = (1,-1e-16,0)
  Focus = 100
  HardHidden = false
  IsoCount = 0
  IsoHidden = false
  IsoVisible = false
  LockPosition = false
  Perspective = false
  Rotation = 0
  RotationVector = (1,0,0)
  Scale = 0.5
  ScaleType = 2
  ScrubCount = 0
  SeamHidden = false
  SeamVisible = false
  SmoothHidden = false
  SmoothVisible = true
  Source = -> [Body004]
  Type = 2
  X = -137.375
  XDirection = (1e-16,1,0)
  Y = 0
FEATURE [TechDraw::DrawProjGroup] ProjGroup002
  Anchor = -> ProjItem002
  AutoDistribute = true
  LockPosition = false
  ProjectionType = 0
  Rotation = 0
  Scale = 0.5
  ScaleType = 1
  Source = -> [Body004]
  Views = -> [ProjItem002,ProjItem003]
  X = 250
  Y = 150
  spacingX = 45
  spacingY = 15
FEATURE [TechDraw::DrawViewDimension] Dimension043
  AngleOverride = false
  Arbitrary = false
  ArbitraryTolerances = false
  EqualTolerance = true
  ExtensionAngle = 0
  FormatSpec = %.2w
  FormatSpecOverTolerance = %+.2w
  FormatSpecUnderTolerance = %+.2w
  Inverted = false
  LineAngle = 0
  LockPosition = false
  MeasureType = 1
  OverTolerance = 0
  References2D = -> [ProjItem002]
  Rotation = 0
  ScaleType = 0
  TheoreticalExact = false
  Type = 1
  UnderTolerance = 0
  X = 2.28843
  Y = -26.4142
FEATURE [TechDraw::DrawViewDimension] Dimension044
  AngleOverride = false
  Arbitrary = false
  ArbitraryTolerances = false
  EqualTolerance = true
  ExtensionAngle = 0
  FormatSpec = %.2w
  FormatSpecOverTolerance = %+.2w
  FormatSpecUnderTolerance = %+.2w
  Inverted = false
  LineAngle = 0
  LockPosition = false
  MeasureType = 1
  OverTolerance = 0
  References2D = -> [ProjItem003]
  Rotation = 0
  ScaleType = 0
  TheoreticalExact = false
  Type = 1
  UnderTolerance = 0
  X = -1.29318
  Y = 29.3361
FEATURE [TechDraw::DrawViewDimension] Dimension045
  AngleOverride = false
  Arbitrary = false
  ArbitraryTolerances = false
  EqualTolerance = true
  ExtensionAngle = 0
  FormatSpec = R%.2w
  FormatSpecOverTolerance = %+.2w
  FormatSpecUnderTolerance = %+.2w
  Inverted = false
  LineAngle = 0
  LockPosition = false
  MeasureType = 1
  OverTolerance = 0
  References2D = -> [ProjItem002]
  Rotation = 0
  ScaleType = 0
  TheoreticalExact = false
  Type = 4
  UnderTolerance = 0
  X = -90.0362
  Y = 23.7515
FEATURE [TechDraw::DrawViewDimension] Dimension046
  AngleOverride = false
  Arbitrary = false
  ArbitraryTolerances = false
  BoxCorners = (2) [(-84.375,-16.25,0),(84.375,16.25,0)]
  EqualTolerance = true
  ExtensionAngle = 0
  FormatSpec = %.2w
  FormatSpecOverTolerance = %+.2w
  FormatSpecUnderTolerance = %+.2w
  Inverted = false
  LineAngle = 0
  LockPosition = false
  MeasureType = 1
  OverTolerance = 0
  References2D = -> [ProjItem002]
  Rotation = 0
  ScaleType = 0
  TheoreticalExact = false
  Type = 2
  UnderTolerance = 0
  X = 98.5914
  Y = 5.0391
FEATURE [TechDraw::DrawViewDimension] Dimension047
  AngleOverride = false
  Arbitrary = false
  ArbitraryTolerances = false
  BoxCorners = (2) [(-8,-16.25,-1e-07),(8,16.25,1e-07)]
  EqualTolerance = true
  ExtensionAngle = 0
  FormatSpec = %.2w
  FormatSpecOverTolerance = %+.2w
  FormatSpecUnderTolerance = %+.2w
  Inverted = false
  LineAngle = 0
  LockPosition = false
  MeasureType = 1
  OverTolerance = 0
  References2D = -> [ProjItem003]
  Rotation = 0
  ScaleType = 0
  TheoreticalExact = false
  Type = 2
  UnderTolerance = 0
  X = 23.7716
  Y = -15.9991
FEATURE [TechDraw::DrawViewDimension] Dimension048
  AngleOverride = false
  Arbitrary = false
  ArbitraryTolerances = false
  EqualTolerance = true
  ExtensionAngle = 0
  FormatSpec = %.2w
  FormatSpecOverTolerance = %+.2w
  FormatSpecUnderTolerance = %+.2w
  Inverted = false
  LineAngle = 0
  LockPosition = false
  MeasureType = 1
  OverTolerance = 0
  References2D = -> [ProjItem003]
  Rotation = 0
  ScaleType = 0
  TheoreticalExact = false
  Type = 2
  UnderTolerance = 0
  X = -37.0376
  Y = -17.6198
FEATURE [TechDraw::DrawViewDimension] Dimension049
  AngleOverride = false
  Arbitrary = false
  ArbitraryTolerances = false
  EqualTolerance = true
  ExtensionAngle = 0
  FormatSpec = %.2w
  FormatSpecOverTolerance = %+.2w
  FormatSpecUnderTolerance = %+.2w
  Inverted = false
  LineAngle = 0
  LockPosition = false
  MeasureType = 1
  OverTolerance = 0
  References2D = -> [ProjItem003]
  Rotation = 0
  ScaleType = 0
  TheoreticalExact = false
  Type = 1
  UnderTolerance = 0
  X = -13.6448
  Y = -16.6015
FEATURE [TechDraw::DrawViewDimension] Dimension050
  AngleOverride = false
  Arbitrary = false
  ArbitraryTolerances = false
  EqualTolerance = true
  ExtensionAngle = 0
  FormatSpec = %.2w
  FormatSpecOverTolerance = %+.2w
  FormatSpecUnderTolerance = %+.2w
  Inverted = false
  LineAngle = 0
  LockPosition = false
  MeasureType = 1
  OverTolerance = 0
  References2D = -> [ProjItem003]
  Rotation = 0
  ScaleType = 0
  TheoreticalExact = false
  Type = 2
  UnderTolerance = 0
  X = -37.0801
  Y = -6.25
FEATURE [TechDraw::DrawViewDimension] Dimension051
  AngleOverride = false
  Arbitrary = false
  ArbitraryTolerances = false
  EqualTolerance = true
  ExtensionAngle = 0
  FormatSpec = %.2w
  FormatSpecOverTolerance = %+.2w
  FormatSpecUnderTolerance = %+.2w
  Inverted = false
  LineAngle = 0
  LockPosition = false
  MeasureType = 1
  OverTolerance = 0
  References2D = -> [ProjItem003]
  Rotation = 0
  ScaleType = 0
  TheoreticalExact = false
  Type = 2
  UnderTolerance = 0
  X = -37.0801
  Y = 4
FEATURE [TechDraw::DrawViewDimension] Dimension052
  AngleOverride = false
  Arbitrary = false
  ArbitraryTolerances = false
  EqualTolerance = true
  ExtensionAngle = 0
  FormatSpec = %.2w
  FormatSpecOverTolerance = %+.2w
  FormatSpecUnderTolerance = %+.2w
  Inverted = false
  LineAngle = 0
  LockPosition = false
  MeasureType = 1
  OverTolerance = 0
  References2D = -> [ProjItem003]
  Rotation = 0
  ScaleType = 0
  TheoreticalExact = false
  Type = 1
  UnderTolerance = 0
  X = -17.473
  Y = 5.74017
FEATURE [TechDraw::DrawPage] Page002  label="fence:face_r_l"
  KeepUpdated = true
  NextBalloonIndex = 1
  ProjectionType = 0
  Template = -> Template002
  Views = -> [ProjGroup002,Dimension043,Dimension044,Dimension045,Dimension046,Dimension047,Dimension048,Dimension049,Dimension050,Dimension051,Dimension052]
FEATURE [TechDraw::DrawSVGTemplate] Template003
  EditableTexts = AUTHOR_NAME=Grzegorz Sapijaszko; DN=DN; DRAWING_TITLE=DRAWING TITLE; FC-DATE=DD/MM/YYYY; FC-REV=REV A; FC-SC=SCALE; FC-SH=X / Y; FC-SI=A3; FreeCAD_DRAWING=Licence: CERN-OHL-S; PN=PN
  Height = 297
  Orientation = 1
  Template = <userpath>/.local/share/FreeCAD/Mod/aaa/Templates/gs_A3_Landscape_ISO7200_OSH.svg
  Width = 420
FEATURE [TechDraw::DrawViewImage] ActiveView002
  Height = 50
  ImageFile = <userpath>/.cache/FreeCAD/Cache/FreeCAD_Doc_22664915-c8ef-4449-a133-44cb3a97b6c4_5768d8_12635/Page003ActiveView0020oRSvy.png
  LockPosition = false
  Rotation = 0
  Scale = 2
  ScaleType = 2
  Width = 70
  X = 374.769
  Y = 258.957
FEATURE [TechDraw::DrawProjGroupItem] ProjItem004  label="Front003"
  CoarseView = false
  Direction = (0,1,0)
  Focus = 100
  HardHidden = false
  IsoCount = 0
  IsoHidden = false
  IsoVisible = false
  LockPosition = true
  Perspective = false
  Rotation = 0
  RotationVector = (1,0,0)
  Scale = 0.375
  ScaleType = 2
  ScrubCount = 0
  SeamHidden = false
  SeamVisible = false
  SmoothHidden = false
  SmoothVisible = true
  Source = -> [Part003]
  Type = 0
  X = 0
  XDirection = (1,0,0)
  Y = 0
FEATURE [TechDraw::DrawProjGroupItem] ProjItem006  label="Bottom"
  CoarseView = false
  Direction = (0,0,1)
  Focus = 100
  HardHidden = false
  IsoCount = 0
  IsoHidden = false
  IsoVisible = false
  LockPosition = false
  Perspective = false
  Rotation = 0
  RotationVector = (1,0,0)
  Scale = 0.375
  ScaleType = 2
  ScrubCount = 0
  SeamHidden = false
  SeamVisible = false
  SmoothHidden = false
  SmoothVisible = true
  Source = -> [Part003]
  Type = 5
  X = 0
  XDirection = (1,0,0)
  Y = 70.5
FEATURE [TechDraw::DrawProjGroupItem] ProjItem007  label="Left"
  CoarseView = false
  Direction = (-1,1e-16,0)
  Focus = 100
  HardHidden = false
  IsoCount = 0
  IsoHidden = false
  IsoVisible = false
  LockPosition = false
  Perspective = false
  Rotation = 0
  RotationVector = (1,0,0)
  Scale = 0.375
  ScaleType = 2
  ScrubCount = 0
  SeamHidden = false
  SeamVisible = false
  SmoothHidden = false
  SmoothVisible = true
  Source = -> [Part003]
  Type = 1
  X = 106.125
  XDirection = (1e-16,1,0)
  Y = 0
FEATURE [TechDraw::DrawProjGroupItem] ProjItem008  label="Top"
  CoarseView = false
  Direction = (0,0,-1)
  Focus = 100
  HardHidden = false
  IsoCount = 0
  IsoHidden = false
  IsoVisible = false
  LockPosition = false
  Perspective = false
  Rotation = 0
  RotationVector = (1,0,0)
  Scale = 0.375
  ScaleType = 2
  ScrubCount = 0
  SeamHidden = false
  SeamVisible = false
  SmoothHidden = false
  SmoothVisible = true
  Source = -> [Part003]
  Type = 4
  X = 0
  XDirection = (1,0,0)
  Y = -70.5
FEATURE [TechDraw::DrawProjGroup] ProjGroup003
  Anchor = -> ProjItem004
  AutoDistribute = true
  LockPosition = false
  ProjectionType = 0
  Rotation = 0
  Scale = 0.375
  ScaleType = 1
  Source = -> [Part003]
  Views = -> [ProjItem004,ProjItem006,ProjItem007,ProjItem008]
  X = 150
  Y = 150
  spacingX = 15
  spacingY = 15
FEATURE [TechDraw::DrawViewDimension] Dimension053
  AngleOverride = false
  Arbitrary = false
  ArbitraryTolerances = false
  BoxCorners = (2) [(-49.125,-42,0),(49.125,42,0)]
  EqualTolerance = true
  ExtensionAngle = 0
  FormatSpec = %.2w
  FormatSpecOverTolerance = %+.2w
  FormatSpecUnderTolerance = %+.2w
  Inverted = false
  LineAngle = 0
  LockPosition = false
  MeasureType = 1
  OverTolerance = 0
  References2D = -> [ProjItem006]
  Rotation = 0
  ScaleType = 0
  TheoreticalExact = false
  Type = 2
  UnderTolerance = 0
  X = 54.2455
  Y = -29.6356
FEATURE [TechDraw::DrawViewDimension] Dimension054
  AngleOverride = false
  Arbitrary = false
  ArbitraryTolerances = false
  BoxCorners = (2) [(-32.75,-28,0),(32.75,28,0)]
  EqualTolerance = true
  ExtensionAngle = 0
  FormatSpec = %.2w
  FormatSpecOverTolerance = %+.2w
  FormatSpecUnderTolerance = %+.2w
  Inverted = false
  LineAngle = 0
  LockPosition = false
  MeasureType = 1
  OverTolerance = 0
  References2D = -> [ProjItem006]
  Rotation = 0
  ScaleType = 0
  TheoreticalExact = false
  Type = 1
  UnderTolerance = 0
  X = -0.318702
  Y = -43.2457
FEATURE [TechDraw::DrawViewDimension] Dimension055
  AngleOverride = false
  Arbitrary = false
  ArbitraryTolerances = false
  BoxCorners = (2) [(-32.75,-28,0),(32.75,28,0)]
  EqualTolerance = true
  ExtensionAngle = 0
  FormatSpec = %.2w
  FormatSpecOverTolerance = %+.2w
  FormatSpecUnderTolerance = %+.2w
  Inverted = false
  LineAngle = 0
  LockPosition = false
  MeasureType = 1
  OverTolerance = 0
  References2D = -> [ProjItem006]
  Rotation = 0
  ScaleType = 0
  TheoreticalExact = false
  Type = 1
  UnderTolerance = 0
  X = 49.8466
  Y = 51.4137
FEATURE [TechDraw::DrawViewDimension] Dimension056
  AngleOverride = false
  Arbitrary = false
  ArbitraryTolerances = false
  BoxCorners = (2) [(-49.125,-42,0),(49.125,42,0)]
  EqualTolerance = true
  ExtensionAngle = 0
  FormatSpec = %.2w
  FormatSpecOverTolerance = %+.2w
  FormatSpecUnderTolerance = %+.2w
  Inverted = false
  LineAngle = 0
  LockPosition = false
  MeasureType = 1
  OverTolerance = 0
  References2D = -> [ProjItem006]
  Rotation = 0
  ScaleType = 0
  TheoreticalExact = false
  Type = 1
  UnderTolerance = 0
  X = 0.213054
  Y = 24.273
FEATURE [TechDraw::DrawViewDimension] Dimension057
  AngleOverride = false
  Arbitrary = false
  ArbitraryTolerances = false
  BoxCorners = (2) [(-32.75,-28,0),(32.75,28,0)]
  EqualTolerance = true
  ExtensionAngle = 0
  FormatSpec = %.2w
  FormatSpecOverTolerance = %+.2w
  FormatSpecUnderTolerance = %+.2w
  Inverted = false
  LineAngle = 0
  LockPosition = false
  MeasureType = 1
  OverTolerance = 0
  References2D = -> [ProjItem006]
  Rotation = 0
  ScaleType = 0
  TheoreticalExact = false
  Type = 2
  UnderTolerance = 0
  X = 37.3905
  Y = 11.4426
FEATURE [TechDraw::DrawViewDimension] Dimension058
  AngleOverride = false
  Arbitrary = false
  ArbitraryTolerances = false
  BoxCorners = (2) [(-28,-9,-1e-07),(28,9,1e-07)]
  EqualTolerance = true
  ExtensionAngle = 0
  FormatSpec = %.2w
  FormatSpecOverTolerance = %+.2w
  FormatSpecUnderTolerance = %+.2w
  Inverted = false
  LineAngle = 0
  LockPosition = false
  MeasureType = 1
  OverTolerance = 0
  References2D = -> [ProjItem007]
  Rotation = 0
  ScaleType = 0
  TheoreticalExact = false
  Type = 2
  UnderTolerance = 0
  X = -35.6194
  Y = 2.84117
FEATURE [TechDraw::DrawViewDimension] Dimension059
  AngleOverride = false
  Arbitrary = false
  ArbitraryTolerances = false
  BoxCorners = (2) [(-28,-9,-1e-07),(28,9,1e-07)]
  EqualTolerance = true
  ExtensionAngle = 0
  FormatSpec = %.2w
  FormatSpecOverTolerance = %+.2w
  FormatSpecUnderTolerance = %+.2w
  Inverted = false
  LineAngle = 0
  LockPosition = false
  MeasureType = 1
  OverTolerance = 0
  References2D = -> [ProjItem007]
  Rotation = 0
  ScaleType = 0
  TheoreticalExact = false
  Type = 2
  UnderTolerance = 0
  X = 33.7999
  Y = 0.704891
FEATURE [TechDraw::DrawViewDimension] Dimension060
  AngleOverride = false
  Arbitrary = false
  ArbitraryTolerances = false
  BoxCorners = (2) [(-49.125,-42,0),(49.125,42,0)]
  EqualTolerance = true
  ExtensionAngle = 0
  FormatSpec = %.2w
  FormatSpecOverTolerance = %+.2w
  FormatSpecUnderTolerance = %+.2w
  Inverted = false
  LineAngle = 0
  LockPosition = false
  MeasureType = 1
  OverTolerance = 0
  References2D = -> [ProjItem006]
  Rotation = 0
  ScaleType = 0
  TheoreticalExact = false
  Type = 2
  UnderTolerance = 0
  X = 6.68728
  Y = -12.2027
FEATURE [TechDraw::DrawViewDimension] Dimension061
  AngleOverride = false
  Arbitrary = false
  ArbitraryTolerances = false
  BoxCorners = (2) [(-49.125,-42,0),(49.125,42,0)]
  EqualTolerance = true
  ExtensionAngle = 0
  FormatSpec = %.2w
  FormatSpecOverTolerance = %+.2w
  FormatSpecUnderTolerance = %+.2w
  Inverted = false
  LineAngle = 0
  LockPosition = false
  MeasureType = 1
  OverTolerance = 0
  References2D = -> [ProjItem006]
  Rotation = 0
  ScaleType = 0
  TheoreticalExact = false
  Type = 1
  UnderTolerance = 0
  X = 14.0751
  Y = -6.90306
FEATURE [TechDraw::DrawSVGTemplate] Template004
  EditableTexts = Designed_by_Name=Grzegorz Sapijaszko; Drawing_number=Drawing number; FC-Date=5/10/24; FC-SC=1 : 1; FC-SH=3 / 5; FC-Title=drill_press_table; Subtitle=Subtitle; Weight=Weight
  Height = 210
  Orientation = 1
  Template = <path>
  Width = 297
FEATURE [TechDraw::DrawSVGTemplate] Template005
  EditableTexts = AUTHOR_NAME=Grzegorz Sapijaszko; DN=DN; DRAWING_TITLE=DRAWING TITLE; FC-DATE=DD/MM/YYYY; FC-REV=REV A; FC-SC=SCALE; FC-SH=X / Y; FC-SI=A3; FreeCAD_DRAWING=Licence: CERN-OHL-S; PN=PN
  Height = 297
  Orientation = 1
  Template = <userpath>/.cache/FreeCAD/Cache/FreeCAD_Doc_22664915-c8ef-4449-a133-44cb3a97b6c4_5768d8_10244/A4_Landscape_TD.svg
  Width = 420
FEATURE [TechDraw::DrawProjGroupItem] ProjItem009  label="Front004"
  CoarseView = false
  Direction = (0,-1,0)
  Focus = 100
  HardHidden = false
  IsoCount = 0
  IsoHidden = false
  IsoVisible = false
  LockPosition = true
  Perspective = false
  Rotation = 0
  RotationVector = (1,0,0)
  ScaleType = 2
  ScrubCount = 0
  SeamHidden = false
  SeamVisible = false
  SmoothHidden = false
  SmoothVisible = true
  Source = -> [Body015]
  Type = 0
  X = 0
  XDirection = (1,0,0)
  Y = 0
FEATURE [TechDraw::DrawProjGroupItem] ProjItem010  label="Right001"
  CoarseView = false
  Direction = (1,-1e-16,0)
  Focus = 100
  HardHidden = false
  IsoCount = 0
  IsoHidden = false
  IsoVisible = false
  LockPosition = false
  Perspective = false
  Rotation = 0
  RotationVector = (1,0,0)
  ScaleType = 2
  ScrubCount = 0
  SeamHidden = false
  SeamVisible = false
  SmoothHidden = false
  SmoothVisible = true
  Source = -> [Body015]
  Type = 2
  X = -122.3
  XDirection = (1e-16,1,0)
  Y = 0
FEATURE [TechDraw::DrawProjGroupItem] ProjItem011  label="Top001"
  CoarseView = false
  Direction = (0,0,1)
  Focus = 100
  HardHidden = false
  IsoCount = 0
  IsoHidden = false
  IsoVisible = false
  LockPosition = false
  Perspective = false
  Rotation = 0
  RotationVector = (1,0,0)
  ScaleType = 2
  ScrubCount = 0
  SeamHidden = false
  SeamVisible = false
  SmoothHidden = false
  SmoothVisible = true
  Source = -> [Body015]
  Type = 4
  X = 0
  XDirection = (1,0,0)
  Y = -55
FEATURE [TechDraw::DrawProjGroup] ProjGroup004
  Anchor = -> ProjItem009
  AutoDistribute = true
  LockPosition = false
  ProjectionType = 0
  Rotation = 0
  ScaleType = 2
  Source = -> [Body015]
  Views = -> [ProjItem009,ProjItem010,ProjItem011]
  X = 160
  Y = 150
  spacingX = 25
  spacingY = 25
FEATURE [TechDraw::DrawViewDimension] Dimension062
  AngleOverride = false
  Arbitrary = false
  ArbitraryTolerances = false
  BoxCorners = (2) [(-91.3,-6,0),(91.3,6,0)]
  EqualTolerance = true
  ExtensionAngle = 0
  FormatSpec = %.2w
  FormatSpecOverTolerance = %+.2w
  FormatSpecUnderTolerance = %+.2w
  Inverted = false
  LineAngle = 0
  LockPosition = false
  MeasureType = 1
  OverTolerance = 0
  References2D = -> [ProjItem011]
  Rotation = 0
  ScaleType = 0
  TheoreticalExact = false
  Type = 1
  UnderTolerance = 0
  X = 0.659042
  Y = 16.8479
FEATURE [TechDraw::DrawViewDimension] Dimension063
  AngleOverride = false
  Arbitrary = false
  ArbitraryTolerances = false
  BoxCorners = (2) [(-91.3,-6,0),(91.3,6,0)]
  EqualTolerance = true
  ExtensionAngle = 0
  FormatSpec = %.2w
  FormatSpecOverTolerance = %+.2w
  FormatSpecUnderTolerance = %+.2w
  Inverted = false
  LineAngle = 0
  LockPosition = false
  MeasureType = 1
  OverTolerance = 0
  References2D = -> [ProjItem011]
  Rotation = 0
  ScaleType = 0
  TheoreticalExact = false
  Type = 2
  UnderTolerance = 0
  X = -98.6227
  Y = 14.4752
FEATURE [TechDraw::DrawViewDimension] Dimension064
  AngleOverride = false
  Arbitrary = false
  ArbitraryTolerances = false
  BoxCorners = (2) [(-91.3,-6,0),(91.3,6,0)]
  EqualTolerance = true
  ExtensionAngle = 0
  FormatSpec = %.2w
  FormatSpecOverTolerance = %+.2w
  FormatSpecUnderTolerance = %+.2w
  Inverted = false
  LineAngle = 0
  LockPosition = false
  MeasureType = 1
  OverTolerance = 0
  References2D = -> [ProjItem011]
  Rotation = 0
  ScaleType = 0
  TheoreticalExact = false
  Type = 2
  UnderTolerance = 0
  X = -105.691
  Y = -11.5096
FEATURE [TechDraw::DrawViewDimension] Dimension065
  AngleOverride = false
  Arbitrary = false
  ArbitraryTolerances = false
  BoxCorners = (2) [(-6,-24,0),(6,24,0)]
  EqualTolerance = true
  ExtensionAngle = 0
  FormatSpec = %.2w
  FormatSpecOverTolerance = %+.2w
  FormatSpecUnderTolerance = %+.2w
  Inverted = false
  LineAngle = 0
  LockPosition = false
  MeasureType = 1
  OverTolerance = 0
  References2D = -> [ProjItem010]
  Rotation = 0
  ScaleType = 0
  TheoreticalExact = false
  Type = 1
  UnderTolerance = 0
  X = -0.529709
  Y = -34.8751
FEATURE [TechDraw::DrawViewDimension] Dimension066
  AngleOverride = false
  Arbitrary = false
  ArbitraryTolerances = false
  BoxCorners = (2) [(-6,-24,0),(6,24,0)]
  EqualTolerance = true
  ExtensionAngle = 0
  FormatSpec = %.2w
  FormatSpecOverTolerance = %+.2w
  FormatSpecUnderTolerance = %+.2w
  Inverted = false
  LineAngle = 0
  LockPosition = false
  MeasureType = 1
  OverTolerance = 0
  References2D = -> [ProjItem010]
  Rotation = 0
  ScaleType = 0
  TheoreticalExact = false
  Type = 2
  UnderTolerance = 0
  X = 10.3701
  Y = -25.5619
FEATURE [TechDraw::DrawViewDimension] Dimension067
  AngleOverride = false
  Arbitrary = false
  ArbitraryTolerances = false
  BoxCorners = (2) [(-6,-24,0),(6,24,0)]
  EqualTolerance = true
  ExtensionAngle = 0
  FormatSpec = %.2w
  FormatSpecOverTolerance = %+.2w
  FormatSpecUnderTolerance = %+.2w
  Inverted = false
  LineAngle = 0
  LockPosition = false
  MeasureType = 1
  OverTolerance = 0
  References2D = -> [ProjItem010]
  Rotation = 0
  ScaleType = 0
  TheoreticalExact = false
  Type = 2
  UnderTolerance = 0
  X = 15.2699
  Y = -7.33282
FEATURE [TechDraw::DrawViewDimension] Dimension068
  AngleOverride = false
  Arbitrary = false
  ArbitraryTolerances = false
  BoxCorners = (2) [(-6,-24,0),(6,24,0)]
  EqualTolerance = true
  ExtensionAngle = 0
  FormatSpec = %.2w
  FormatSpecOverTolerance = %+.2w
  FormatSpecUnderTolerance = %+.2w
  Inverted = false
  LineAngle = 0
  LockPosition = false
  MeasureType = 1
  OverTolerance = 0
  References2D = -> [ProjItem010]
  Rotation = 0
  ScaleType = 0
  TheoreticalExact = false
  Type = 2
  UnderTolerance = 0
  X = -17.5852
  Y = 3.84712
FEATURE [TechDraw::DrawProjGroupItem] ProjItem012  label="Front005"
  CoarseView = false
  Direction = (1,0,0)
  Focus = 100
  HardHidden = false
  IsoCount = 0
  IsoHidden = false
  IsoVisible = false
  LockPosition = true
  Perspective = false
  Rotation = 0
  RotationVector = (0,1,0)
  ScaleType = 2
  ScrubCount = 0
  SeamHidden = false
  SeamVisible = false
  SmoothHidden = false
  SmoothVisible = true
  Source = -> [Body016]
  Type = 0
  X = 0
  XDirection = (0,1,0)
  Y = 0
FEATURE [TechDraw::DrawProjGroupItem] ProjItem014  label="Left001"
  CoarseView = false
  Direction = (1e-16,-1,0)
  Focus = 100
  HardHidden = false
  IsoCount = 0
  IsoHidden = false
  IsoVisible = false
  LockPosition = false
  Perspective = false
  Rotation = 0
  RotationVector = (1,0,0)
  ScaleType = 2
  ScrubCount = 0
  SeamHidden = false
  SeamVisible = false
  SmoothHidden = false
  SmoothVisible = true
  Source = -> [Body016]
  Type = 1
  X = 134
  XDirection = (1,1e-16,0)
  Y = 0
FEATURE [TechDraw::DrawProjGroupItem] ProjItem015  label="Top002"
  CoarseView = false
  Direction = (0,0,1)
  Focus = 100
  HardHidden = false
  IsoCount = 0
  IsoHidden = false
  IsoVisible = false
  LockPosition = false
  Perspective = false
  Rotation = 0
  RotationVector = (1,0,0)
  ScaleType = 2
  ScrubCount = 0
  SeamHidden = false
  SeamVisible = false
  SmoothHidden = false
  SmoothVisible = true
  Source = -> [Body016]
  Type = 4
  X = 0
  XDirection = (0,1,0)
  Y = -55
FEATURE [TechDraw::DrawProjGroup] ProjGroup005
  Anchor = -> ProjItem012
  AutoDistribute = true
  LockPosition = false
  ProjectionType = 0
  Rotation = 0
  ScaleType = 0
  Source = -> [Body016]
  Views = -> [ProjItem012,ProjItem014,ProjItem015]
  X = 210
  Y = 170
  spacingX = 25
  spacingY = 25
FEATURE [TechDraw::DrawViewDimension] Dimension069
  AngleOverride = false
  Arbitrary = false
  ArbitraryTolerances = false
  BoxCorners = (2) [(-103,-6,0),(103,6,0)]
  EqualTolerance = true
  ExtensionAngle = 0
  FormatSpec = %.2w
  FormatSpecOverTolerance = %+.2w
  FormatSpecUnderTolerance = %+.2w
  Inverted = false
  LineAngle = 0
  LockPosition = false
  MeasureType = 1
  OverTolerance = 0
  References2D = -> [ProjItem015]
  Rotation = 0
  ScaleType = 0
  TheoreticalExact = false
  Type = 1
  UnderTolerance = 0
  X = 1.55335
  Y = 17.5612
FEATURE [TechDraw::DrawViewDimension] Dimension070
  AngleOverride = false
  Arbitrary = false
  ArbitraryTolerances = false
  BoxCorners = (2) [(-103,-6,0),(103,6,0)]
  EqualTolerance = true
  ExtensionAngle = 0
  FormatSpec = %.2w
  FormatSpecOverTolerance = %+.2w
  FormatSpecUnderTolerance = %+.2w
  Inverted = false
  LineAngle = 0
  LockPosition = false
  MeasureType = 1
  OverTolerance = 0
  References2D = -> [ProjItem015]
  Rotation = 0
  ScaleType = 0
  TheoreticalExact = false
  Type = 2
  UnderTolerance = 0
  X = -114.65
  Y = 2.75889
FEATURE [TechDraw::DrawViewDimension] Dimension071
  AngleOverride = false
  Arbitrary = false
  ArbitraryTolerances = false
  BoxCorners = (2) [(-103,-6,0),(103,6,0)]
  EqualTolerance = true
  ExtensionAngle = 0
  FormatSpec = %.2w
  FormatSpecOverTolerance = %+.2w
  FormatSpecUnderTolerance = %+.2w
  Inverted = false
  LineAngle = 0
  LockPosition = false
  MeasureType = 1
  OverTolerance = 0
  References2D = -> [ProjItem015]
  Rotation = 0
  ScaleType = 0
  TheoreticalExact = false
  Type = 1
  UnderTolerance = 0
  X = -98.5
  Y = -12.8206
FEATURE [TechDraw::DrawViewDimension] Dimension072
  AngleOverride = false
  Arbitrary = false
  ArbitraryTolerances = false
  BoxCorners = (2) [(-103,-6,0),(103,6,0)]
  EqualTolerance = true
  ExtensionAngle = 0
  FormatSpec = %.2w
  FormatSpecOverTolerance = %+.2w
  FormatSpecUnderTolerance = %+.2w
  Inverted = false
  LineAngle = 0
  LockPosition = false
  MeasureType = 1
  OverTolerance = 0
  References2D = -> [ProjItem015]
  Rotation = 0
  ScaleType = 0
  TheoreticalExact = false
  Type = 1
  UnderTolerance = 0
  X = -85.617
  Y = -12.82
FEATURE [TechDraw::DrawViewDimension] Dimension073
  AngleOverride = false
  Arbitrary = false
  ArbitraryTolerances = false
  BoxCorners = (2) [(-103,-24,0),(103,24,0)]
  EqualTolerance = true
  ExtensionAngle = 0
  FormatSpec = %.2w
  FormatSpecOverTolerance = %+.2w
  FormatSpecUnderTolerance = %+.2w
  Inverted = false
  LineAngle = 0
  LockPosition = false
  MeasureType = 1
  OverTolerance = 0
  References2D = -> [ProjItem012]
  Rotation = 0
  ScaleType = 0
  TheoreticalExact = false
  Type = 2
  UnderTolerance = 0
  X = -122.289
  Y = -19.5641
FEATURE [TechDraw::DrawViewDimension] Dimension074
  AngleOverride = false
  Arbitrary = false
  ArbitraryTolerances = false
  BoxCorners = (2) [(-103,-24,0),(103,24,0)]
  EqualTolerance = true
  ExtensionAngle = 0
  FormatSpec = %.2w
  FormatSpecOverTolerance = %+.2w
  FormatSpecUnderTolerance = %+.2w
  Inverted = false
  LineAngle = 0
  LockPosition = false
  MeasureType = 1
  OverTolerance = 0
  References2D = -> [ProjItem012]
  Rotation = 0
  ScaleType = 0
  TheoreticalExact = false
  Type = 2
  UnderTolerance = 0
  X = -112.372
  Y = -16.0192
FEATURE [TechDraw::DrawViewDimension] Dimension075
  AngleOverride = false
  Arbitrary = false
  ArbitraryTolerances = false
  BoxCorners = (2) [(-6,-24,0),(6,24,0)]
  EqualTolerance = true
  ExtensionAngle = 0
  FormatSpec = %.2w
  FormatSpecOverTolerance = %+.2w
  FormatSpecUnderTolerance = %+.2w
  Inverted = false
  LineAngle = 0
  LockPosition = false
  MeasureType = 1
  OverTolerance = 0
  References2D = -> [ProjItem014]
  Rotation = 0
  ScaleType = 0
  TheoreticalExact = false
  Type = 1
  UnderTolerance = 0
  X = 8.85085
  Y = -25.2286
FEATURE [TechDraw::DrawViewDimension] Dimension076
  AngleOverride = false
  Arbitrary = false
  ArbitraryTolerances = false
  BoxCorners = (2) [(-6,-24,0),(6,24,0)]
  EqualTolerance = true
  ExtensionAngle = 0
  FormatSpec = %.2w
  FormatSpecOverTolerance = %+.2w
  FormatSpecUnderTolerance = %+.2w
  Inverted = false
  LineAngle = 0
  LockPosition = false
  MeasureType = 1
  OverTolerance = 0
  References2D = -> [ProjItem014]
  Rotation = 0
  ScaleType = 0
  TheoreticalExact = false
  Type = 2
  UnderTolerance = 0
  X = -15.2309
  Y = 2.5
FEATURE [TechDraw::DrawPage] Page005  label="drawer:side"
  KeepUpdated = true
  NextBalloonIndex = 1
  ProjectionType = 0
  Template = -> Template005
  Views = -> [ProjGroup005,Dimension069,Dimension070,Dimension071,Dimension072,Dimension073,Dimension074,Dimension075,Dimension076]
FEATURE [TechDraw::DrawSVGTemplate] Template006
  EditableTexts = Designed_by_Name=Grzegorz Sapijaszko; Drawing_number=Drawing number; FC-Date=5/10/24; FC-SC=1 : 1; FC-SH=5 / 7; FC-Title=drill_press_table; Subtitle=Subtitle; Weight=Weight
  Height = 210
  Orientation = 1
  Template = <path>
  Width = 297
FEATURE [TechDraw::DrawProjGroupItem] ProjItem016  label="Front006"
  CoarseView = false
  Direction = (0,0,1)
  Focus = 100
  HardHidden = false
  IsoCount = 0
  IsoHidden = false
  IsoVisible = false
  LockPosition = true
  Perspective = false
  Rotation = 0
  RotationVector = (1,0,0)
  Scale = 0.5
  ScaleType = 2
  ScrubCount = 0
  SeamHidden = false
  SeamVisible = false
  SmoothHidden = false
  SmoothVisible = true
  Source = -> [Body019]
  Type = 0
  X = 0
  XDirection = (1,0,0)
  Y = 0
FEATURE [TechDraw::DrawProjGroupItem] ProjItem017  label="Right002"
  CoarseView = false
  Direction = (1,0,1e-16)
  Focus = 100
  HardHidden = false
  IsoCount = 0
  IsoHidden = false
  IsoVisible = false
  LockPosition = false
  Perspective = false
  Rotation = 0
  RotationVector = (1,0,0)
  Scale = 0.5
  ScaleType = 2
  ScrubCount = 0
  SeamHidden = false
  SeamVisible = false
  SmoothHidden = false
  SmoothVisible = true
  Source = -> [Body019]
  Type = 2
  X = -61.4
  XDirection = (1e-16,0,-1)
  Y = 0
FEATURE [TechDraw::DrawProjGroup] ProjGroup006
  Anchor = -> ProjItem016
  AutoDistribute = true
  LockPosition = false
  ProjectionType = 0
  Rotation = 0
  Scale = 0.5
  ScaleType = 2
  Source = -> [Body019]
  Views = -> [ProjItem016,ProjItem017]
  X = 160
  Y = 140
  spacingX = 15
  spacingY = 15
FEATURE [TechDraw::DrawViewDimension] Dimension077
  AngleOverride = false
  Arbitrary = false
  ArbitraryTolerances = false
  BoxCorners = (2) [(-45.65,-47,0),(45.65,47,0)]
  EqualTolerance = true
  ExtensionAngle = 0
  FormatSpec = %.2w
  FormatSpecOverTolerance = %+.2w
  FormatSpecUnderTolerance = %+.2w
  Inverted = false
  LineAngle = 0
  LockPosition = false
  MeasureType = 1
  OverTolerance = 0
  References2D = -> [ProjItem016]
  Rotation = 0
  ScaleType = 0
  TheoreticalExact = false
  Type = 1
  UnderTolerance = 0
  X = 0
  Y = -60.0007
FEATURE [TechDraw::DrawViewDimension] Dimension078
  AngleOverride = false
  Arbitrary = false
  ArbitraryTolerances = false
  BoxCorners = (2) [(-45.65,-47,0),(45.65,47,0)]
  EqualTolerance = true
  ExtensionAngle = 0
  FormatSpec = %.2w
  FormatSpecOverTolerance = %+.2w
  FormatSpecUnderTolerance = %+.2w
  Inverted = false
  LineAngle = 0
  LockPosition = false
  MeasureType = 1
  OverTolerance = 0
  References2D = -> [ProjItem016]
  Rotation = 0
  ScaleType = 0
  TheoreticalExact = false
  Type = 2
  UnderTolerance = 0
  X = 59.2526
  Y = 2.5
FEATURE [TechDraw::DrawViewDimension] Dimension079
  AngleOverride = false
  Arbitrary = false
  ArbitraryTolerances = false
  BoxCorners = (2) [(-0.75,-47,0),(0.75,47,0)]
  EqualTolerance = true
  ExtensionAngle = 0
  FormatSpec = %.2w
  FormatSpecOverTolerance = %+.2w
  FormatSpecUnderTolerance = %+.2w
  Inverted = false
  LineAngle = 0
  LockPosition = false
  MeasureType = 1
  OverTolerance = 0
  References2D = -> [ProjItem017]
  Rotation = 0
  ScaleType = 0
  TheoreticalExact = false
  Type = 1
  UnderTolerance = 0
  X = 4.89526
  Y = -59.6753
FEATURE [TechDraw::DrawPage] Page006  label="drawer:bottom"
  KeepUpdated = true
  NextBalloonIndex = 1
  ProjectionType = 0
  Template = -> Template006
  Views = -> [ProjGroup006,Dimension077,Dimension078,Dimension079]
FEATURE [TechDraw::DrawViewDimension] Dimension080
  AngleOverride = false
  Arbitrary = false
  ArbitraryTolerances = false
  BoxCorners = (2) [(-91.3,-6,0),(91.3,6,0)]
  EqualTolerance = true
  ExtensionAngle = 0
  FormatSpec = %.2w
  FormatSpecOverTolerance = %+.2w
  FormatSpecUnderTolerance = %+.2w
  Inverted = false
  LineAngle = 0
  LockPosition = false
  MeasureType = 1
  OverTolerance = 0
  References2D = -> [ProjItem011]
  Rotation = 0
  ScaleType = 0
  TheoreticalExact = false
  Type = 1
  UnderTolerance = 0
  X = -84.872
  Y = -7.80553
FEATURE [TechDraw::DrawPage] Page004  label="drawer:front"
  KeepUpdated = true
  NextBalloonIndex = 1
  ProjectionType = 0
  Template = -> Template004
  Views = -> [ProjGroup004,Dimension062,Dimension063,Dimension064,Dimension065,Dimension066,Dimension067,Dimension068,Dimension080]
FEATURE [TechDraw::DrawViewDimension] Dimension081
  AngleOverride = false
  Arbitrary = false
  ArbitraryTolerances = false
  BoxCorners = (2) [(-49.125,-42,0),(49.125,42,0)]
  EqualTolerance = true
  ExtensionAngle = 0
  FormatSpec = %.2w
  FormatSpecOverTolerance = %+.2w
  FormatSpecUnderTolerance = %+.2w
  Inverted = false
  LineAngle = 0
  LockPosition = false
  MeasureType = 1
  OverTolerance = 0
  References2D = -> [ProjItem006]
  Rotation = 0
  ScaleType = 0
  TheoreticalExact = false
  Type = 1
  UnderTolerance = 0
  X = 0
  Y = 57.5789
FEATURE [TechDraw::DrawPage] Page003  label="drawer:overal"
  KeepUpdated = true
  NextBalloonIndex = 1
  ProjectionType = 0
  Template = -> Template003
  Views = -> [ActiveView002,ProjGroup003,Dimension053,Dimension054,Dimension055,Dimension056,Dimension057,Dimension058,Dimension059,Dimension060,Dimension061,Dimension081]
FEATURE [App::DocumentObjectGroup] Group  label="drawings"
  Group = -> [Page,Page001,Page002,Page003,Page004,Page005,Page006]
note: 6 file-system paths scrubbed to <path> (originals preserved in the JSON sidecar)
